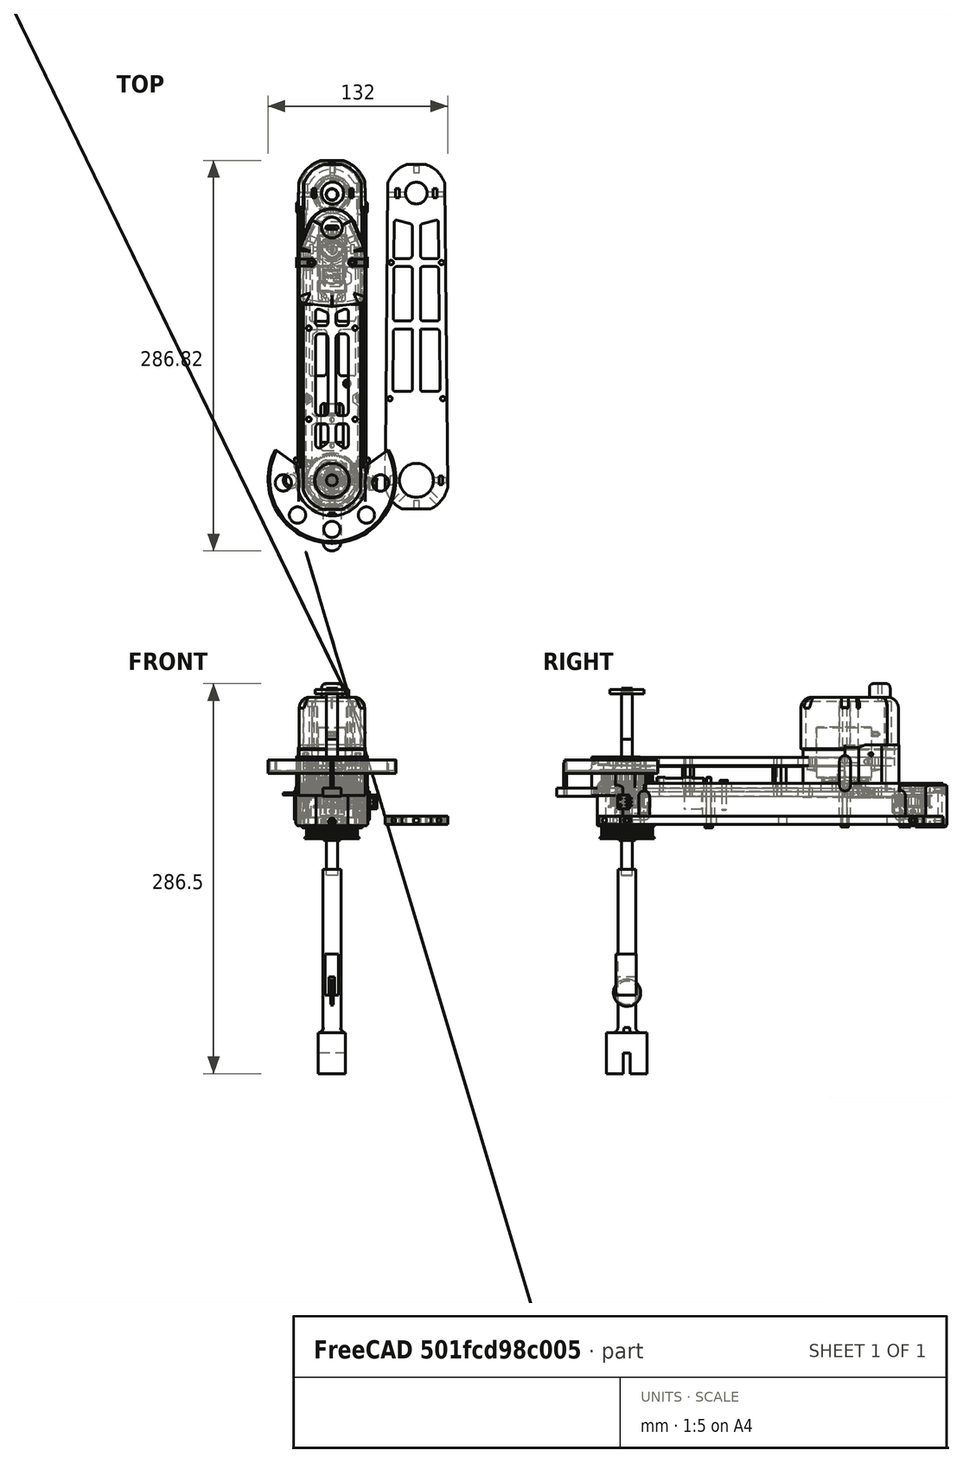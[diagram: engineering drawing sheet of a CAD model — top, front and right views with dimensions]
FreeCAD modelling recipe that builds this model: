
FCSTD DOCUMENT  (FreeCAD 1.0R38641 +468 (Git))
Label: ARM Long
License: All rights reserved
LicenseURL: https://en.wikipedia.org/wiki/All_rights_reserved
objects: Sketcher::SketchObject×133, PartDesign::Pocket×65, PartDesign::Pad×58, Part::Feature×42, PartDesign::Body×32, PartDesign::Fillet×20, App::Part×16, PartDesign::Chamfer×9, Part::FeaturePython×8, PartDesign::Plane×6, PartDesign::Mirrored×4, Mesh::Feature×3, PartDesign::Groove×1, PartDesign::ShapeBinder×1, Part::Mirroring×1
note: 823 computed .brp shape members not serialized (recipe doc carries the construction recipe); baked Part::Feature solids carry a one-line shape summary decoded from their .brp

FEATURE [Part::Feature] Part__Feature  label="MG995"
  Placement = pos=(1.91e-14,159.4,18.9) rot=(0,0,1;4.71239rad)
  shape: bbox 20 x 54.66 x 44.93 mm, 459 faces (baked)
FEATURE [Sketcher::SketchObject] Sketch009
  ArcFitTolerance = 1e-06
  AttachmentSupport = -> [YZ_Plane009]
  FullyConstrained = true
  MakeInternals = false
  MapMode = 5
  Placement = pos=(0,0,0) rot=(0.57735,0.57735,0.57735;2.0944rad)
  sketch-geometry (1):
    g0: Circle CenterX=0 CenterY=0 CenterZ=0 NormalX=0 NormalY=0 NormalZ=1 AngleXU=0 Radius=10
  constraints (2):
    c: Coincident(g0,g-1)
    c: Diameter(g0) = 20
FEATURE [PartDesign::Pad] Pad003
  Direction = (1,0,0)
  Length = 2
  Length2 = 10
  Midplane = true
  Placement = pos=(0,0,0) rot=(1,1,1;2.0944rad)
  Profile = -> Sketch009
  ReferenceAxis = -> Sketch009 [N_Axis]
  Refine = true
  Suppressed = false
  Type = 0
FEATURE [Sketcher::SketchObject] Sketch010
  ArcFitTolerance = 1e-06
  AttachmentSupport = -> [Pad003]
  FullyConstrained = true
  MakeInternals = false
  MapMode = 5
  Placement = pos=(-1,0,0) rot=(0.57735,0.57735,-0.57735;4.18879rad)
FEATURE [Sketcher::SketchObject] Sketch011
  ArcFitTolerance = 1e-06
  AttachmentSupport = -> [XZ_Plane009]
  FullyConstrained = false
  MakeInternals = false
  MapMode = 5
  Placement = pos=(0,0,0) rot=(1,0,0;1.5708rad)
  sketch-geometry (5):
    g0: LineSegment StartX=0.035712 StartY=-10.031 StartZ=0 EndX=-2.23615 EndY=-6.55241 EndZ=0
    g1: LineSegment StartX=-2.23615 StartY=-6.55241 StartZ=0 EndX=-4.35752 EndY=-11.9281 EndZ=0
    g2: LineSegment StartX=-4.35752 StartY=-11.9281 StartZ=0 EndX=3.67657 EndY=-11.9281 EndZ=0
    g3: LineSegment StartX=3.67657 StartY=-11.9281 StartZ=0 EndX=3.0311 EndY=-6.33671 EndZ=0
    g4: LineSegment StartX=3.0311 StartY=-6.33671 StartZ=0 EndX=0.035712 EndY=-10.031 EndZ=0
  constraints (6):
    c: Coincident(g0,g1)
    c: Coincident(g1,g2)
    c: Horizontal(g2)
    c: Coincident(g2,g3)
    c: Coincident(g3,g4)
    c: Coincident(g4,g0)
FEATURE [PartDesign::Groove] Groove
  Angle = 360
  Angle2 = 60
  Axis = (1,0,0)
  Base = (0,0,0)
  BaseFeature = -> Pad003
  Placement = pos=(0,0,0) rot=(1,1,1;2.0944rad)
  Profile = -> Sketch011
  ReferenceAxis = -> Sketch011 [H_Axis]
  Refine = true
  Suppressed = false
  Type = 0
FEATURE [PartDesign::Body] Body006  label="RUEDA"
  AllowCompound = false
  Group = -> [Sketch009,Pad003,Sketch010,Sketch011,Groove]
  Origin = -> Origin009
  Placement = pos=(0,0,-145.2) rot=(0,0,1;0rad)
  Tip = -> Groove
FEATURE [Sketcher::SketchObject] Sketch012
  ArcFitTolerance = 1e-06
  AttachmentSupport = -> [XY_Plane010]
  FullyConstrained = true
  MakeInternals = false
  MapMode = 5
  sketch-geometry (4):
    g0: LineSegment StartX=-5 StartY=7.5 StartZ=0 EndX=-5 EndY=-7.5 EndZ=0
    g1: LineSegment StartX=-5 StartY=-7.5 StartZ=0 EndX=5 EndY=-7.5 EndZ=0
    g2: LineSegment StartX=5 StartY=-7.5 StartZ=0 EndX=5 EndY=7.5 EndZ=0
    g3: LineSegment StartX=5 StartY=7.5 StartZ=0 EndX=-5 EndY=7.5 EndZ=0
  constraints (10):
    c: Coincident(g0,g1)
    c: Coincident(g1,g2)
    c: Coincident(g2,g3)
    c: Coincident(g3,g0)
    c: Vertical(g0)
    c: Horizontal(g1)
    c: Symmetric(g0,g2,g-2)
    c: DistanceX(g0,g2) = 10
    c: DistanceY(g0,g0) = 15
    c: Symmetric(g2,g1,g-1)
FEATURE [PartDesign::Pad] Pad004
  Direction = (0,0,1)
  Length = 30
  Length2 = 10
  Profile = -> Sketch012
  ReferenceAxis = -> Sketch012 [N_Axis]
  Refine = true
  Suppressed = false
  Type = 0
FEATURE [Sketcher::SketchObject] Sketch013
  ArcFitTolerance = 1e-06
  AttachmentSupport = -> [Pad004]
  FullyConstrained = false
  MakeInternals = false
  MapMode = 5
  Placement = pos=(0,-7.5,0) rot=(1,0,0;1.5708rad)
  sketch-geometry (4):
    g0: LineSegment StartX=-1.97312 StartY=37.3431 StartZ=0 EndX=-1.97312 EndY=16.6977 EndZ=0
    g1: LineSegment StartX=-1.97312 StartY=16.6977 StartZ=0 EndX=2.0662 EndY=16.6977 EndZ=0
    g2: LineSegment StartX=2.0662 StartY=16.6977 StartZ=0 EndX=2.0662 EndY=37.3431 EndZ=0
    g3: LineSegment StartX=2.0662 StartY=37.3431 StartZ=0 EndX=-1.97312 EndY=37.3431 EndZ=0
  constraints (8):
    c: Coincident(g0,g1)
    c: Coincident(g1,g2)
    c: Coincident(g2,g3)
    c: Coincident(g3,g0)
    c: Vertical(g0)
    c: Vertical(g2)
    c: Horizontal(g1)
    c: Horizontal(g3)
FEATURE [PartDesign::Pocket] Pocket003
  BaseFeature = -> Pad004
  Direction = (0,1,-2e-16)
  Length = 5
  Length2 = 5
  Profile = -> Sketch013
  ReferenceAxis = -> Sketch013 [N_Axis]
  Refine = true
  Suppressed = false
  Type = 1
FEATURE [PartDesign::Body] Body007  label="HORQUILLA"
  AllowCompound = false
  Group = -> [Sketch012,Pad004,Sketch013,Pocket003]
  Origin = -> Origin010
  Placement = pos=(-0.1,-0.7,-116.9) rot=(1,0,0;3.14159rad)
  Tip = -> Pocket003
FEATURE [Sketcher::SketchObject] Sketch016
  ArcFitTolerance = 1e-06
  AttachmentSupport = -> [XY_Plane012]
  FullyConstrained = false
  MakeInternals = false
  MapMode = 5
  sketch-geometry (11):
    g0: Circle CenterX=0 CenterY=-27.1564 CenterZ=0 NormalX=0 NormalY=0 NormalZ=1 AngleXU=0 Radius=170
    g1: LineSegment StartX=-241.503 StartY=142.844 StartZ=0 EndX=520.637 EndY=142.844 EndZ=0
    g2: Circle CenterX=340 CenterY=-27.1564 CenterZ=0 NormalX=0 NormalY=0 NormalZ=1 AngleXU=0 Radius=170
    g3: LineSegment StartX=-227.087 StartY=-237.156 StartZ=0 EndX=679.032 EndY=-237.156 EndZ=0
    g4: LineSegment StartX=340 StartY=-237.156 StartZ=0 EndX=256.874 EndY=-44.3091 EndZ=0
    g5: LineSegment StartX=256.874 StartY=-44.3091 StartZ=0 EndX=189.582 EndY=111.805 EndZ=0
    g6: LineSegment StartX=340 StartY=-237.156 StartZ=0 EndX=349.666 EndY=-301.689 EndZ=0
    g7: LineSegment StartX=-425.206 StartY=-27.1564 StartZ=0 EndX=717.157 EndY=-27.1564 EndZ=0
    g8: LineSegment [constr] StartX=162.156 StartY=-197.156 StartZ=0 EndX=684.616 EndY=-197.156 EndZ=0
    g9: LineSegment [constr] StartX=340 StartY=225.233 StartZ=0 EndX=340 EndY=-279.546 EndZ=0
    g10: Circle CenterX=340 CenterY=-27.1564 CenterZ=0 NormalX=0 NormalY=0 NormalZ=1 AngleXU=0 Radius=55
  constraints (23):
    c: Diameter(g0) = 340
    c: PointOnObject(g0,g-2)
    c: Horizontal(g1)
    c: Tangent(g1,g0)
    c: Block(g1)
    c: Diameter(g2) = 340
    c: Tangent(g0,g2)
    c: Horizontal(g3)
    c: DistanceY(g3,g1) = 380
    c: PointOnObject(g4,g3)
    c: Coincident(g4,g5)
    c: Distance(g4,g5) = 170
    c: Distance(g4,g4) = 210
    c: Coincident(g6,g4)
    c: Vertical(g2,g4)
    c: Horizontal(g7)
    c: Horizontal(g8)
    c: Tangent(g8,g2)
    c: PointOnObject(g2,g9)
    c: PointOnObject(g4,g9)
    c: Symmetric(g9,g9,g10)
    c: Diameter(g10) = 110
    c: DistanceY(g7,g1) = 170
FEATURE [PartDesign::Body] Body009  label="GEOMETRY"
  AllowCompound = false
  Group = -> [Sketch016]
  Origin = -> Origin012
FEATURE [Sketcher::SketchObject] Sketch018
  ArcFitTolerance = 1e-06
  AttachmentSupport = -> [XY_Plane015]
  FullyConstrained = false
  MakeInternals = false
  MapMode = 5
  sketch-geometry (40):
    g0: LineSegment [constr] StartX=-66.1561 StartY=0 StartZ=0 EndX=72.2125 EndY=0 EndZ=0
    g1: LineSegment [constr] StartX=-43.6589 StartY=170 StartZ=0 EndX=73.8752 EndY=170 EndZ=0
    g2: LineSegment StartX=-21 StartY=170 StartZ=0 EndX=-21 EndY=-6.55744 EndZ=0
    g3: LineSegment StartX=-6.55744 StartY=-21 StartZ=0 EndX=6.55744 EndY=-21 EndZ=0
    g4: LineSegment StartX=21 StartY=-6.55744 StartZ=0 EndX=21 EndY=170 EndZ=0
    g5: Circle CenterX=-1.1e-15 CenterY=0 CenterZ=0 NormalX=0 NormalY=0 NormalZ=1 AngleXU=0 Radius=12.65
    g6: ArcOfCircle CenterX=-1.1e-15 CenterY=0 CenterZ=0 NormalX=0 NormalY=0 NormalZ=1 AngleXU=0 Radius=22 StartAngle=3.44426 EndAngle=4.40972
    g7: ArcOfCircle CenterX=-1.1e-15 CenterY=0 CenterZ=0 NormalX=0 NormalY=0 NormalZ=1 AngleXU=0 Radius=22 StartAngle=5.01505 EndAngle=5.98052
    g8: ArcOfCircle CenterX=0 CenterY=181.247 CenterZ=0 NormalX=0 NormalY=0 NormalZ=1 AngleXU=0 Radius=15.1624 StartAngle=0.389165 EndAngle=2.75243
    g9: LineSegment StartX=-14.0287 StartY=187 StartZ=0 EndX=-21 EndY=170 EndZ=0
    g10: LineSegment StartX=14.0287 StartY=187 StartZ=0 EndX=21 EndY=170 EndZ=0
    g11: LineSegment [constr] StartX=-50.6378 StartY=187 StartZ=0 EndX=60.3893 EndY=187 EndZ=0
    g12: GeomPoint X=3.72478 Y=-21 Z=0
    g13: LineSegment StartX=-10.8839 StartY=180.662 StartZ=0 EndX=-10.8839 EndY=138.383 EndZ=0
    g14: LineSegment [constr] StartX=-10.8839 StartY=180.662 StartZ=0 EndX=-10.8839 EndY=138.383 EndZ=0
    g15: LineSegment [constr] StartX=-10.8839 StartY=138.383 StartZ=0 EndX=10.8839 EndY=138.383 EndZ=0
    g16: LineSegment [constr] StartX=10.8839 StartY=138.383 StartZ=0 EndX=10.8839 EndY=180.662 EndZ=0
    g17: LineSegment StartX=10.8839 StartY=180.662 StartZ=0 EndX=10.8839 EndY=154.01 EndZ=0
    g18: LineSegment StartX=11.1741 StartY=153.519 StartZ=0 EndX=13.7289 EndY=152.117 EndZ=0
    g19: LineSegment StartX=14.0513 StartY=151.572 StartZ=0 EndX=14.0513 EndY=145.924 EndZ=0
    g20: LineSegment StartX=10.8839 StartY=138.383 StartZ=0 EndX=10.8839 EndY=143.674 EndZ=0
    g21: LineSegment StartX=11.1847 StartY=144.155 StartZ=0 EndX=13.7156 EndY=145.387 EndZ=0
    g22: ArcOfCircle CenterX=0 CenterY=183.662 CenterZ=0 NormalX=0 NormalY=0 NormalZ=1 AngleXU=0 Radius=1 StartAngle=1.2e-15 EndAngle=3.14159
    g23: LineSegment StartX=1 StartY=183.662 StartZ=0 EndX=1 EndY=180.662 EndZ=0
    g24: LineSegment StartX=-1 StartY=183.662 StartZ=0 EndX=-1 EndY=180.662 EndZ=0
    g25: LineSegment StartX=-10.8839 StartY=180.662 StartZ=0 EndX=-1 EndY=180.662 EndZ=0
    g26: LineSegment StartX=10.8839 StartY=180.662 StartZ=0 EndX=1 EndY=180.662 EndZ=0
    g27: ArcOfCircle CenterX=13.4297 CenterY=151.572 CenterZ=0 NormalX=0 NormalY=0 NormalZ=1 AngleXU=0 Radius=0.621593 StartAngle=-3.6e-15 EndAngle=1.06874
    g28: GeomPoint [constr] X=14.0513 Y=151.94 Z=0
    g29: ArcOfCircle CenterX=13.4543 CenterY=145.924 CenterZ=0 NormalX=0 NormalY=0 NormalZ=1 AngleXU=0 Radius=0.597072 StartAngle=5.16551 EndAngle=6.28319
    g30: GeomPoint [constr] X=14.0513 Y=145.551 Z=0
    g31: ArcOfCircle CenterX=11.4189 CenterY=143.674 CenterZ=0 NormalX=0 NormalY=0 NormalZ=1 AngleXU=0 Radius=0.535029 StartAngle=2.02392 EndAngle=3.14159
    g32: GeomPoint [constr] X=10.8839 Y=144.009 Z=0
    g33: ArcOfCircle CenterX=11.4434 CenterY=154.01 CenterZ=0 NormalX=0 NormalY=0 NormalZ=1 AngleXU=0 Radius=0.559551 StartAngle=3.14159 EndAngle=4.21034
    g34: GeomPoint [constr] X=10.8839 Y=153.678 Z=0
    g35: ArcOfCircle CenterX=0 CenterY=135.596 CenterZ=0 NormalX=0 NormalY=0 NormalZ=1 AngleXU=0 Radius=1 StartAngle=3.14159 EndAngle=6.28319
    g36: LineSegment StartX=1 StartY=138.383 StartZ=0 EndX=1 EndY=135.596 EndZ=0
    g37: LineSegment StartX=-1 StartY=138.383 StartZ=0 EndX=-1 EndY=135.596 EndZ=0
    g38: LineSegment StartX=-1 StartY=138.383 StartZ=0 EndX=-10.8839 EndY=138.383 EndZ=0
    g39: LineSegment StartX=1 StartY=138.383 StartZ=0 EndX=10.8839 EndY=138.383 EndZ=0
  constraints (84):
    c: Horizontal(g1)
    c: DistanceY(g0,g1) = 170
    c: Vertical(g2)
    c: PointOnObject(g2,g1)
    c: PointOnObject(g5,g0)
    c: Symmetric(g10,g9,g-2)
    c: Diameter(g5) = 25.3
    c: DistanceX(g2,g4) = 42
    c: Symmetric(g2,g4,g-2)
    c: Symmetric(g3,g3,g-2)
    c: Coincident(g6,g2)
    c: Coincident(g6,g3)
    c: Coincident(g7,g6)
    c: Coincident(g7,g4)
    c: Coincident(g7,g3)
    c: Coincident(g6,g5)
    c: PointOnObject(g8,g-2)
    c: Tangent(g9,g8) = -1.5708
    c: Tangent(g10,g8) = 1.5708
    c: Coincident(g2,g9)
    c: Coincident(g10,g4)
    c: Horizontal(g11)
    c: PointOnObject(g8,g11)
    c: DistanceY(g1,g11) = 17
    c: PointOnObject(g12,g3)
    c: DistanceY(g12,g0) = 21
    c: PointOnObject(g5,g-1)
    c: PointOnObject(g0,g-1)
    c: Vertical(g13)
    c: Symmetric(g13,g15,g-2)
    c: Coincident(g14,g15)
    c: Coincident(g15,g16)
    c: Vertical(g14)
    c: Vertical(g16)
    c: Horizontal(g15)
    c: Symmetric(g16,g14,g-2)
    c: Radius(g6) = 22
    c: PointOnObject(g34,g16)
    c: Vertical(g17)
    c: Vertical(g19)
    c: Coincident(g20,g15)
    c: PointOnObject(g32,g16)
    c: Tangent(g22,g23) = 1.5708
    c: Tangent(g22,g24) = -1.5708
    c: Vertical(g24)
    c: PointOnObject(g22,g-2)
    c: Coincident(g25,g13)
    c: Horizontal(g25)
    c: Coincident(g26,g17)
    c: Horizontal(g26)
    c: Horizontal(g25,g26)
    c: Coincident(g24,g25)
    c: Coincident(g23,g26)
    c: DistanceX(g24,g23) = 2
    c: Vertical(g23)
    c: DistanceY(g23,g22) = 3
    c: PointOnObject(g28,g18)
    c: PointOnObject(g28,g19)
    c: Tangent(g18,g27) = 1.5708
    c: Tangent(g19,g27) = 1.5708
    c: PointOnObject(g30,g19)
    c: PointOnObject(g30,g21)
    c: Tangent(g19,g29) = 1.5708
    c: Tangent(g21,g29) = -1.5708
    c: PointOnObject(g32,g20)
    c: PointOnObject(g32,g21)
    c: Tangent(g20,g31) = 1.5708
    c: Tangent(g21,g31) = 1.5708
    c: PointOnObject(g34,g18)
    c: Tangent(g17,g33) = -1.5708
    c: Tangent(g18,g33) = -1.5708
    c: Tangent(g35,g36) = 1.5708
    c: Tangent(g35,g37) = -1.5708
    c: Vertical(g37)
    c: PointOnObject(g35,g-2)
    c: PointOnObject(g37,g15)
    c: PointOnObject(g36,g15)
    c: Vertical(g36)
    c: Coincident(g38,g37)
    c: Coincident(g38,g13)
    c: Coincident(g39,g36)
    c: Coincident(g39,g15)
    c: DistanceX(g37,g36) = 2
    c: Coincident(g16,g17)
FEATURE [PartDesign::Pad] Pad008
  Direction = (0,0,1)
  Length = 6
  Length2 = 10
  Profile = -> Sketch018
  ReferenceAxis = -> Sketch018 [N_Axis]
  Refine = true
  Suppressed = false
  Type = 0
FEATURE [Sketcher::SketchObject] Sketch020
  ArcFitTolerance = 1e-06
  AttachmentSupport = -> [Pad008]
  ExternalGeometry = -> [Pad008]
  FullyConstrained = false
  MakeInternals = false
  MapMode = 5
  Placement = pos=(0,0,6) rot=(0,0,1;0rad)
  sketch-geometry (16):
    g0: LineSegment [constr] StartX=-17 StartY=112 StartZ=0 EndX=-17 EndY=45 EndZ=0
    g1: LineSegment [constr] StartX=-17 StartY=45 StartZ=0 EndX=17 EndY=45 EndZ=0
    g2: LineSegment [constr] StartX=17 StartY=45 StartZ=0 EndX=17 EndY=112 EndZ=0
    g3: LineSegment [constr] StartX=17 StartY=112 StartZ=0 EndX=-17 EndY=112 EndZ=0
    g4: Circle CenterX=17 CenterY=112 CenterZ=0 NormalX=0 NormalY=0 NormalZ=1 AngleXU=0 Radius=1.7
    g5: Circle CenterX=-17 CenterY=112 CenterZ=0 NormalX=0 NormalY=0 NormalZ=1 AngleXU=0 Radius=1.7
    g6: Circle CenterX=17 CenterY=45 CenterZ=0 NormalX=0 NormalY=0 NormalZ=1 AngleXU=0 Radius=1.7
    g7: Circle CenterX=-17 CenterY=45 CenterZ=0 NormalX=0 NormalY=0 NormalZ=1 AngleXU=0 Radius=1.7
    g8: LineSegment [constr] StartX=-5 StartY=183.792 StartZ=0 EndX=-5 EndY=135.241 EndZ=0
    g9: LineSegment [constr] StartX=-5 StartY=135.241 StartZ=0 EndX=5 EndY=135.241 EndZ=0
    g10: LineSegment [constr] StartX=5 StartY=135.241 StartZ=0 EndX=5 EndY=183.792 EndZ=0
    g11: LineSegment [constr] StartX=5 StartY=183.792 StartZ=0 EndX=-5 EndY=183.792 EndZ=0
    g12: Circle CenterX=-5 CenterY=135.241 CenterZ=0 NormalX=0 NormalY=0 NormalZ=1 AngleXU=0 Radius=1.25
    g13: Circle CenterX=5 CenterY=135.241 CenterZ=0 NormalX=0 NormalY=0 NormalZ=1 AngleXU=0 Radius=1.25
    g14: Circle CenterX=5 CenterY=183.792 CenterZ=0 NormalX=0 NormalY=0 NormalZ=1 AngleXU=0 Radius=1.25
    g15: Circle CenterX=-5 CenterY=183.792 CenterZ=0 NormalX=0 NormalY=0 NormalZ=1 AngleXU=0 Radius=1.25
  constraints (36):
    c: Coincident(g0,g1)
    c: Coincident(g1,g2)
    c: Coincident(g2,g3)
    c: Coincident(g3,g0)
    c: Vertical(g0)
    c: Vertical(g2)
    c: Horizontal(g1)
    c: Symmetric(g0,g2,g-2)
    c: DistanceX(g-1,g1) = 17
    c: Coincident(g4,g2)
    c: Coincident(g5,g0)
    c: Coincident(g6,g1)
    c: Coincident(g7,g0)
    c: Equal(g7,g6)
    c: Equal(g7,g4)
    c: Equal(g7,g5)
    c: Diameter(g7) = 3.4
    c: DistanceY(g-1,g1) = 45
    c: DistanceY(g-1,g2) = 112
    c: Coincident(g8,g9)
    c: Coincident(g9,g10)
    c: Coincident(g10,g11)
    c: Coincident(g11,g8)
    c: Vertical(g8)
    c: Vertical(g10)
    c: Horizontal(g9)
    c: Symmetric(g8,g10,g-2)
    c: Coincident(g12,g8)
    c: Coincident(g13,g9)
    c: Coincident(g14,g10)
    c: Coincident(g15,g8)
    c: Equal(g15,g14)
    c: Equal(g15,g12)
    c: Equal(g15,g13)
    c: Diameter(g15) = 2.5
    c: DistanceX(g8,g10) = 10
FEATURE [PartDesign::Pocket] Pocket005
  BaseFeature = -> Pad008
  Direction = (0,0,-1)
  Length = 5
  Length2 = 5
  Profile = -> Sketch020
  ReferenceAxis = -> Sketch020 [N_Axis]
  Refine = true
  Suppressed = false
  Type = 1
FEATURE [Part::Feature] Part__Feature003  label="Шкив GT2 60T b8 (6mm)"
  Placement = pos=(0,5.4e-15,24.6) rot=(1,0,0;4.71239rad)
  shape: bbox 40 x 40 x 16 mm, 326 faces (baked)
FEATURE [Part::Feature] Part__Feature004  label="Шкив GT2 60T b8 (6mm)001"
  Placement = pos=(0,-1.42e-14,-16) rot=(-1,0,0;1.5708rad)
  shape: bbox 40 x 40 x 16 mm, 326 faces (baked)
FEATURE [Sketcher::SketchObject] Sketch021
  ArcFitTolerance = 1e-06
  AttachmentSupport = -> [XY_Plane017]
  FullyConstrained = false
  MakeInternals = false
  MapMode = 5
  sketch-geometry (44):
    g0: LineSegment StartX=-23 StartY=-5 StartZ=0 EndX=-21 EndY=218 EndZ=0
    g1: LineSegment StartX=23 StartY=-5 StartZ=0 EndX=21 EndY=218 EndZ=0
    g2: Circle CenterX=4.97e-14 CenterY=211 CenterZ=0 NormalX=0 NormalY=0 NormalZ=1 AngleXU=0 Radius=8.1
    g3: Circle CenterX=0 CenterY=-141.268 CenterZ=0 NormalX=0 NormalY=0 NormalZ=1 AngleXU=0 Radius=9.71
    g4: Circle CenterX=0 CenterY=0 CenterZ=0 NormalX=0 NormalY=0 NormalZ=1 AngleXU=0 Radius=8.1
    g5: LineSegment StartX=-7 StartY=232 StartZ=0 EndX=7 EndY=232 EndZ=0
    g6: ArcOfCircle CenterX=4.97e-14 CenterY=211 CenterZ=0 NormalX=0 NormalY=0 NormalZ=1 AngleXU=0 Radius=22.1359 StartAngle=1.89255 EndAngle=2.81984
    g7: ArcOfCircle CenterX=4.97e-14 CenterY=211 CenterZ=0 NormalX=0 NormalY=0 NormalZ=1 AngleXU=0 Radius=22.1359 StartAngle=0.321751 EndAngle=1.24905
    g8: LineSegment StartX=-10.6301 StartY=-21 StartZ=0 EndX=10.6301 EndY=-21 EndZ=0
    g9: ArcOfCircle CenterX=0 CenterY=0 CenterZ=0 NormalX=0 NormalY=0 NormalZ=1 AngleXU=0 Radius=23.5372 StartAngle=3.35565 EndAngle=4.2438
    g10: ArcOfCircle CenterX=0 CenterY=0 CenterZ=0 NormalX=0 NormalY=0 NormalZ=1 AngleXU=0 Radius=23.5372 StartAngle=5.18098 EndAngle=6.06912
    g11: LineSegment [constr] StartX=-22.417 StartY=60 StartZ=0 EndX=22.417 EndY=60 EndZ=0
    g12: GeomPoint [constr] X=32.4275 Y=0 Z=0
    g13: GeomPoint [constr] X=21.5202 Y=160 Z=0
    g14: LineSegment [constr] StartX=21.5202 StartY=160 StartZ=0 EndX=-21.5202 EndY=160 EndZ=0
    g15: GeomPoint [constr] X=18.5202 Y=160 Z=0
    g16: GeomPoint [constr] X=-18.5202 Y=160 Z=0
    g17: GeomPoint [constr] X=-19.417 Y=60 Z=0
    g18: GeomPoint [constr] X=19.417 Y=60 Z=0
    g19: LineSegment StartX=13.6 StartY=3.25 StartZ=0 EndX=13.6 EndY=-3.25 EndZ=0
    g20: LineSegment StartX=13.6 StartY=-3.25 StartZ=0 EndX=16.4 EndY=-3.25 EndZ=0
    g21: LineSegment StartX=16.4 StartY=-3.25 StartZ=0 EndX=16.4 EndY=3.25 EndZ=0
    g22: LineSegment StartX=16.4 StartY=3.25 StartZ=0 EndX=13.6 EndY=3.25 EndZ=0
    g23: GeomPoint [constr] X=15 Y=0 Z=0
    g24: LineSegment StartX=-16.4 StartY=3.25 StartZ=0 EndX=-16.4 EndY=-3.25 EndZ=0
    g25: LineSegment StartX=-16.4 StartY=-3.25 StartZ=0 EndX=-13.6 EndY=-3.25 EndZ=0
    g26: LineSegment StartX=-13.6 StartY=-3.25 StartZ=0 EndX=-13.6 EndY=3.25 EndZ=0
    g27: LineSegment StartX=-13.6 StartY=3.25 StartZ=0 EndX=-16.4 EndY=3.25 EndZ=0
    g28: GeomPoint [constr] X=-15 Y=0 Z=0
    g29: LineSegment [constr] StartX=-13.769 StartY=211 StartZ=0 EndX=13.769 EndY=211 EndZ=0
    g30: LineSegment StartX=12.369 StartY=214.25 StartZ=0 EndX=12.369 EndY=207.75 EndZ=0
    g31: LineSegment StartX=12.369 StartY=207.75 StartZ=0 EndX=15.169 EndY=207.75 EndZ=0
    g32: LineSegment StartX=15.169 StartY=207.75 StartZ=0 EndX=15.169 EndY=214.25 EndZ=0
    g33: LineSegment StartX=15.169 StartY=214.25 StartZ=0 EndX=12.369 EndY=214.25 EndZ=0
    g34: GeomPoint [constr] X=13.769 Y=211 Z=0
    g35: LineSegment StartX=-15.169 StartY=214.25 StartZ=0 EndX=-15.169 EndY=207.75 EndZ=0
    g36: LineSegment StartX=-15.169 StartY=207.75 StartZ=0 EndX=-12.369 EndY=207.75 EndZ=0
    g37: LineSegment StartX=-12.369 StartY=207.75 StartZ=0 EndX=-12.369 EndY=214.25 EndZ=0
    g38: LineSegment StartX=-12.369 StartY=214.25 StartZ=0 EndX=-15.169 EndY=214.25 EndZ=0
    g39: GeomPoint [constr] X=-13.769 Y=211 Z=0
    g40: Circle CenterX=18.5202 CenterY=160 CenterZ=0 NormalX=0 NormalY=0 NormalZ=1 AngleXU=0 Radius=1.7
    g41: Circle CenterX=-18.5202 CenterY=160 CenterZ=0 NormalX=0 NormalY=0 NormalZ=1 AngleXU=0 Radius=1.7
    g42: Circle CenterX=-19.417 CenterY=60 CenterZ=0 NormalX=0 NormalY=0 NormalZ=1 AngleXU=0 Radius=1.7
    g43: Circle CenterX=19.417 CenterY=60 CenterZ=0 NormalX=0 NormalY=0 NormalZ=1 AngleXU=0 Radius=1.7
  constraints (106):
    c: PointOnObject(g3,g-2)
    c: Symmetric(g5,g5,g-2)
    c: DistanceY(g2,g5) = 21
    c: Coincident(g6,g2)
    c: Coincident(g6,g5)
    c: Coincident(g6,g0)
    c: Coincident(g7,g2)
    c: Coincident(g7,g5)
    c: Coincident(g7,g1)
    c: Symmetric(g8,g8,g-2)
    c: DistanceY(g8,g4) = 21
    c: PointOnObject(g4,g-2)
    c: PointOnObject(g4,g-1)
    c: Coincident(g9,g4)
    c: Coincident(g9,g0)
    c: Coincident(g9,g8)
    c: Coincident(g10,g4)
    c: Coincident(g10,g1)
    c: Coincident(g10,g8)
    c: PointOnObject(g12,g-1)
    c: DistanceY(g12,g11) = 60
    c: DistanceY(g12,g13) = 160
    c: DistanceY(g12,g2) = 211
    c: Diameter(g4) = 16.2
    c: Diameter(g2) = 16.2
    c: Horizontal(g0,g1)
    c: DistanceX(g0,g1) = 46
    c: DistanceY(g0,g4) = 5
    c: Symmetric(g0,g1,g-2)
    c: DistanceX(g0,g1) = 42
    c: DistanceY(g2,g1) = 7
    c: Coincident(g14,g13)
    c: Horizontal(g14)
    c: PointOnObject(g13,g1)
    c: PointOnObject(g15,g14)
    c: DistanceX(g15,g13) = 3
    c: PointOnObject(g14,g0)
    c: PointOnObject(g16,g14)
    c: DistanceX(g14,g16) = 3
    c: PointOnObject(g11,g1)
    c: Horizontal(g11)
    c: PointOnObject(g11,g0)
    c: PointOnObject(g17,g11)
    c: PointOnObject(g18,g11)
    c: DistanceX(g18,g11) = 3
    c: DistanceX(g11,g17) = 3
    c: Coincident(g19,g20)
    c: Coincident(g20,g21)
    c: Coincident(g21,g22)
    c: Coincident(g22,g19)
    c: Vertical(g19)
    c: Vertical(g21)
    c: Horizontal(g20)
    c: Horizontal(g22)
    c: Symmetric(g21,g19,g23)
    c: PointOnObject(g23,g-1)
    c: Coincident(g24,g25)
    c: Coincident(g25,g26)
    c: Coincident(g26,g27)
    c: Coincident(g27,g24)
    c: Vertical(g24)
    c: Vertical(g26)
    c: Horizontal(g25)
    c: Horizontal(g27)
    c: Symmetric(g26,g24,g28)
    c: PointOnObject(g28,g-1)
    c: DistanceX(g24,g26) = 2.8
    c: DistanceY(g25,g26) = 6.5
    c: Equal(g26,g19)
    c: Equal(g22,g27)
    c: DistanceX(g28,g4) = 15
    c: DistanceX(g4,g23) = 15
    c: PointOnObject(g2,g29)
    c: Coincident(g30,g31)
    c: Coincident(g31,g32)
    c: Coincident(g32,g33)
    c: Coincident(g33,g30)
    c: Vertical(g30)
    c: Vertical(g32)
    c: Horizontal(g31)
    c: Horizontal(g33)
    c: Symmetric(g32,g30,g34)
    c: Coincident(g34,g29)
    c: Coincident(g35,g36)
    c: Coincident(g36,g37)
    c: Coincident(g37,g38)
    c: Coincident(g38,g35)
    c: Vertical(g35)
    c: Vertical(g37)
    c: Horizontal(g36)
    c: Horizontal(g38)
    c: Symmetric(g37,g35,g39)
    c: Coincident(g39,g29)
    c: DistanceX(g35,g36) = 2.8
    c: DistanceY(g36,g37) = 6.5
    c: Symmetric(g29,g29,g-2)
    c: Equal(g37,g30)
    c: Equal(g38,g33)
    c: Coincident(g40,g15)
    c: Coincident(g41,g16)
    c: Coincident(g42,g17)
    c: Coincident(g43,g18)
    c: Equal(g43,g42)
    c: Equal(g43,g41)
    c: Equal(g43,g40)
    c: Diameter(g43) = 3.4
FEATURE [PartDesign::Pad] Pad009
  Direction = (0,0,1)
  Length = 6
  Length2 = 10
  Profile = -> Sketch021
  ReferenceAxis = -> Sketch021 [N_Axis]
  Refine = true
  Suppressed = false
  Type = 0
FEATURE [Sketcher::SketchObject] Sketch022
  ArcFitTolerance = 1e-06
  AttachmentSupport = -> [XY_Plane018]
  FullyConstrained = true
  MakeInternals = false
  MapMode = 5
  sketch-geometry (1):
    g0: Circle CenterX=0 CenterY=0 CenterZ=0 NormalX=0 NormalY=0 NormalZ=1 AngleXU=0 Radius=4
  constraints (2):
    c: Coincident(g0,g-1)
    c: Diameter(g0) = 8
FEATURE [PartDesign::Pad] Pad010
  Direction = (0,0,1)
  Length = 40
  Length2 = 10
  Profile = -> Sketch022
  ReferenceAxis = -> Sketch022 [N_Axis]
  Refine = true
  Suppressed = false
  Type = 0
FEATURE [PartDesign::Body] Body014  label="ROD 8X40"
  AllowCompound = false
  Group = -> [Sketch022,Pad010]
  Origin = -> Origin018
  Placement = pos=(0,3e-16,1.1) rot=(0,0,1;0rad)
  Tip = -> Pad010
FEATURE [Sketcher::SketchObject] Sketch023
  ArcFitTolerance = 1e-06
  AttachmentSupport = -> [XY_Plane019]
  FullyConstrained = true
  MakeInternals = false
  MapMode = 5
  sketch-geometry (1):
    g0: Circle CenterX=0 CenterY=0 CenterZ=0 NormalX=0 NormalY=0 NormalZ=1 AngleXU=0 Radius=4
  constraints (2):
    c: Coincident(g0,g-1)
    c: Diameter(g0) = 8
FEATURE [PartDesign::Pad] Pad011
  Direction = (0,0,1)
  Length = 60
  Length2 = 10
  Profile = -> Sketch023
  ReferenceAxis = -> Sketch023 [N_Axis]
  Refine = true
  Suppressed = false
  Type = 0
FEATURE [PartDesign::Body] Body015  label="ROD 8X60"
  AllowCompound = false
  Group = -> [Sketch023,Pad011]
  Origin = -> Origin019
  Placement = pos=(0,1e-16,1) rot=(1,0,0;3.14159rad)
  Tip = -> Pad011
FEATURE [Sketcher::SketchObject] Sketch024
  ArcFitTolerance = 1e-06
  AttachmentSupport = -> [XY_Plane020]
  FullyConstrained = true
  MakeInternals = false
  MapMode = 5
  sketch-geometry (1):
    g0: Circle CenterX=0 CenterY=0 CenterZ=0 NormalX=0 NormalY=0 NormalZ=1 AngleXU=0 Radius=4
  constraints (2):
    c: Coincident(g0,g-1)
    c: Diameter(g0) = 8
FEATURE [PartDesign::Pad] Pad012
  Direction = (0,0,1)
  Length = 80
  Length2 = 10
  Profile = -> Sketch024
  ReferenceAxis = -> Sketch024 [N_Axis]
  Refine = true
  Suppressed = false
  Type = 0
FEATURE [PartDesign::Body] Body016  label="ROD 8X80"
  AllowCompound = false
  Group = -> [Sketch024,Pad012]
  Origin = -> Origin020
  Placement = pos=(0,0,-1.6) rot=(0,0,1;0rad)
  Tip = -> Pad012
FEATURE [Part::Feature] Part__Feature008  label="p  BEARING, METRIC 600 MINIATURE SERIES, DOUBLE-SEALED  8mm ID × 22 OD × 7 W  —  608-2RS001"
  Placement = pos=(0,169.9,1.8) rot=(0,0,1;0rad)
  shape: bbox 23.81 x 23.81 x 7.015 mm, 606 faces (baked)
FEATURE [Part::Feature] Part__Feature010  label="bearing"
  shape: bbox 8.659 x 4.3 x 8.659 mm, 17 faces (baked)
FEATURE [Part::Feature] Part__Feature011  label="bearing001"
  shape: bbox 8.659 x 4.3 x 8.659 mm, 17 faces (baked)
FEATURE [App::Part] bearing  label="bearing002"
  Group = -> [Part__Feature010,Part__Feature011]
  Origin = -> Origin021
FEATURE [Part::Feature] Part__Feature012  label="outer_plate"
  shape: bbox 12.9 x 8.6 x 12.9 mm, 12 faces (baked)
FEATURE [App::Part] GT2_Pulley_3mm_bore_v8  label="GT2 Pulley 3mm bore v8"
  Group = -> [bearing,Part__Feature012]
  Origin = -> Origin022
  Placement = pos=(11.5,71.2,-4) rot=(1,0,0;4.71239rad)
FEATURE [Part::FeaturePython] Screw002  label="M3x20-Screw"  # WARN: FeaturePython — macro-defined, semantics opaque (R4)
  Diameter = 1
  Invert = false
  LeftHanded = false
  Length = 6
  LengthCustom = 20
  MatchOuter = false
  OffsetAngle = 0
  Placement = pos=(11.2,71.1,9) rot=(0,0,1;0rad)
  Thread = false
  Type = 37
FEATURE [Part::FeaturePython] Screw  label="M3x35-Screw"  # WARN: FeaturePython — macro-defined, semantics opaque (R4)
  Diameter = 1
  Invert = false
  LeftHanded = false
  Length = 7
  LengthCustom = 35
  MatchOuter = false
  OffsetAngle = 0
  Placement = pos=(19.5,60,-22) rot=(1,0,0;3.14159rad)
  Thread = false
  Type = 37
FEATURE [Part::FeaturePython] Screw003  label="M3x35-Screw016"  # WARN: FeaturePython — macro-defined, semantics opaque (R4)
  Diameter = 1
  Invert = false
  LeftHanded = false
  Length = 7
  LengthCustom = 35
  MatchOuter = false
  OffsetAngle = 0
  Placement = pos=(18.5,160,-21.5) rot=(1,0,0;3.14159rad)
  Thread = false
  Type = 37
FEATURE [Part::FeaturePython] Screw004  label="M3x35-Screw017"  # WARN: FeaturePython — macro-defined, semantics opaque (R4)
  Diameter = 1
  Invert = false
  LeftHanded = false
  Length = 7
  LengthCustom = 35
  MatchOuter = false
  OffsetAngle = 0
  Placement = pos=(-19,60,-22) rot=(1,0,0;3.14159rad)
  Thread = false
  Type = 37
FEATURE [Part::FeaturePython] Screw005  label="M3x35-Screw018"  # WARN: FeaturePython — macro-defined, semantics opaque (R4)
  Diameter = 1
  Invert = false
  LeftHanded = false
  Length = 7
  LengthCustom = 35
  MatchOuter = false
  OffsetAngle = 0
  Placement = pos=(-18.5,160,-21.5) rot=(1,0,0;3.14159rad)
  Thread = false
  Type = 37
FEATURE [Sketcher::SketchObject] Sketch032
  ArcFitTolerance = 1e-06
  AttachmentSupport = -> [XY_Plane025]
  FullyConstrained = false
  MakeInternals = false
  MapMode = 5
  sketch-geometry (12):
    g0: LineSegment StartX=-24 StartY=-5.92701 StartZ=0 EndX=-24 EndY=9.81302 EndZ=0
    g1: LineSegment StartX=-24 StartY=9.81302 StartZ=0 EndX=-21 EndY=9.81302 EndZ=0
    g2: LineSegment StartX=24 StartY=-5.90211 StartZ=0 EndX=24 EndY=9.81302 EndZ=0
    g3: LineSegment StartX=24 StartY=9.81302 StartZ=0 EndX=21 EndY=9.81302 EndZ=0
    g4: LineSegment StartX=21 StartY=9.81302 StartZ=0 EndX=21 EndY=-5.82403 EndZ=0
    g5: LineSegment StartX=-21 StartY=9.81302 StartZ=0 EndX=-21 EndY=-6.01711 EndZ=0
    g6: LineSegment StartX=-6.33223 StartY=-21.23 StartZ=0 EndX=5.61899 EndY=-21.23 EndZ=0
    g7: ArcOfCircle CenterX=0.225207 CenterY=-0.230007 CenterZ=0 NormalX=0 NormalY=0 NormalZ=1 AngleXU=0 Radius=22 StartAngle=3.40778 EndAngle=4.40972
    g8: ArcOfCircle CenterX=-0.22034 CenterY=-0.0191096 CenterZ=0 NormalX=0 NormalY=0 NormalZ=1 AngleXU=0 Radius=22 StartAngle=4.98103 EndAngle=6.01616
    g9: LineSegment StartX=-6.35632 StartY=-24.23 StartZ=0 EndX=5.7014 EndY=-24.23 EndZ=0
    g10: ArcOfCircle CenterX=0.225207 CenterY=-0.230007 CenterZ=0 NormalX=0 NormalY=0 NormalZ=1 AngleXU=0 Radius=24.8861 StartAngle=3.37256 EndAngle=4.44474
    g11: ArcOfCircle CenterX=-0.22034 CenterY=-0.0191096 CenterZ=0 NormalX=0 NormalY=0 NormalZ=1 AngleXU=0 Radius=24.9246 StartAngle=4.95227 EndAngle=6.0449
  constraints (30):
    c: Coincident(g1,g0)
    c: Horizontal(g1)
    c: Coincident(g2,g3)
    c: Horizontal(g3)
    c: Coincident(g3,g4)
    c: Vertical(g4)
    c: Vertical(g0)
    c: Coincident(g5,g1)
    c: Vertical(g5)
    c: Vertical(g2)
    c: Symmetric(g1,g3,g-2)
    c: DistanceX(g3,g2) = 3
    c: DistanceX(g1,g3) = 42
    c: Horizontal(g6)
    c: Coincident(g7,g5)
    c: Coincident(g7,g6)
    c: Coincident(g8,g6)
    c: Coincident(g8,g4)
    c: Horizontal(g9)
    c: DistanceY(g9,g6) = 3
    c: Coincident(g10,g7)
    c: Coincident(g10,g0)
    c: Coincident(g10,g9)
    c: Coincident(g11,g8)
    c: Coincident(g11,g9)
    c: Coincident(g11,g2)
    c: DistanceY(g6,g7) = 21
    c: Radius(g7) = 22
    c: Radius(g8) = 22
    c: DistanceX(g0,g1) = 3
FEATURE [PartDesign::Pad] Pad015
  Direction = (0,0,1)
  Length = 30
  Length2 = 10
  Profile = -> Sketch032
  ReferenceAxis = -> Sketch032 [N_Axis]
  Refine = true
  Reversed = true
  Suppressed = false
  Type = 0
FEATURE [PartDesign::Chamfer] Chamfer004
  Angle = 45
  Base = -> Pad015 [Edge27]
  BaseFeature = -> Pad015
  ChamferType = 0
  FlipDirection = false
  Refine = true
  Size = 2
  Size2 = 1
  SupportTransform = false
  Suppressed = false
  UseAllEdges = false
FEATURE [PartDesign::Chamfer] Chamfer005
  Angle = 45
  Base = -> Chamfer004 [Edge8]
  BaseFeature = -> Chamfer004
  ChamferType = 0
  FlipDirection = false
  Refine = true
  Size = 2
  Size2 = 1
  SupportTransform = false
  Suppressed = false
  UseAllEdges = false
FEATURE [PartDesign::Fillet] Fillet
  Base = -> Chamfer005 [Edge1]
  BaseFeature = -> Chamfer005
  Radius = 1
  Refine = true
  SupportTransform = false
  Suppressed = false
  UseAllEdges = false
FEATURE [Sketcher::SketchObject] Sketch033
  ArcFitTolerance = 1e-06
  AttachmentSupport = -> [Fillet]
  FullyConstrained = false
  MakeInternals = false
  MapMode = 5
  Placement = pos=(24,0,0) rot=(0.57735,0.57735,0.57735;2.0944rad)
  sketch-geometry (8):
    g0: ArcOfCircle CenterX=0 CenterY=7.65034 CenterZ=0 NormalX=0 NormalY=0 NormalZ=1 AngleXU=0 Radius=1.75 StartAngle=0 EndAngle=3.14159
    g1: ArcOfCircle CenterX=1e-16 CenterY=-3.43993 CenterZ=0 NormalX=0 NormalY=0 NormalZ=1 AngleXU=0 Radius=1.75 StartAngle=3.14159 EndAngle=6.28319
    g2: LineSegment StartX=1.75 StartY=7.65034 StartZ=0 EndX=1.75 EndY=-3.43993 EndZ=0
    g3: LineSegment StartX=-1.75 StartY=7.65034 StartZ=0 EndX=-1.75 EndY=-3.43993 EndZ=0
    g4: ArcOfCircle CenterX=0 CenterY=-38.1971 CenterZ=0 NormalX=0 NormalY=0 NormalZ=1 AngleXU=0 Radius=1.75 StartAngle=3.14159 EndAngle=6.28319
    g5: ArcOfCircle CenterX=0 CenterY=-25.9635 CenterZ=0 NormalX=0 NormalY=0 NormalZ=1 AngleXU=0 Radius=1.75 StartAngle=0 EndAngle=3.14159
    g6: LineSegment StartX=-1.75 StartY=-38.1971 StartZ=0 EndX=-1.75 EndY=-25.9635 EndZ=0
    g7: LineSegment StartX=1.75 StartY=-38.1971 StartZ=0 EndX=1.75 EndY=-25.9635 EndZ=0
  constraints (16):
    c: Tangent(g0,g2) = 1.5708
    c: Tangent(g0,g3) = -1.5708
    c: Tangent(g1,g2) = 1.5708
    c: Tangent(g1,g3) = -1.5708
    c: Equal(g0,g1)
    c: Vertical(g3)
    c: PointOnObject(g0,g-2)
    c: Tangent(g4,g6) = 1.5708
    c: Tangent(g4,g7) = -1.5708
    c: Tangent(g5,g6) = 1.5708
    c: Tangent(g5,g7) = -1.5708
    c: Equal(g4,g5)
    c: Vertical(g7)
    c: PointOnObject(g4,g-2)
    c: Equal(g1,g5)
    c: Diameter(g1) = 3.5
FEATURE [PartDesign::Pocket] Pocket009
  BaseFeature = -> Fillet
  Direction = (-1,0,0)
  Length = 5
  Length2 = 5
  Profile = -> Sketch033
  ReferenceAxis = -> Sketch033 [N_Axis]
  Refine = true
  Suppressed = false
  Type = 0
FEATURE [Sketcher::SketchObject] Sketch034
  ArcFitTolerance = 1e-06
  AttachmentSupport = -> [Pocket009]
  ExternalGeometry = -> [Pocket009]
  FullyConstrained = true
  MakeInternals = false
  MapMode = 5
  Placement = pos=(0,-24.23,0) rot=(1,0,0;1.5708rad)
  sketch-geometry (2):
    g0: Circle CenterX=0 CenterY=-3 CenterZ=0 NormalX=0 NormalY=0 NormalZ=1 AngleXU=0 Radius=1.5
    g1: Circle CenterX=0 CenterY=-27 CenterZ=0 NormalX=0 NormalY=0 NormalZ=1 AngleXU=0 Radius=1.5
  constraints (6):
    c: PointOnObject(g0,g-2)
    c: PointOnObject(g1,g-2)
    c: Equal(g0,g1)
    c: Diameter(g0) = 3
    c: DistanceY(g0,g-1) = 3
    c: DistanceY(g-3,g1) = 3
FEATURE [PartDesign::Pocket] Pocket010
  BaseFeature = -> Pocket009
  Direction = (0,1,-2e-16)
  Length = 5
  Length2 = 5
  Profile = -> Sketch034
  ReferenceAxis = -> Sketch034 [N_Axis]
  Refine = true
  Suppressed = false
  Type = 1
FEATURE [PartDesign::Chamfer] Chamfer006
  Angle = 45
  Base = -> Pocket010 [Edge45]
  BaseFeature = -> Pocket010
  ChamferType = 0
  FlipDirection = false
  Refine = true
  Size = 1
  Size2 = 1
  SupportTransform = false
  Suppressed = false
  UseAllEdges = false
FEATURE [PartDesign::Chamfer] Chamfer007
  Angle = 45
  Base = -> Chamfer006 [Edge52]
  BaseFeature = -> Chamfer006
  ChamferType = 0
  FlipDirection = false
  Refine = true
  Size = 1
  Size2 = 1
  SupportTransform = false
  Suppressed = false
  UseAllEdges = false
FEATURE [Sketcher::SketchObject] Sketch035
  ArcFitTolerance = 1e-06
  AttachmentSupport = -> [Chamfer007]
  FullyConstrained = false
  MakeInternals = false
  MapMode = 5
  Placement = pos=(0,-24.23,0) rot=(1,0,0;1.5708rad)
  sketch-geometry (8):
    g0: ArcOfCircle CenterX=0 CenterY=-3.21751 CenterZ=0 NormalX=0 NormalY=0 NormalZ=1 AngleXU=0 Radius=2.75 StartAngle=3.14159 EndAngle=6.28319
    g1: ArcOfCircle CenterX=-1e-16 CenterY=4.88197 CenterZ=0 NormalX=0 NormalY=0 NormalZ=1 AngleXU=0 Radius=2.75 StartAngle=2e-16 EndAngle=3.14159
    g2: LineSegment StartX=-2.75 StartY=-3.21751 StartZ=0 EndX=-2.75 EndY=4.88197 EndZ=0
    g3: LineSegment StartX=2.75 StartY=-3.21751 StartZ=0 EndX=2.75 EndY=4.88197 EndZ=0
    g4: ArcOfCircle CenterX=0 CenterY=-27.097 CenterZ=0 NormalX=0 NormalY=0 NormalZ=1 AngleXU=0 Radius=2.75 StartAngle=3e-16 EndAngle=3.14159
    g5: ArcOfCircle CenterX=1e-16 CenterY=-34.4983 CenterZ=0 NormalX=0 NormalY=0 NormalZ=1 AngleXU=0 Radius=2.75 StartAngle=3.14159 EndAngle=6.28319
    g6: LineSegment StartX=2.75 StartY=-27.097 StartZ=0 EndX=2.75 EndY=-34.4983 EndZ=0
    g7: LineSegment StartX=-2.75 StartY=-27.097 StartZ=0 EndX=-2.75 EndY=-34.4983 EndZ=0
  constraints (16):
    c: Tangent(g0,g2) = 1.5708
    c: Tangent(g0,g3) = -1.5708
    c: Tangent(g1,g2) = 1.5708
    c: Tangent(g1,g3) = -1.5708
    c: Equal(g0,g1)
    c: Vertical(g3)
    c: PointOnObject(g0,g-2)
    c: Tangent(g4,g6) = 1.5708
    c: Tangent(g4,g7) = -1.5708
    c: Tangent(g5,g6) = 1.5708
    c: Tangent(g5,g7) = -1.5708
    c: Equal(g4,g5)
    c: Vertical(g7)
    c: PointOnObject(g4,g-2)
    c: Equal(g0,g4)
    c: Diameter(g0) = 5.5
FEATURE [PartDesign::Pocket] Pocket011
  BaseFeature = -> Chamfer007
  Direction = (0,1,-2e-16)
  Length = 1
  Length2 = 5
  Profile = -> Sketch035
  ReferenceAxis = -> Sketch035 [N_Axis]
  Refine = true
  Suppressed = false
  Type = 0
FEATURE [Part::FeaturePython] Screw006  label="M3x10-Screw"  # WARN: FeaturePython — macro-defined, semantics opaque (R4)
  Diameter = 1
  Invert = false
  LeftHanded = false
  Length = 3
  LengthCustom = 10
  MatchOuter = false
  OffsetAngle = 0
  Placement = pos=(0,232.3,3.5) rot=(1,0,0;4.71239rad)
  Thread = false
  Type = 37
FEATURE [Part::FeaturePython] ThreadedRod  label="M3x6-ThreadedRod"  # WARN: FeaturePython — macro-defined, semantics opaque (R4)
  Diameter = 4
  DiameterCustom = 6
  Invert = false
  LeftHanded = false
  Length = 6
  MatchOuter = false
  OffsetAngle = 0
  PitchCustom = 1
  Placement = pos=(-21.3,210,3.3) rot=(0,1,0;4.71239rad)
  Thread = false
  Type = 4
FEATURE [Part::FeaturePython] Screw007  label="M3x10-Screw001"  # WARN: FeaturePython — macro-defined, semantics opaque (R4)
  Diameter = 1
  Invert = false
  LeftHanded = false
  Length = 3
  LengthCustom = 10
  MatchOuter = false
  OffsetAngle = 0
  Placement = pos=(0,232.3,-20.5) rot=(1,0,0;4.71239rad)
  Thread = false
  Type = 37
FEATURE [PartDesign::Chamfer] Chamfer008
  Angle = 45
  Base = -> Pocket011 [Edge41]
  BaseFeature = -> Pocket011
  ChamferType = 0
  FlipDirection = false
  Refine = true
  Size = 2
  Size2 = 1
  SupportTransform = false
  Suppressed = false
  UseAllEdges = false
FEATURE [PartDesign::Chamfer] Chamfer009
  Angle = 45
  Base = -> Chamfer008 [Edge65]
  BaseFeature = -> Chamfer008
  ChamferType = 0
  FlipDirection = false
  Refine = true
  Size = 2
  Size2 = 1
  SupportTransform = false
  Suppressed = false
  UseAllEdges = false
FEATURE [PartDesign::Fillet] Fillet006
  Base = -> Chamfer009 [Edge11]
  BaseFeature = -> Chamfer009
  Radius = 1
  Refine = true
  SupportTransform = false
  Suppressed = false
  UseAllEdges = false
FEATURE [Sketcher::SketchObject] Sketch036
  ArcFitTolerance = 1e-06
  AttachmentSupport = -> [Fillet006]
  ExternalGeometry = -> [Fillet006]
  FullyConstrained = false
  MakeInternals = false
  MapMode = 5
  Placement = pos=(-24,0,0) rot=(0.57735,-0.57735,-0.57735;2.0944rad)
  sketch-geometry (8):
    g0: ArcOfCircle CenterX=0 CenterY=-3 CenterZ=0 NormalX=0 NormalY=0 NormalZ=1 AngleXU=0 Radius=1.75 StartAngle=3.14159 EndAngle=6.28319
    g1: ArcOfCircle CenterX=-1e-16 CenterY=5.63802 CenterZ=0 NormalX=0 NormalY=0 NormalZ=1 AngleXU=0 Radius=1.75 StartAngle=0 EndAngle=3.14159
    g2: LineSegment StartX=-1.75 StartY=-3 StartZ=0 EndX=-1.75 EndY=5.63802 EndZ=0
    g3: LineSegment StartX=1.75 StartY=-3 StartZ=0 EndX=1.75 EndY=5.63802 EndZ=0
    g4: ArcOfCircle CenterX=0 CenterY=-27 CenterZ=0 NormalX=0 NormalY=0 NormalZ=1 AngleXU=0 Radius=1.75 StartAngle=8e-16 EndAngle=3.14159
    g5: ArcOfCircle CenterX=-1e-16 CenterY=-38.0111 CenterZ=0 NormalX=0 NormalY=0 NormalZ=1 AngleXU=0 Radius=1.75 StartAngle=3.14159 EndAngle=6.28319
    g6: LineSegment StartX=1.75 StartY=-27 StartZ=0 EndX=1.75 EndY=-38.0111 EndZ=0
    g7: LineSegment StartX=-1.75 StartY=-27 StartZ=0 EndX=-1.75 EndY=-38.0111 EndZ=0
  constraints (18):
    c: Tangent(g0,g2) = 1.5708
    c: Tangent(g0,g3) = -1.5708
    c: Tangent(g1,g2) = 1.5708
    c: Tangent(g1,g3) = -1.5708
    c: Equal(g0,g1)
    c: Vertical(g3)
    c: PointOnObject(g0,g-2)
    c: Tangent(g4,g6) = 1.5708
    c: Tangent(g4,g7) = -1.5708
    c: Tangent(g5,g6) = 1.5708
    c: Tangent(g5,g7) = -1.5708
    c: Equal(g4,g5)
    c: Vertical(g7)
    c: PointOnObject(g4,g-2)
    c: DistanceY(g0,g-1) = 3
    c: DistanceY(g-3,g4) = 3
    c: Equal(g0,g4)
    c: Diameter(g0) = 3.5
FEATURE [PartDesign::Pocket] Pocket012
  BaseFeature = -> Fillet006
  Direction = (1,0,0)
  Length = 5
  Length2 = 5
  Profile = -> Sketch036
  ReferenceAxis = -> Sketch036 [N_Axis]
  Refine = true
  Suppressed = false
  Type = 1
FEATURE [Sketcher::SketchObject] Sketch037
  ArcFitTolerance = 1e-06
  AttachmentSupport = -> [Pocket012]
  ExternalGeometry = -> [Pocket012]
  FullyConstrained = false
  MakeInternals = false
  MapMode = 5
  Placement = pos=(0,9.81302,0) rot=(0,0.707107,0.707107;3.14159rad)
  sketch-geometry (16):
    g0: LineSegment StartX=-21.5705 StartY=-24 StartZ=0 EndX=-19.6628 EndY=-24 EndZ=0
    g1: LineSegment StartX=-19.6628 StartY=-24 StartZ=0 EndX=-19.6628 EndY=-22.1244 EndZ=0
    g2: LineSegment StartX=-19.6628 StartY=-22.1244 StartZ=0 EndX=-21.5705 EndY=-22.1244 EndZ=0
    g3: LineSegment StartX=-21.5705 StartY=-22.1244 StartZ=0 EndX=-21.5705 EndY=-24 EndZ=0
    g4: LineSegment StartX=-21.4919 StartY=-6 StartZ=0 EndX=-21.4919 EndY=-8 EndZ=0
    g5: LineSegment StartX=-21.4919 StartY=-8 StartZ=0 EndX=-19.6628 EndY=-8 EndZ=0
    g6: LineSegment StartX=-19.6628 StartY=-8 StartZ=0 EndX=-19.6628 EndY=-6 EndZ=0
    g7: LineSegment StartX=-19.6628 StartY=-6 StartZ=0 EndX=-21.4919 EndY=-6 EndZ=0
    g8: LineSegment StartX=19.6628 StartY=-6 StartZ=0 EndX=19.6628 EndY=-8 EndZ=0
    g9: LineSegment StartX=19.6628 StartY=-8 StartZ=0 EndX=21.3888 EndY=-8 EndZ=0
    g10: LineSegment StartX=21.3888 StartY=-8 StartZ=0 EndX=21.3888 EndY=-6 EndZ=0
    g11: LineSegment StartX=21.3888 StartY=-6 StartZ=0 EndX=19.6628 EndY=-6 EndZ=0
    g12: LineSegment StartX=19.6628 StartY=-22.1244 StartZ=0 EndX=19.6628 EndY=-24 EndZ=0
    g13: LineSegment StartX=19.6628 StartY=-24 StartZ=0 EndX=21.5063 EndY=-24 EndZ=0
    g14: LineSegment StartX=21.5063 StartY=-24 StartZ=0 EndX=21.5063 EndY=-22.1244 EndZ=0
    g15: LineSegment StartX=21.5063 StartY=-22.1244 StartZ=0 EndX=19.6628 EndY=-22.1244 EndZ=0
  constraints (41):
    c: Coincident(g0,g1)
    c: Coincident(g1,g2)
    c: Coincident(g2,g3)
    c: Coincident(g3,g0)
    c: Horizontal(g0)
    c: Horizontal(g2)
    c: Vertical(g1)
    c: Vertical(g3)
    c: Coincident(g4,g5)
    c: Coincident(g5,g6)
    c: Coincident(g6,g7)
    c: Coincident(g7,g4)
    c: Vertical(g4)
    c: Vertical(g6)
    c: Horizontal(g5)
    c: Horizontal(g7)
    c: Coincident(g8,g9)
    c: Coincident(g9,g10)
    c: Coincident(g10,g11)
    c: Coincident(g11,g8)
    c: Vertical(g8)
    c: Vertical(g10)
    c: Horizontal(g9)
    c: Horizontal(g11)
    c: Coincident(g12,g13)
    c: Coincident(g13,g14)
    c: Coincident(g14,g15)
    c: Coincident(g15,g12)
    c: Vertical(g12)
    c: Vertical(g14)
    c: Horizontal(g13)
    c: Horizontal(g15)
    c: Horizontal(g1,g12)
    c: Symmetric(g8,g5,g-2)
    c: Vertical(g5,g1)
    c: Vertical(g8,g12)
    c: DistanceY(g-3,g0) = 6
    c: Horizontal(g0,g12)
    c: Horizontal(g6,g8)
    c: DistanceY(g6,g-1) = 6
    c: DistanceY(g5,g6) = 2
FEATURE [PartDesign::Pad] Pad016
  BaseFeature = -> Pocket012
  Direction = (0,1,-2e-16)
  Length = 20
  Length2 = 10
  Profile = -> Sketch037
  ReferenceAxis = -> Sketch037 [N_Axis]
  Refine = true
  Reversed = true
  Suppressed = false
  Type = 0
FEATURE [PartDesign::Body] Body017  label="TIP-01"
  AllowCompound = false
  Group = -> [Sketch032,Pad015,Chamfer004,Chamfer005,Fillet,Sketch033,Pocket009,Sketch034,Pocket010,Chamfer006,Chamfer007,Sketch035,Pocket011,Chamfer008,Chamfer009,Fillet006,Sketch036,Pocket012,Sketch037,Pad016]
  Origin = -> Origin025
  Placement = pos=(0,210,6.5) rot=(0,0,1;3.14159rad)
  Tip = -> Pad016
FEATURE [Sketcher::SketchObject] Sketch
  ArcFitTolerance = 1e-06
  AttachmentSupport = -> [Pocket005]
  FullyConstrained = false
  MakeInternals = false
  MapMode = 5
  Placement = pos=(0,0,6) rot=(0,0,1;0rad)
  sketch-geometry (38):
    g0: LineSegment [constr] StartX=-12 StartY=121.792 StartZ=0 EndX=-12 EndY=15.9918 EndZ=0
    g1: LineSegment [constr] StartX=-12 StartY=15.9918 StartZ=0 EndX=12 EndY=15.9918 EndZ=0
    g2: LineSegment [constr] StartX=12 StartY=15.9918 StartZ=0 EndX=12 EndY=121.792 EndZ=0
    g3: LineSegment [constr] StartX=12 StartY=121.792 StartZ=0 EndX=-12 EndY=121.792 EndZ=0
    g4: LineSegment [constr] StartX=-3 StartY=131.645 StartZ=0 EndX=-3 EndY=23.7908 EndZ=0
    g5: LineSegment [constr] StartX=-3 StartY=23.7908 StartZ=0 EndX=3 EndY=23.7908 EndZ=0
    g6: LineSegment [constr] StartX=3 StartY=23.7908 StartZ=0 EndX=3 EndY=131.645 EndZ=0
    g7: LineSegment [constr] StartX=3 StartY=131.645 StartZ=0 EndX=-3 EndY=131.645 EndZ=0
    g8: LineSegment StartX=9.34582 StartY=41.7755 StartZ=0 EndX=5.65418 EndY=41.7755 EndZ=0
    g9: LineSegment StartX=3 StartY=39.1214 StartZ=0 EndX=3 EndY=29.1362 EndZ=0
    g10: LineSegment StartX=4.14183 StartY=26.9551 StartZ=0 EndX=7.83348 EndY=24.3954 EndZ=0
    g11: LineSegment StartX=12 StartY=26.5766 StartZ=0 EndX=12 EndY=39.1214 EndZ=0
    g12: ArcOfCircle CenterX=9.34582 CenterY=39.1214 CenterZ=0 NormalX=0 NormalY=0 NormalZ=1 AngleXU=0 Radius=2.65418 StartAngle=-9e-16 EndAngle=1.5708
    g13: ArcOfCircle CenterX=5.65418 CenterY=39.1214 CenterZ=0 NormalX=0 NormalY=0 NormalZ=1 AngleXU=0 Radius=2.65418 StartAngle=1.5708 EndAngle=3.14159
    g14: ArcOfCircle CenterX=5.65418 CenterY=29.1362 CenterZ=0 NormalX=0 NormalY=0 NormalZ=1 AngleXU=0 Radius=2.65418 StartAngle=3.14159 EndAngle=4.10613
    g15: ArcOfCircle CenterX=9.34582 CenterY=26.5766 CenterZ=0 NormalX=0 NormalY=0 NormalZ=1 AngleXU=0 Radius=2.65418 StartAngle=4.10613 EndAngle=6.28319
    g16: GeomPoint [constr] X=12 Y=41.7755 Z=0
    g17: GeomPoint [constr] X=3 Y=27.7468 Z=0
    g18: LineSegment StartX=12 StartY=50.4297 StartZ=0 EndX=12 EndY=105.062 EndZ=0
    g19: LineSegment StartX=9.34582 StartY=107.716 StartZ=0 EndX=5.65418 EndY=107.716 EndZ=0
    g20: LineSegment StartX=3 StartY=105.062 StartZ=0 EndX=3 EndY=50.4297 EndZ=0
    g21: LineSegment StartX=5.65418 StartY=47.7755 StartZ=0 EndX=9.34582 EndY=47.7755 EndZ=0
    g22: ArcOfCircle CenterX=9.34582 CenterY=50.4297 CenterZ=0 NormalX=0 NormalY=0 NormalZ=1 AngleXU=0 Radius=2.65418 StartAngle=4.71239 EndAngle=6.28319
    g23: ArcOfCircle CenterX=9.34582 CenterY=105.062 CenterZ=0 NormalX=0 NormalY=0 NormalZ=1 AngleXU=0 Radius=2.65418 StartAngle=3e-16 EndAngle=1.5708
    g24: ArcOfCircle CenterX=5.65418 CenterY=105.062 CenterZ=0 NormalX=0 NormalY=0 NormalZ=1 AngleXU=0 Radius=2.65418 StartAngle=1.5708 EndAngle=3.14159
    g25: ArcOfCircle CenterX=5.65418 CenterY=50.4297 CenterZ=0 NormalX=0 NormalY=0 NormalZ=1 AngleXU=0 Radius=2.65418 StartAngle=3.14159 EndAngle=4.71239
    g26: GeomPoint [constr] X=12 Y=47.7755 Z=0
    g27: GeomPoint [constr] X=3 Y=107.716 Z=0
    g28: LineSegment StartX=3 StartY=121.792 StartZ=0 EndX=3 EndY=115.825 EndZ=0
    g29: LineSegment StartX=5.10848 StartY=113.716 StartZ=0 EndX=9.89152 EndY=113.716 EndZ=0
    g30: LineSegment StartX=12 StartY=115.825 StartZ=0 EndX=12 EndY=123.92 EndZ=0
    g31: LineSegment StartX=9.03468 StartY=125.846 StartZ=0 EndX=4.25164 EndY=123.719 EndZ=0
    g32: ArcOfCircle CenterX=5.10848 CenterY=121.792 CenterZ=0 NormalX=0 NormalY=0 NormalZ=1 AngleXU=0 Radius=2.10848 StartAngle=1.98928 EndAngle=3.14159
    g33: ArcOfCircle CenterX=5.10848 CenterY=115.825 CenterZ=0 NormalX=0 NormalY=0 NormalZ=1 AngleXU=0 Radius=2.10848 StartAngle=3.14159 EndAngle=4.71239
    g34: ArcOfCircle CenterX=9.89152 CenterY=115.825 CenterZ=0 NormalX=0 NormalY=0 NormalZ=1 AngleXU=0 Radius=2.10848 StartAngle=4.71239 EndAngle=6.28319
    g35: ArcOfCircle CenterX=9.89152 CenterY=123.92 CenterZ=0 NormalX=0 NormalY=0 NormalZ=1 AngleXU=0 Radius=2.10848 StartAngle=-1.8e-15 EndAngle=1.98928
    g36: GeomPoint [constr] X=3 Y=123.162 Z=0
    g37: GeomPoint [constr] X=12 Y=113.716 Z=0
  constraints (83):
    c: Coincident(g0,g1)
    c: Coincident(g1,g2)
    c: Coincident(g2,g3)
    c: Coincident(g3,g0)
    c: Vertical(g0)
    c: Vertical(g2)
    c: Horizontal(g1)
    c: Coincident(g4,g5)
    c: Coincident(g5,g6)
    c: Coincident(g6,g7)
    c: Coincident(g7,g4)
    c: Vertical(g4)
    c: Vertical(g6)
    c: Horizontal(g5)
    c: Symmetric(g4,g6,g-2)
    c: Symmetric(g0,g2,g-2)
    c: DistanceX(g0,g2) = 24
    c: DistanceX(g4,g6) = 6
    c: Tangent(g8,g12) = -1.5708
    c: Tangent(g8,g13) = -1.5708
    c: Tangent(g9,g13) = -1.5708
    c: Tangent(g9,g14) = -1.5708
    c: Tangent(g10,g14) = -1.5708
    c: Tangent(g10,g15) = -1.5708
    c: Tangent(g11,g15) = -1.5708
    c: Tangent(g11,g12) = -1.5708
    c: Horizontal(g8)
    c: Vertical(g9)
    c: Vertical(g11)
    c: Equal(g12,g13)
    c: Equal(g13,g14)
    c: Equal(g14,g15)
    c: PointOnObject(g16,g8)
    c: PointOnObject(g16,g11)
    c: PointOnObject(g17,g9)
    c: PointOnObject(g17,g10)
    c: PointOnObject(g16,g2)
    c: PointOnObject(g17,g6)
    c: Tangent(g18,g22) = -1.5708
    c: Tangent(g18,g23) = -1.5708
    c: Tangent(g19,g23) = -1.5708
    c: Tangent(g19,g24) = -1.5708
    c: Tangent(g20,g24) = -1.5708
    c: Tangent(g20,g25) = -1.5708
    c: Tangent(g21,g25) = -1.5708
    c: Tangent(g21,g22) = -1.5708
    c: Vertical(g18)
    c: Vertical(g20)
    c: Horizontal(g19)
    c: Horizontal(g21)
    c: Equal(g22,g23)
    c: Equal(g23,g24)
    c: Equal(g24,g25)
    c: PointOnObject(g26,g18)
    c: PointOnObject(g26,g21)
    c: PointOnObject(g27,g19)
    c: PointOnObject(g27,g20)
    c: PointOnObject(g26,g2)
    c: PointOnObject(g27,g6)
    c: Tangent(g28,g32) = -1.5708
    c: Tangent(g28,g33) = -1.5708
    c: Tangent(g29,g33) = -1.5708
    c: Tangent(g29,g34) = -1.5708
    c: Tangent(g30,g34) = -1.5708
    c: Tangent(g30,g35) = -1.5708
    c: Tangent(g31,g35) = -1.5708
    c: Tangent(g31,g32) = -1.5708
    c: Vertical(g28)
    c: Vertical(g30)
    c: Horizontal(g29)
    c: Equal(g32,g33)
    c: Equal(g33,g34)
    c: Equal(g34,g35)
    c: PointOnObject(g36,g28)
    c: PointOnObject(g36,g31)
    c: PointOnObject(g37,g29)
    c: PointOnObject(g37,g30)
    c: PointOnObject(g36,g6)
    c: PointOnObject(g37,g2)
    c: PointOnObject(g32,g3)
    c: DistanceY(g16,g26) = 6
    c: Vertical(g12,g22)
    c: DistanceY(g27,g37) = 6
FEATURE [PartDesign::Pocket] Pocket
  BaseFeature = -> Pocket005
  Direction = (0,0,-1)
  Length = 5
  Length2 = 5
  Profile = -> Sketch
  ReferenceAxis = -> Sketch [N_Axis]
  Refine = true
  Suppressed = false
  Type = 1
FEATURE [PartDesign::Mirrored] Mirrored
  BaseFeature = -> Pocket
  MirrorPlane = -> Sketch [V_Axis]
  Originals = -> [Pocket]
  Refine = true
  Suppressed = false
  TransformMode = 0
FEATURE [Sketcher::SketchObject] Sketch049
  ArcFitTolerance = 1e-06
  AttachmentSupport = -> [XY_Plane028]
  FullyConstrained = false
  MakeInternals = false
  MapMode = 5
  sketch-geometry (18):
    g0: LineSegment StartX=-24 StartY=-0.947992 StartZ=0 EndX=-24 EndY=-35.9722 EndZ=0
    g1: LineSegment StartX=24 StartY=-36.0369 StartZ=0 EndX=24 EndY=-0.947992 EndZ=0
    g2: LineSegment StartX=-20.488 StartY=-39.9173 StartZ=0 EndX=-0.225681 EndY=-42.2788 EndZ=0
    g3: LineSegment StartX=0.225681 StartY=-42.2788 StartZ=0 EndX=20.5523 EndY=-39.9098 EndZ=0
    g4: LineSegment [constr] StartX=-32.8278 StartY=17 StartZ=0 EndX=40.8293 EndY=17 EndZ=0
    g5: ArcOfCircle CenterX=0 CenterY=12.1248 CenterZ=0 NormalX=0 NormalY=0 NormalZ=1 AngleXU=0 Radius=17.2476 StartAngle=0.54794 EndAngle=2.59365
    g6: LineSegment StartX=-23.6186 StartY=0.867874 StartZ=0 EndX=-14.7225 EndY=21.1096 EndZ=0
    g7: LineSegment StartX=23.6186 StartY=0.867874 StartZ=0 EndX=14.7225 EndY=21.1096 EndZ=0
    g8: ArcOfCircle CenterX=20.1009 CenterY=-36.0369 CenterZ=0 NormalX=0 NormalY=0 NormalZ=1 AngleXU=0 Radius=3.89907 StartAngle=4.82841 EndAngle=6.28319
    g9: GeomPoint [constr] X=24 Y=-39.508 Z=0
    g10: ArcOfCircle CenterX=-2.23e-14 CenterY=-40.3423 CenterZ=0 NormalX=0 NormalY=0 NormalZ=1 AngleXU=0 Radius=1.94952 StartAngle=4.59637 EndAngle=4.82841
    g11: GeomPoint [constr] X=0 Y=-42.3051 Z=0
    g12: ArcOfCircle CenterX=-20.0282 CenterY=-35.9722 CenterZ=0 NormalX=0 NormalY=0 NormalZ=1 AngleXU=0 Radius=3.97177 StartAngle=3.14159 EndAngle=4.59637
    g13: GeomPoint [constr] X=-24 Y=-39.508 Z=0
    g14: ArcOfCircle CenterX=19.4868 CenterY=-0.947992 CenterZ=0 NormalX=0 NormalY=0 NormalZ=1 AngleXU=0 Radius=4.51318 StartAngle=0 EndAngle=0.41408
    g15: GeomPoint [constr] X=24 Y=0 Z=0
    g16: ArcOfCircle CenterX=-19.4868 CenterY=-0.947992 CenterZ=0 NormalX=0 NormalY=0 NormalZ=1 AngleXU=0 Radius=4.51318 StartAngle=2.72751 EndAngle=3.14159
    g17: GeomPoint [constr] X=-24 Y=0 Z=0
  constraints (33):
    c: Vertical(g0)
    c: Vertical(g1)
    c: Distance(g13,g9) = 48
    c: Symmetric(g13,g9,g-2)
    c: PointOnObject(g11,g-2)
    c: PointOnObject(g15,g-1)
    c: PointOnObject(g17,g-1)
    c: Horizontal(g4)
    c: DistanceY(g15,g4) = 17
    c: PointOnObject(g5,g-2)
    c: Coincident(g6,g5)
    c: Coincident(g7,g5)
    c: Horizontal(g5,g5)
    c: PointOnObject(g9,g1)
    c: PointOnObject(g9,g3)
    c: Tangent(g1,g8) = -1.5708
    c: Tangent(g3,g8) = -1.5708
    c: PointOnObject(g11,g2)
    c: PointOnObject(g11,g3)
    c: Tangent(g2,g10) = -1.5708
    c: Tangent(g3,g10) = -1.5708
    c: PointOnObject(g13,g0)
    c: PointOnObject(g13,g2)
    c: Tangent(g0,g12) = -1.5708
    c: Tangent(g2,g12) = -1.5708
    c: PointOnObject(g15,g1)
    c: PointOnObject(g15,g7)
    c: Tangent(g1,g14) = -1.5708
    c: Tangent(g7,g14) = -1.5708
    c: PointOnObject(g17,g0)
    c: PointOnObject(g17,g6)
    c: Tangent(g0,g16) = -1.5708
    c: Tangent(g6,g16) = 1.5708
FEATURE [PartDesign::Pad] Pad
  Direction = (0,0,1)
  Length = 38
  Length2 = 10
  Profile = -> Sketch049
  ReferenceAxis = -> Sketch049 [N_Axis]
  Refine = true
  Suppressed = false
  Type = 0
FEATURE [Sketcher::SketchObject] Sketch050
  ArcFitTolerance = 1e-06
  FullyConstrained = false
  MakeInternals = false
  MapMode = 5
  Placement = pos=(0,0,0) rot=(1,0,0;3.14159rad)
  sketch-geometry (12):
    g0: LineSegment StartX=-10.3327 StartY=38.4506 StartZ=0 EndX=10.8532 EndY=38.4506 EndZ=0
    g1: LineSegment StartX=10.8532 StartY=38.4506 StartZ=0 EndX=19.6538 EndY=36.6223 EndZ=0
    g2: LineSegment StartX=20.9251 StartY=35.0598 StartZ=0 EndX=20.9251 EndY=0 EndZ=0
    g3: LineSegment StartX=20.9251 StartY=0 StartZ=0 EndX=11.6327 EndY=-19.3419 EndZ=0
    g4: LineSegment StartX=-10.3327 StartY=38.4506 StartZ=0 EndX=-19.5607 EndY=36.8556 EndZ=0
    g5: LineSegment StartX=-20.9251 StartY=35.2351 StartZ=0 EndX=-20.9251 EndY=0 EndZ=0
    g6: LineSegment StartX=-20.9251 StartY=0 StartZ=0 EndX=-11.1095 EndY=-19.8375 EndZ=0
    g7: ArcOfCircle CenterX=0 CenterY=-7.58309 CenterZ=0 NormalX=0 NormalY=0 NormalZ=1 AngleXU=0 Radius=16.5406 StartAngle=3.97596 EndAngle=5.4924
    g8: ArcOfCircle CenterX=19.3292 CenterY=35.0598 CenterZ=0 NormalX=0 NormalY=0 NormalZ=1 AngleXU=0 Radius=1.59591 StartAngle=0 EndAngle=1.36596
    g9: GeomPoint [constr] X=20.9251 Y=36.3582 Z=0
    g10: ArcOfCircle CenterX=-19.2805 CenterY=35.2351 CenterZ=0 NormalX=0 NormalY=0 NormalZ=1 AngleXU=0 Radius=1.64458 StartAngle=1.74195 EndAngle=3.14159
    g11: GeomPoint [constr] X=-20.9251 Y=36.6198 Z=0
  constraints (20):
    c: Horizontal(g0)
    c: Coincident(g0,g1)
    c: PointOnObject(g2,g-1)
    c: Vertical(g2)
    c: Coincident(g2,g3)
    c: Coincident(g0,g4)
    c: Vertical(g5)
    c: Coincident(g5,g6)
    c: PointOnObject(g7,g-2)
    c: Coincident(g7,g6)
    c: Coincident(g7,g3)
    c: Symmetric(g5,g2,g-2)
    c: PointOnObject(g9,g1)
    c: PointOnObject(g9,g2)
    c: Tangent(g1,g8) = 1.5708
    c: Tangent(g2,g8) = 1.5708
    c: PointOnObject(g11,g4)
    c: PointOnObject(g11,g5)
    c: Tangent(g4,g10) = -1.5708
    c: Tangent(g5,g10) = -1.5708
FEATURE [PartDesign::Pocket] Pocket021
  BaseFeature = -> Pad
  Direction = (0,0,1)
  Length = 35
  Length2 = 5
  Profile = -> Sketch050
  ReferenceAxis = -> Sketch050 [N_Axis]
  Refine = true
  Suppressed = false
  Type = 0
FEATURE [Sketcher::SketchObject] Sketch051
  ArcFitTolerance = 1e-06
  AttachmentSupport = -> [XY_Plane029]
  FullyConstrained = false
  MakeInternals = false
  MapMode = 5
  sketch-geometry (6):
    g0: LineSegment StartX=-24 StartY=0 StartZ=0 EndX=-24 EndY=-40.6558 EndZ=0
    g1: LineSegment StartX=-24 StartY=-40.6558 StartZ=0 EndX=24 EndY=-40.6558 EndZ=0
    g2: LineSegment StartX=24 StartY=-40.6558 StartZ=0 EndX=24 EndY=0 EndZ=0
    g3: ArcOfCircle CenterX=0 CenterY=13.0189 CenterZ=0 NormalX=0 NormalY=0 NormalZ=1 AngleXU=0 Radius=16.3421 StartAngle=0.4465 EndAngle=2.69509
    g4: LineSegment StartX=-24 StartY=0 StartZ=0 EndX=-14.74 EndY=20.0756 EndZ=0
    g5: LineSegment StartX=24 StartY=0 StartZ=0 EndX=14.74 EndY=20.0756 EndZ=0
  constraints (15):
    c: Coincident(g0,g1)
    c: Coincident(g1,g2)
    c: Vertical(g0)
    c: Vertical(g2)
    c: Symmetric(g0,g1,g-2)
    c: DistanceX(g0,g1) = 48
    c: PointOnObject(g3,g-2)
    c: Coincident(g4,g0)
    c: Coincident(g4,g3)
    c: PointOnObject(g0,g-1)
    c: PointOnObject(g2,g-1)
    c: Coincident(g5,g2)
    c: Coincident(g5,g3)
    c: Horizontal(g3,g3)
    c: DistanceX(g3,g3) = 29.48
FEATURE [PartDesign::Pad] Pad020
  Direction = (0,0,1)
  Length = 35
  Length2 = 10
  Profile = -> Sketch051
  ReferenceAxis = -> Sketch051 [N_Axis]
  Refine = true
  Reversed = true
  Suppressed = false
  Type = 0
FEATURE [PartDesign::Fillet] Fillet011
  Base = -> Pad020 [Edge2,Edge5]
  BaseFeature = -> Pad020
  Radius = 4
  Refine = true
  SupportTransform = false
  Suppressed = false
  UseAllEdges = false
FEATURE [PartDesign::Body] Body020  label="TIP HEAD"
  AllowCompound = false
  Group = -> [Sketch051,Pad020,Fillet011]
  Origin = -> Origin029
  Placement = pos=(0,170,33.3) rot=(0,0,1;0rad)
  Tip = -> Fillet011
FEATURE [Sketcher::SketchObject] Sketch052
  ArcFitTolerance = 1e-06
  AttachmentSupport = -> [Pocket021]
  FullyConstrained = false
  MakeInternals = false
  MapMode = 5
  Placement = pos=(0,0,38) rot=(0,0,1;0rad)
  sketch-geometry (9):
    g0: LineSegment [constr] StartX=-14.6866 StartY=-10 StartZ=0 EndX=15.3134 EndY=-10 EndZ=0
    g1: ArcOfCircle CenterX=15.3134 CenterY=-10 CenterZ=0 NormalX=0 NormalY=0 NormalZ=1 AngleXU=0 Radius=4 StartAngle=1.60852 EndAngle=4.72314
    g2: ArcOfCircle CenterX=-14.6866 CenterY=-10 CenterZ=0 NormalX=0 NormalY=0 NormalZ=1 AngleXU=0 Radius=4 StartAngle=4.72675 EndAngle=7.88654
    g3: LineSegment StartX=-14.8168 StartY=-6.00212 StartZ=0 EndX=-22.1022 EndY=-6.00212 EndZ=0
    g4: LineSegment StartX=-22.1022 StartY=-6.00212 StartZ=0 EndX=-22.1022 EndY=-13.9996 EndZ=0
    g5: LineSegment StartX=-14.6291 StartY=-13.9996 StartZ=0 EndX=-22.1022 EndY=-13.9996 EndZ=0
    g6: LineSegment StartX=15.1626 StartY=-6.00285 StartZ=0 EndX=22.1687 EndY=-6.00285 EndZ=0
    g7: LineSegment StartX=22.1687 StartY=-6.00285 StartZ=0 EndX=22.1687 EndY=-13.9998 EndZ=0
    g8: LineSegment StartX=22.1687 StartY=-13.9998 StartZ=0 EndX=15.3564 EndY=-13.9998 EndZ=0
  constraints (21):
    c: Horizontal(g0)
    c: DistanceX(g0,g0) = 30
    c: DistanceY(g0,g-1) = 10
    c: Coincident(g1,g0)
    c: Coincident(g2,g0)
    c: Coincident(g3,g2)
    c: Coincident(g4,g3)
    c: Vertical(g4)
    c: Coincident(g5,g2)
    c: Coincident(g5,g4)
    c: Horizontal(g5)
    c: Horizontal(g3)
    c: Equal(g2,g1)
    c: Diameter(g2) = 8
    c: Coincident(g6,g1)
    c: Horizontal(g6)
    c: Coincident(g7,g6)
    c: Vertical(g7)
    c: Coincident(g8,g7)
    c: Coincident(g8,g1)
    c: Horizontal(g8)
FEATURE [PartDesign::Pad] Pad021
  BaseFeature = -> Pocket021
  Direction = (0,0,1)
  Length = 37
  Length2 = 10
  Profile = -> Sketch052
  ReferenceAxis = -> Sketch052 [N_Axis]
  Refine = true
  Reversed = true
  Suppressed = false
  Type = 0
FEATURE [Sketcher::SketchObject] Sketch053
  ArcFitTolerance = 1e-06
  AttachmentSupport = -> [Pad021]
  FullyConstrained = true
  MakeInternals = false
  MapMode = 5
  Placement = pos=(0,0,38) rot=(0,0,1;0rad)
  sketch-geometry (3):
    g0: LineSegment [constr] StartX=-15 StartY=-10 StartZ=0 EndX=15 EndY=-10 EndZ=0
    g1: Circle CenterX=-15 CenterY=-10 CenterZ=0 NormalX=0 NormalY=0 NormalZ=1 AngleXU=0 Radius=1.55
    g2: Circle CenterX=15 CenterY=-10 CenterZ=0 NormalX=0 NormalY=0 NormalZ=1 AngleXU=0 Radius=1.55
  constraints (7):
    c: DistanceX(g0,g0) = 30
    c: Symmetric(g0,g0,g-2)
    c: DistanceY(g0,g-1) = 10
    c: Coincident(g1,g0)
    c: Coincident(g2,g0)
    c: Equal(g1,g2)
    c: Diameter(g1) = 3.1
FEATURE [PartDesign::Pocket] Pocket022
  BaseFeature = -> Pad021
  Direction = (0,0,-1)
  Length = 5
  Length2 = 5
  Profile = -> Sketch053
  ReferenceAxis = -> Sketch053 [N_Axis]
  Refine = true
  Suppressed = false
  Type = 1
FEATURE [Sketcher::SketchObject] Sketch054
  ArcFitTolerance = 1e-06
  AttachmentSupport = -> [Pocket022]
  FullyConstrained = true
  MakeInternals = false
  MapMode = 5
  Placement = pos=(0,0,38) rot=(0,0,1;0rad)
  sketch-geometry (3):
    g0: LineSegment [constr] StartX=-15 StartY=-10 StartZ=0 EndX=15 EndY=-10 EndZ=0
    g1: Circle CenterX=-15 CenterY=-10 CenterZ=0 NormalX=0 NormalY=0 NormalZ=1 AngleXU=0 Radius=2.75
    g2: Circle CenterX=15 CenterY=-10 CenterZ=0 NormalX=0 NormalY=0 NormalZ=1 AngleXU=0 Radius=2.75
  constraints (7):
    c: Symmetric(g0,g0,g-2)
    c: DistanceX(g0,g0) = 30
    c: DistanceY(g0,g-1) = 10
    c: Coincident(g1,g0)
    c: Coincident(g2,g0)
    c: Equal(g1,g2)
    c: Diameter(g1) = 5.5
FEATURE [PartDesign::Pocket] Pocket023
  BaseFeature = -> Pocket022
  Direction = (0,0,-1)
  Length = 7
  Length2 = 5
  Profile = -> Sketch054
  ReferenceAxis = -> Sketch054 [N_Axis]
  Refine = true
  Suppressed = false
  Type = 0
FEATURE [PartDesign::Fillet] Fillet012
  Base = -> Pocket023 [Edge10,Edge31,Edge33,Edge37,Edge38,Edge36,Edge34,Edge32,Edge30,Edge7,Vertex4,Edge4]
  BaseFeature = -> Pocket023
  Radius = 8
  Refine = true
  SupportTransform = false
  Suppressed = false
  UseAllEdges = false
FEATURE [Sketcher::SketchObject] Sketch055
  ArcFitTolerance = 1e-06
  AttachmentSupport = -> [Fillet012]
  FullyConstrained = false
  MakeInternals = false
  MapMode = 5
  Placement = pos=(0,0,38) rot=(0,0,1;0rad)
  sketch-geometry (1):
    g0: Circle CenterX=0 CenterY=15.6509 CenterZ=0 NormalX=0 NormalY=0 NormalZ=1 AngleXU=0 Radius=7.59372
  constraints (1):
    c: PointOnObject(g0,g-2)
FEATURE [PartDesign::Pad] Pad022
  BaseFeature = -> Fillet012
  Direction = (0,0,1)
  Length = 10
  Length2 = 3
  Profile = -> Sketch055
  ReferenceAxis = -> Sketch055 [N_Axis]
  Refine = true
  Suppressed = false
  Type = 4
FEATURE [PartDesign::Fillet] Fillet013
  Base = -> Pad022 [Face58]
  BaseFeature = -> Pad022
  Radius = 3
  Refine = true
  SupportTransform = false
  Suppressed = false
  UseAllEdges = false
FEATURE [Sketcher::SketchObject] Sketch056
  ArcFitTolerance = 1e-06
  AttachmentSupport = -> [Fillet013]
  FullyConstrained = false
  MakeInternals = false
  MapMode = 5
  Placement = pos=(0,0,48) rot=(0,0,1;0rad)
  sketch-geometry (4):
    g0: ArcOfCircle CenterX=-3.08926 CenterY=15.7335 CenterZ=0 NormalX=0 NormalY=0 NormalZ=1 AngleXU=0 Radius=1.415 StartAngle=1.5708 EndAngle=4.71239
    g1: ArcOfCircle CenterX=3.08879 CenterY=15.7335 CenterZ=0 NormalX=0 NormalY=0 NormalZ=1 AngleXU=0 Radius=1.415 StartAngle=4.71239 EndAngle=7.85398
    g2: LineSegment StartX=-3.08926 StartY=17.1485 StartZ=0 EndX=3.08879 EndY=17.1485 EndZ=0
    g3: LineSegment StartX=-3.08926 StartY=14.3185 StartZ=0 EndX=3.08879 EndY=14.3185 EndZ=0
  constraints (7):
    c: Tangent(g0,g2) = 1.5708
    c: Tangent(g0,g3) = -1.5708
    c: Tangent(g1,g2) = 1.5708
    c: Tangent(g1,g3) = -1.5708
    c: Equal(g0,g1)
    c: Horizontal(g2)
    c: Diameter(g1) = 2.83
FEATURE [PartDesign::Pocket] Pocket024
  BaseFeature = -> Fillet013
  Direction = (0,0,-1)
  Length = 5
  Length2 = 5
  Profile = -> Sketch056
  ReferenceAxis = -> Sketch056 [N_Axis]
  Refine = true
  Suppressed = false
  Type = 1
FEATURE [PartDesign::Body] Body  label="SERVO CASE"
  AllowCompound = false
  Group = -> [Sketch049,Pad,Sketch050,Pocket021,Sketch052,Pad021,Sketch053,Pocket022,Sketch054,Pocket023,Fillet012,Sketch055,Pad022,Fillet013,Sketch056,Pocket024]
  Origin = -> Origin028
  Placement = pos=(0,170,33.9) rot=(0,0,1;0rad)
  Tip = -> Pocket024
FEATURE [Sketcher::SketchObject] Sketch057
  ArcFitTolerance = 1e-06
  AttachmentSupport = -> [XY_Plane030]
  FullyConstrained = true
  MakeInternals = false
  MapMode = 5
  sketch-geometry (2):
    g0: Circle CenterX=0 CenterY=0 CenterZ=0 NormalX=0 NormalY=0 NormalZ=1 AngleXU=0 Radius=4
    g1: Circle CenterX=0 CenterY=0 CenterZ=0 NormalX=0 NormalY=0 NormalZ=1 AngleXU=0 Radius=6
  constraints (4):
    c: Coincident(g0,g-1)
    c: Coincident(g1,g0)
    c: Diameter(g0) = 8
    c: Diameter(g1) = 12
FEATURE [PartDesign::Pad] Pad023
  Direction = (0,0,1)
  Length = 8
  Length2 = 10
  Profile = -> Sketch057
  ReferenceAxis = -> Sketch057 [N_Axis]
  Refine = true
  Suppressed = false
  Type = 0
FEATURE [PartDesign::Body] Body021  label="COLAR"
  AllowCompound = false
  Group = -> [Sketch057,Pad023]
  Origin = -> Origin030
  Placement = pos=(0,0,-33.2) rot=(0,0,1;0rad)
  Tip = -> Pad023
FEATURE [Sketcher::SketchObject] Sketch059
  ArcFitTolerance = 1e-06
  AttachmentSupport = -> [XY_Plane008]
  FullyConstrained = false
  MakeInternals = false
  MapMode = 5
  sketch-geometry (1):
    g0: Circle CenterX=0 CenterY=0 CenterZ=0 NormalX=0 NormalY=0 NormalZ=1 AngleXU=0 Radius=6.54066
  constraints (1):
    c: Coincident(g0,g-1)
FEATURE [PartDesign::Pad] Pad024
  Direction = (0,0,1)
  Length = 150
  Length2 = 10
  Profile = -> Sketch059
  ReferenceAxis = -> Sketch059 [N_Axis]
  Refine = true
  Suppressed = false
  Type = 0
FEATURE [Sketcher::SketchObject] Sketch060
  ArcFitTolerance = 1e-06
  AttachmentSupport = -> [Pad024]
  FullyConstrained = true
  MakeInternals = false
  MapMode = 5
  Placement = pos=(0,0,0) rot=(1,0,0;3.14159rad)
  sketch-geometry (1):
    g0: Circle CenterX=0 CenterY=0 CenterZ=0 NormalX=0 NormalY=0 NormalZ=1 AngleXU=0 Radius=4
  constraints (2):
    c: Coincident(g0,g-1)
    c: Diameter(g0) = 8
FEATURE [PartDesign::Pad] Pad025
  BaseFeature = -> Pad024
  Direction = (0,0,-1)
  Length = 29
  Length2 = 10
  Profile = -> Sketch060
  ReferenceAxis = -> Sketch060 [N_Axis]
  Refine = true
  Suppressed = false
  Type = 0
FEATURE [Sketcher::SketchObject] Sketch061
  ArcFitTolerance = 1e-06
  AttachmentSupport = -> [Pad025]
  FullyConstrained = false
  MakeInternals = false
  MapMode = 5
  Placement = pos=(0,0,-29) rot=(1,0,0;3.14159rad)
  sketch-geometry (8):
    g0: LineSegment StartX=-2.48846 StartY=0.239977 StartZ=0 EndX=-10.1413 EndY=0.239977 EndZ=0
    g1: LineSegment StartX=-10.1413 StartY=0.239977 StartZ=0 EndX=-10.1413 EndY=-0.260023 EndZ=0
    g2: LineSegment StartX=-10.1413 StartY=-0.260023 StartZ=0 EndX=-2.48644 EndY=-0.260023 EndZ=0
    g3: LineSegment StartX=2.48846 StartY=0.239977 StartZ=0 EndX=10.049 EndY=0.239977 EndZ=0
    g4: LineSegment StartX=10.049 StartY=0.239977 StartZ=0 EndX=10.0945 EndY=-0.260023 EndZ=0
    g5: LineSegment StartX=10.0945 StartY=-0.260023 StartZ=0 EndX=2.48644 EndY=-0.260023 EndZ=0
    g6: ArcOfCircle CenterX=0 CenterY=0 CenterZ=0 NormalX=0 NormalY=0 NormalZ=1 AngleXU=0 Radius=2.5 StartAngle=0.0961388 EndAngle=3.04545
    g7: ArcOfCircle CenterX=0 CenterY=0 CenterZ=0 NormalX=0 NormalY=0 NormalZ=1 AngleXU=0 Radius=2.5 StartAngle=3.24579 EndAngle=6.17899
  constraints (20):
    c: Horizontal(g0)
    c: Coincident(g1,g0)
    c: Vertical(g1)
    c: Coincident(g2,g1)
    c: Horizontal(g2)
    c: Horizontal(g3)
    c: Coincident(g4,g3)
    c: Coincident(g5,g4)
    c: Horizontal(g5)
    c: Coincident(g6,g-1)
    c: Coincident(g6,g3)
    c: Coincident(g6,g0)
    c: Coincident(g7,g6)
    c: Coincident(g7,g2)
    c: Coincident(g7,g5)
    c: Equal(g7,g6)
    c: Diameter(g7) = 5
    c: DistanceY(g4,g3) = 0.5
    c: Horizontal(g3,g0)
    c: Horizontal(g2,g5)
FEATURE [PartDesign::Pocket] Pocket025
  BaseFeature = -> Pad025
  Direction = (0,0,1)
  Length = 5
  Length2 = 5
  Profile = -> Sketch061
  ReferenceAxis = -> Sketch061 [N_Axis]
  Refine = true
  Suppressed = false
  Type = 0
FEATURE [Sketcher::SketchObject] Sketch062
  ArcFitTolerance = 1e-06
  AttachmentSupport = -> [Pocket025]
  FullyConstrained = true
  MakeInternals = false
  MapMode = 5
  Placement = pos=(0,0,150) rot=(0,0,1;0rad)
  sketch-geometry (5):
    g0: LineSegment StartX=-10 StartY=15 StartZ=0 EndX=-10 EndY=-15 EndZ=0
    g1: LineSegment StartX=-10 StartY=-15 StartZ=0 EndX=10 EndY=-15 EndZ=0
    g2: LineSegment StartX=10 StartY=-15 StartZ=0 EndX=10 EndY=15 EndZ=0
    g3: LineSegment StartX=10 StartY=15 StartZ=0 EndX=-10 EndY=15 EndZ=0
    g4: GeomPoint [constr] X=0 Y=0 Z=0
  constraints (12):
    c: Coincident(g0,g1)
    c: Coincident(g1,g2)
    c: Coincident(g2,g3)
    c: Coincident(g3,g0)
    c: Vertical(g0)
    c: Vertical(g2)
    c: Horizontal(g1)
    c: Horizontal(g3)
    c: Symmetric(g2,g0,g4)
    c: Coincident(g4,g-1)
    c: DistanceX(g0,g2) = 20
    c: DistanceY(g0,g0) = 30
FEATURE [PartDesign::Pad] Pad026
  BaseFeature = -> Pocket025
  Direction = (0,0,1)
  Length = 30
  Length2 = 10
  Profile = -> Sketch062
  ReferenceAxis = -> Sketch062 [N_Axis]
  Refine = true
  Reversed = true
  Suppressed = false
  Type = 0
FEATURE [Sketcher::SketchObject] Sketch063
  ArcFitTolerance = 1e-06
  AttachmentSupport = -> [Pad026]
  ExternalGeometry = -> [Pad026]
  FullyConstrained = false
  MakeInternals = false
  MapMode = 5
  Placement = pos=(-10,0,0) rot=(0.57735,-0.57735,-0.57735;2.0944rad)
  sketch-geometry (5):
    g0: LineSegment StartX=-2.5723 StartY=135 StartZ=0 EndX=2.5723 EndY=135 EndZ=0
    g1: LineSegment StartX=2.5723 StartY=135 StartZ=0 EndX=2.5723 EndY=153.987 EndZ=0
    g2: LineSegment StartX=2.5723 StartY=153.987 StartZ=0 EndX=-2.5723 EndY=153.987 EndZ=0
    g3: LineSegment StartX=-2.5723 StartY=153.987 StartZ=0 EndX=-2.5723 EndY=135 EndZ=0
    g4: GeomPoint [constr] X=0 Y=144.493 Z=0
  constraints (11):
    c: Coincident(g0,g1)
    c: Coincident(g1,g2)
    c: Coincident(g2,g3)
    c: Coincident(g3,g0)
    c: Horizontal(g0)
    c: Horizontal(g2)
    c: Vertical(g1)
    c: Vertical(g3)
    c: Symmetric(g2,g0,g4)
    c: PointOnObject(g4,g-2)
    c: DistanceY(g0,g-3) = 15
FEATURE [PartDesign::Pocket] Pocket026
  BaseFeature = -> Pad026
  Direction = (1,0,0)
  Length = 5
  Length2 = 5
  Profile = -> Sketch063
  ReferenceAxis = -> Sketch063 [N_Axis]
  Refine = true
  Suppressed = false
  Type = 1
FEATURE [PartDesign::Fillet] Fillet014
  Base = -> Pocket026 [Edge25,Edge26,Edge24,Edge28]
  BaseFeature = -> Pocket026
  Radius = 6
  Refine = true
  SupportTransform = false
  Suppressed = false
  UseAllEdges = false
FEATURE [PartDesign::Fillet] Fillet015
  Base = -> Fillet014 [Edge9]
  BaseFeature = -> Fillet014
  Radius = 4
  Refine = true
  SupportTransform = false
  Suppressed = false
  UseAllEdges = false
FEATURE [PartDesign::Body] Body005  label="EJE"
  AllowCompound = false
  Group = -> [Sketch059,Pad024,Sketch060,Pad025,Sketch061,Pocket025,Sketch062,Pad026,Sketch063,Pocket026,Fillet014,Fillet015]
  Origin = -> Origin008
  Placement = pos=(3.1e-15,-0.2,-54.6) rot=(0,1,0;3.14159rad)
  Tip = -> Fillet015
FEATURE [App::Part] Part002  label="CUTIING HEAD"
  Group = -> [Body005,Body006,Body007,Body021]
  Origin = -> Origin007
  Placement = pos=(0,142.4,-7.3) rot=(0,0,1;0rad)
FEATURE [Sketcher::SketchObject] Sketch070
  ArcFitTolerance = 1e-06
  AttachmentSupport = -> [YZ_Plane034]
  FullyConstrained = false
  MakeInternals = false
  MapMode = 5
  Placement = pos=(0,0,0) rot=(0.57735,0.57735,0.57735;2.0944rad)
  sketch-geometry (6):
    g0: LineSegment StartX=10 StartY=0 StartZ=0 EndX=159.624 EndY=0 EndZ=0
    g1: LineSegment StartX=159.624 StartY=0 StartZ=0 EndX=159.624 EndY=28 EndZ=0
    g2: LineSegment StartX=159.624 StartY=28 StartZ=0 EndX=10 EndY=28 EndZ=0
    g3: LineSegment StartX=10 StartY=28 StartZ=0 EndX=10 EndY=0 EndZ=0
    g4: GeomPoint X=0 Y=37.4701 Z=0
    g5: LineSegment [constr] StartX=169.624 StartY=37.8913 StartZ=0 EndX=169.624 EndY=5.87023 EndZ=0
  constraints (15):
    c: Coincident(g0,g1)
    c: Coincident(g1,g2)
    c: Coincident(g2,g3)
    c: Coincident(g3,g0)
    c: Horizontal(g0)
    c: Horizontal(g2)
    c: Vertical(g1)
    c: Vertical(g3)
    c: PointOnObject(g4,g-2)
    c: DistanceX(g4,g2) = 10
    c: DistanceY(g0,g1) = 28
    c: Vertical(g5)
    c: Block(g5)
    c: DistanceX(g1,g5) = 10
    c: PointOnObject(g0,g-1)
FEATURE [PartDesign::Pad] Pad029
  Direction = (1,0,0)
  Length = 12
  Length2 = 10
  Midplane = true
  Placement = pos=(0,0,0) rot=(1,1,1;2.0944rad)
  Profile = -> Sketch070
  ReferenceAxis = -> Sketch070 [N_Axis]
  Refine = true
  Suppressed = false
  Type = 0
FEATURE [Sketcher::SketchObject] Sketch075
  ArcFitTolerance = 1e-06
  AttachmentSupport = -> [Mirrored]
  ExternalGeometry = -> [Mirrored]
  FullyConstrained = true
  MakeInternals = false
  MapMode = 5
  Placement = pos=(-21,0,0) rot=(0.57735,-0.57735,-0.57735;2.0944rad)
  sketch-geometry (1):
    g0: Circle CenterX=0 CenterY=3 CenterZ=0 NormalX=0 NormalY=0 NormalZ=1 AngleXU=0 Radius=1.25
  constraints (3):
    c: PointOnObject(g0,g-2)
    c: Diameter(g0) = 2.5
    c: DistanceY(g-1,g0) = 3
FEATURE [PartDesign::Pocket] Pocket034
  BaseFeature = -> Mirrored
  Direction = (1,0,0)
  Length = 5
  Length2 = 5
  Profile = -> Sketch075
  ReferenceAxis = -> Sketch075 [N_Axis]
  Refine = true
  Suppressed = false
  Type = 1
FEATURE [Sketcher::SketchObject] Sketch076
  ArcFitTolerance = 1e-06
  AttachmentSupport = -> [Pocket034]
  FullyConstrained = true
  MakeInternals = false
  MapMode = 5
  Placement = pos=(5.7e-15,-21,0) rot=(1,0,0;1.5708rad)
  sketch-geometry (1):
    g0: Circle CenterX=0 CenterY=3 CenterZ=0 NormalX=0 NormalY=0 NormalZ=1 AngleXU=0 Radius=2
  constraints (3):
    c: PointOnObject(g0,g-2)
    c: Diameter(g0) = 4
    c: DistanceY(g-1,g0) = 3
FEATURE [PartDesign::Pocket] Pocket035
  BaseFeature = -> Pocket034
  Direction = (0,1,-2e-16)
  Length = 7
  Length2 = 5
  Profile = -> Sketch076
  ReferenceAxis = -> Sketch076 [N_Axis]
  Refine = true
  Suppressed = false
  Type = 0
FEATURE [Sketcher::SketchObject] Sketch077
  ArcFitTolerance = 1e-06
  AttachmentSupport = -> [Pocket035]
  ExternalGeometry = -> [Pocket035]
  FullyConstrained = false
  MakeInternals = false
  MapMode = 5
  Placement = pos=(77.6546,31.8445,0) rot=(0.428528,0.638891,0.638891;2.33188rad)
  sketch-geometry (3):
    g0: Circle CenterX=158.508 CenterY=3 CenterZ=0 NormalX=0 NormalY=0 NormalZ=1 AngleXU=0 Radius=1.77819
    g1: GeomPoint X=160.728 Y=0 Z=0
    g2: LineSegment [constr] StartX=158.508 StartY=3 StartZ=0 EndX=158.508 EndY=9.39697 EndZ=0
  constraints (4):
    c: PointOnObject(g1,g-1)
    c: DistanceY(g1,g0) = 3
    c: Coincident(g2,g0)
    c: Symmetric(g-4,g-3,g2)
FEATURE [PartDesign::Pocket] Pocket036
  BaseFeature = -> Pocket035
  Direction = (-0.925226,-0.379416,-1e-16)
  Length = 6
  Length2 = 5
  Profile = -> Sketch077
  ReferenceAxis = -> Sketch077 [N_Axis]
  Refine = true
  Suppressed = false
  Type = 0
FEATURE [Sketcher::SketchObject] Sketch078
  ArcFitTolerance = 1e-06
  AttachmentSupport = -> [Pocket036]
  ExternalGeometry = -> [Pocket036]
  FullyConstrained = false
  MakeInternals = false
  MapMode = 5
  Placement = pos=(-77.6546,31.8445,0) rot=(-0.428528,0.638891,0.638891;3.9513rad)
  sketch-geometry (2):
    g0: LineSegment [constr] StartX=-158.508 StartY=3 StartZ=0 EndX=-158.508 EndY=-5.5879 EndZ=0
    g1: Circle CenterX=-158.508 CenterY=3 CenterZ=0 NormalX=0 NormalY=0 NormalZ=1 AngleXU=0 Radius=2
  constraints (4):
    c: Symmetric(g-3,g-4,g0)
    c: Coincident(g1,g0)
    c: Diameter(g1) = 4
    c: DistanceY(g-4,g0) = 3
FEATURE [PartDesign::Pocket] Pocket037
  BaseFeature = -> Pocket036
  Direction = (0.925226,-0.379416,-1e-16)
  Length = 6
  Length2 = 5
  Profile = -> Sketch078
  ReferenceAxis = -> Sketch078 [N_Axis]
  Refine = true
  Suppressed = false
  Type = 0
FEATURE [Sketcher::SketchObject] Sketch079
  ArcFitTolerance = 1e-06
  AttachmentSupport = -> [Pocket037]
  FullyConstrained = false
  MakeInternals = false
  MapMode = 5
  Placement = pos=(0,0,6) rot=(0,0,1;0rad)
  sketch-geometry (4):
    g0: LineSegment [constr] StartX=-15 StartY=160.24 StartZ=0 EndX=15 EndY=160.24 EndZ=0
    g1: GeomPoint [constr] X=54.5821 Y=0 Z=0
    g2: Circle CenterX=-15 CenterY=160.24 CenterZ=0 NormalX=0 NormalY=0 NormalZ=1 AngleXU=0 Radius=2
    g3: Circle CenterX=15 CenterY=160.24 CenterZ=0 NormalX=0 NormalY=0 NormalZ=1 AngleXU=0 Radius=2
  constraints (8):
    c: PointOnObject(g1,g-1)
    c: DistanceY(g1,g0) = 160.24
    c: Symmetric(g0,g0,g-2)
    c: DistanceX(g0,g0) = 30
    c: Coincident(g2,g0)
    c: Coincident(g3,g0)
    c: Equal(g3,g2)
    c: Diameter(g3) = 4
FEATURE [PartDesign::Pocket] Pocket038
  BaseFeature = -> Pocket037
  Direction = (0,0,-1)
  Length = 4
  Length2 = 5
  Profile = -> Sketch079
  ReferenceAxis = -> Sketch079 [N_Axis]
  Refine = true
  Suppressed = false
  Type = 0
FEATURE [PartDesign::Body] Body011  label="Arm_elbow_plate_top_long"
  AllowCompound = false
  Group = -> [Sketch018,Pad008,Sketch020,Pocket005,Sketch,Pocket,Mirrored,Sketch075,Pocket034,Sketch076,Pocket035,Sketch077,Pocket036,Sketch078,Pocket037,Sketch079,Pocket038]
  Origin = -> Origin015
  Placement = pos=(0,-0.2,21.6) rot=(0,0,1;0rad)
  Tip = -> Pocket038
FEATURE [Sketcher::SketchObject] Sketch081
  ArcFitTolerance = 1e-06
  AttachmentSupport = -> [XY_Plane035]
  FullyConstrained = false
  MakeInternals = false
  MapMode = 5
  sketch-geometry (24):
    g0: LineSegment [constr] StartX=-66.1561 StartY=0 StartZ=0 EndX=72.2125 EndY=0 EndZ=0
    g1: LineSegment [constr] StartX=-43.1906 StartY=170 StartZ=0 EndX=73.1906 EndY=170 EndZ=0
    g2: LineSegment StartX=-21 StartY=170 StartZ=0 EndX=-21 EndY=-6.55744 EndZ=0
    g3: LineSegment StartX=-6.55744 StartY=-21 StartZ=0 EndX=6.55744 EndY=-21 EndZ=0
    g4: LineSegment StartX=21 StartY=-6.55744 StartZ=0 EndX=21 EndY=170 EndZ=0
    g5: Circle CenterX=-1.2e-15 CenterY=0 CenterZ=0 NormalX=0 NormalY=0 NormalZ=1 AngleXU=0 Radius=12.65
    g6: ArcOfCircle CenterX=-1.2e-15 CenterY=0 CenterZ=0 NormalX=0 NormalY=0 NormalZ=1 AngleXU=0 Radius=22 StartAngle=3.44426 EndAngle=4.40972
    g7: ArcOfCircle CenterX=-1.2e-15 CenterY=0 CenterZ=0 NormalX=0 NormalY=0 NormalZ=1 AngleXU=0 Radius=22 StartAngle=5.01505 EndAngle=5.98052
    g8: ArcOfCircle CenterX=0 CenterY=181.271 CenterZ=0 NormalX=0 NormalY=0 NormalZ=1 AngleXU=0 Radius=15.207 StartAngle=0.386238 EndAngle=2.75535
    g9: LineSegment StartX=-14.0867 StartY=187 StartZ=0 EndX=-21 EndY=170 EndZ=0
    g10: LineSegment StartX=14.0867 StartY=187 StartZ=0 EndX=21 EndY=170 EndZ=0
    g11: LineSegment [constr] StartX=-50.6378 StartY=187 StartZ=0 EndX=60.3893 EndY=187 EndZ=0
    g12: GeomPoint X=3.72478 Y=-21 Z=0
    g13: Circle CenterX=0 CenterY=170 CenterZ=0 NormalX=0 NormalY=0 NormalZ=1 AngleXU=0 Radius=8.25
    g14: LineSegment StartX=16.4 StartY=173.25 StartZ=0 EndX=13.6 EndY=173.25 EndZ=0
    g15: LineSegment StartX=13.6 StartY=173.25 StartZ=0 EndX=13.6 EndY=166.75 EndZ=0
    g16: LineSegment StartX=13.6 StartY=166.75 StartZ=0 EndX=16.4 EndY=166.75 EndZ=0
    g17: LineSegment StartX=16.4 StartY=166.75 StartZ=0 EndX=16.4 EndY=173.25 EndZ=0
    g18: GeomPoint [constr] X=15 Y=170 Z=0
    g19: LineSegment StartX=-16.4 StartY=173.25 StartZ=0 EndX=-16.4 EndY=166.75 EndZ=0
    g20: LineSegment StartX=-16.4 StartY=166.75 StartZ=0 EndX=-13.6 EndY=166.75 EndZ=0
    g21: LineSegment StartX=-13.6 StartY=166.75 StartZ=0 EndX=-13.6 EndY=173.25 EndZ=0
    g22: LineSegment StartX=-13.6 StartY=173.25 StartZ=0 EndX=-16.4 EndY=173.25 EndZ=0
    g23: GeomPoint [constr] X=-15 Y=170 Z=0
  constraints (58):
    c: Horizontal(g1)
    c: DistanceY(g0,g1) = 170
    c: Vertical(g2)
    c: PointOnObject(g2,g1)
    c: PointOnObject(g5,g0)
    c: Symmetric(g10,g9,g-2)
    c: Diameter(g5) = 25.3
    c: DistanceX(g2,g4) = 42
    c: Symmetric(g2,g4,g-2)
    c: Symmetric(g3,g3,g-2)
    c: Coincident(g6,g2)
    c: Coincident(g6,g3)
    c: Coincident(g7,g6)
    c: Coincident(g7,g4)
    c: Coincident(g7,g3)
    c: Coincident(g6,g5)
    c: PointOnObject(g8,g-2)
    c: Tangent(g9,g8) = -1.5708
    c: Tangent(g10,g8) = 1.5708
    c: Coincident(g2,g9)
    c: Coincident(g10,g4)
    c: Horizontal(g11)
    c: PointOnObject(g8,g11)
    c: DistanceY(g1,g11) = 17
    c: PointOnObject(g12,g3)
    c: DistanceY(g12,g0) = 21
    c: PointOnObject(g5,g-1)
    c: PointOnObject(g0,g-1)
    c: Radius(g6) = 22
    c: PointOnObject(g13,g1)
    c: Diameter(g13) = 16.5
    c: PointOnObject(g13,g-2)
    c: Coincident(g14,g15)
    c: Coincident(g15,g16)
    c: Coincident(g16,g17)
    c: Coincident(g17,g14)
    c: Horizontal(g14)
    c: Horizontal(g16)
    c: Vertical(g15)
    c: Vertical(g17)
    c: Symmetric(g16,g14,g18)
    c: Symmetric(g1,g1,g18)
    c: DistanceX(g15,g16) = 2.8
    c: DistanceY(g16,g14) = 6.5
    c: DistanceX(g8,g18) = 15
    c: Coincident(g19,g20)
    c: Coincident(g20,g21)
    c: Coincident(g21,g22)
    c: Coincident(g22,g19)
    c: Vertical(g19)
    c: Vertical(g21)
    c: Horizontal(g20)
    c: Horizontal(g22)
    c: Symmetric(g21,g19,g23)
    c: PointOnObject(g23,g1)
    c: Horizontal(g20,g15)
    c: DistanceX(g23,g8) = 15
    c: DistanceX(g19,g20) = 2.8
FEATURE [PartDesign::Pad] Pad030
  Direction = (0,0,1)
  Length = 6
  Length2 = 10
  Profile = -> Sketch081
  ReferenceAxis = -> Sketch081 [N_Axis]
  Refine = true
  Suppressed = false
  Type = 0
FEATURE [Sketcher::SketchObject] Sketch082
  ArcFitTolerance = 1e-06
  AttachmentSupport = -> [Pad030]
  ExternalGeometry = -> [Pad030]
  FullyConstrained = false
  MakeInternals = false
  MapMode = 5
  Placement = pos=(0,0,6) rot=(0,0,1;0rad)
  sketch-geometry (16):
    g0: LineSegment [constr] StartX=-17 StartY=112 StartZ=0 EndX=-17 EndY=45 EndZ=0
    g1: LineSegment [constr] StartX=-17 StartY=45 StartZ=0 EndX=17 EndY=45 EndZ=0
    g2: LineSegment [constr] StartX=17 StartY=45 StartZ=0 EndX=17 EndY=112 EndZ=0
    g3: LineSegment [constr] StartX=17 StartY=112 StartZ=0 EndX=-17 EndY=112 EndZ=0
    g4: Circle CenterX=17 CenterY=112 CenterZ=0 NormalX=0 NormalY=0 NormalZ=1 AngleXU=0 Radius=1.7
    g5: Circle CenterX=-17 CenterY=112 CenterZ=0 NormalX=0 NormalY=0 NormalZ=1 AngleXU=0 Radius=1.7
    g6: Circle CenterX=17 CenterY=45 CenterZ=0 NormalX=0 NormalY=0 NormalZ=1 AngleXU=0 Radius=1.7
    g7: Circle CenterX=-17 CenterY=45 CenterZ=0 NormalX=0 NormalY=0 NormalZ=1 AngleXU=0 Radius=1.7
    g8: LineSegment [constr] StartX=-5 StartY=183.792 StartZ=0 EndX=-5 EndY=135.241 EndZ=0
    g9: LineSegment [constr] StartX=-5 StartY=135.241 StartZ=0 EndX=5 EndY=135.241 EndZ=0
    g10: LineSegment [constr] StartX=5 StartY=135.241 StartZ=0 EndX=5 EndY=183.792 EndZ=0
    g11: LineSegment [constr] StartX=5 StartY=183.792 StartZ=0 EndX=-5 EndY=183.792 EndZ=0
    g12: Circle CenterX=-5 CenterY=135.241 CenterZ=0 NormalX=0 NormalY=0 NormalZ=1 AngleXU=0 Radius=1.25
    g13: Circle CenterX=5 CenterY=135.241 CenterZ=0 NormalX=0 NormalY=0 NormalZ=1 AngleXU=0 Radius=1.25
    g14: Circle CenterX=5 CenterY=183.792 CenterZ=0 NormalX=0 NormalY=0 NormalZ=1 AngleXU=0 Radius=1.25
    g15: Circle CenterX=-5 CenterY=183.792 CenterZ=0 NormalX=0 NormalY=0 NormalZ=1 AngleXU=0 Radius=1.25
  constraints (36):
    c: Coincident(g0,g1)
    c: Coincident(g1,g2)
    c: Coincident(g2,g3)
    c: Coincident(g3,g0)
    c: Vertical(g0)
    c: Vertical(g2)
    c: Horizontal(g1)
    c: Symmetric(g0,g2,g-2)
    c: DistanceX(g-1,g1) = 17
    c: Coincident(g4,g2)
    c: Coincident(g5,g0)
    c: Coincident(g6,g1)
    c: Coincident(g7,g0)
    c: Equal(g7,g6)
    c: Equal(g7,g4)
    c: Equal(g7,g5)
    c: Diameter(g7) = 3.4
    c: DistanceY(g-1,g1) = 45
    c: DistanceY(g-1,g2) = 112
    c: Coincident(g8,g9)
    c: Coincident(g9,g10)
    c: Coincident(g10,g11)
    c: Coincident(g11,g8)
    c: Vertical(g8)
    c: Vertical(g10)
    c: Horizontal(g9)
    c: Symmetric(g8,g10,g-2)
    c: Coincident(g12,g8)
    c: Coincident(g13,g9)
    c: Coincident(g14,g10)
    c: Coincident(g15,g8)
    c: Equal(g15,g14)
    c: Equal(g15,g12)
    c: Equal(g15,g13)
    c: Diameter(g15) = 2.5
    c: DistanceX(g8,g10) = 10
FEATURE [PartDesign::Pocket] Pocket040
  BaseFeature = -> Pad030
  Direction = (0,0,-1)
  Length = 5
  Length2 = 5
  Profile = -> Sketch082
  ReferenceAxis = -> Sketch082 [N_Axis]
  Refine = true
  Suppressed = false
  Type = 1
FEATURE [Sketcher::SketchObject] Sketch080
  ArcFitTolerance = 1e-06
  AttachmentSupport = -> [Pocket040]
  FullyConstrained = false
  MakeInternals = false
  MapMode = 5
  Placement = pos=(0,0,6) rot=(0,0,1;0rad)
  sketch-geometry (38):
    g0: LineSegment [constr] StartX=-12 StartY=121.792 StartZ=0 EndX=-12 EndY=15.9918 EndZ=0
    g1: LineSegment [constr] StartX=-12 StartY=15.9918 StartZ=0 EndX=12 EndY=15.9918 EndZ=0
    g2: LineSegment [constr] StartX=12 StartY=15.9918 StartZ=0 EndX=12 EndY=121.792 EndZ=0
    g3: LineSegment [constr] StartX=12 StartY=121.792 StartZ=0 EndX=-12 EndY=121.792 EndZ=0
    g4: LineSegment [constr] StartX=-3 StartY=131.645 StartZ=0 EndX=-3 EndY=23.7908 EndZ=0
    g5: LineSegment [constr] StartX=-3 StartY=23.7908 StartZ=0 EndX=3 EndY=23.7908 EndZ=0
    g6: LineSegment [constr] StartX=3 StartY=23.7908 StartZ=0 EndX=3 EndY=131.645 EndZ=0
    g7: LineSegment [constr] StartX=3 StartY=131.645 StartZ=0 EndX=-3 EndY=131.645 EndZ=0
    g8: LineSegment StartX=9.34582 StartY=41.7755 StartZ=0 EndX=5.65418 EndY=41.7755 EndZ=0
    g9: LineSegment StartX=3 StartY=39.1214 StartZ=0 EndX=3 EndY=29.1362 EndZ=0
    g10: LineSegment StartX=4.14183 StartY=26.9551 StartZ=0 EndX=7.83348 EndY=24.3954 EndZ=0
    g11: LineSegment StartX=12 StartY=26.5766 StartZ=0 EndX=12 EndY=39.1214 EndZ=0
    g12: ArcOfCircle CenterX=9.34582 CenterY=39.1214 CenterZ=0 NormalX=0 NormalY=0 NormalZ=1 AngleXU=0 Radius=2.65418 StartAngle=-9e-16 EndAngle=1.5708
    g13: ArcOfCircle CenterX=5.65418 CenterY=39.1214 CenterZ=0 NormalX=0 NormalY=0 NormalZ=1 AngleXU=0 Radius=2.65418 StartAngle=1.5708 EndAngle=3.14159
    g14: ArcOfCircle CenterX=5.65418 CenterY=29.1362 CenterZ=0 NormalX=0 NormalY=0 NormalZ=1 AngleXU=0 Radius=2.65418 StartAngle=3.14159 EndAngle=4.10613
    g15: ArcOfCircle CenterX=9.34582 CenterY=26.5766 CenterZ=0 NormalX=0 NormalY=0 NormalZ=1 AngleXU=0 Radius=2.65418 StartAngle=4.10613 EndAngle=6.28319
    g16: GeomPoint [constr] X=12 Y=41.7755 Z=0
    g17: GeomPoint [constr] X=3 Y=27.7468 Z=0
    g18: LineSegment StartX=12 StartY=50.4297 StartZ=0 EndX=12 EndY=105.062 EndZ=0
    g19: LineSegment StartX=9.34582 StartY=107.716 StartZ=0 EndX=5.65418 EndY=107.716 EndZ=0
    g20: LineSegment StartX=3 StartY=105.062 StartZ=0 EndX=3 EndY=50.4297 EndZ=0
    g21: LineSegment StartX=5.65418 StartY=47.7755 StartZ=0 EndX=9.34582 EndY=47.7755 EndZ=0
    g22: ArcOfCircle CenterX=9.34582 CenterY=50.4297 CenterZ=0 NormalX=0 NormalY=0 NormalZ=1 AngleXU=0 Radius=2.65418 StartAngle=4.71239 EndAngle=6.28319
    g23: ArcOfCircle CenterX=9.34582 CenterY=105.062 CenterZ=0 NormalX=0 NormalY=0 NormalZ=1 AngleXU=0 Radius=2.65418 StartAngle=3e-16 EndAngle=1.5708
    g24: ArcOfCircle CenterX=5.65418 CenterY=105.062 CenterZ=0 NormalX=0 NormalY=0 NormalZ=1 AngleXU=0 Radius=2.65418 StartAngle=1.5708 EndAngle=3.14159
    g25: ArcOfCircle CenterX=5.65418 CenterY=50.4297 CenterZ=0 NormalX=0 NormalY=0 NormalZ=1 AngleXU=0 Radius=2.65418 StartAngle=3.14159 EndAngle=4.71239
    g26: GeomPoint [constr] X=12 Y=47.7755 Z=0
    g27: GeomPoint [constr] X=3 Y=107.716 Z=0
    g28: LineSegment StartX=3 StartY=121.792 StartZ=0 EndX=3 EndY=115.825 EndZ=0
    g29: LineSegment StartX=5.10848 StartY=113.716 StartZ=0 EndX=9.89152 EndY=113.716 EndZ=0
    g30: LineSegment StartX=12 StartY=115.825 StartZ=0 EndX=12 EndY=123.92 EndZ=0
    g31: LineSegment StartX=9.03468 StartY=125.846 StartZ=0 EndX=4.25164 EndY=123.719 EndZ=0
    g32: ArcOfCircle CenterX=5.10848 CenterY=121.792 CenterZ=0 NormalX=0 NormalY=0 NormalZ=1 AngleXU=0 Radius=2.10848 StartAngle=1.98928 EndAngle=3.14159
    g33: ArcOfCircle CenterX=5.10848 CenterY=115.825 CenterZ=0 NormalX=0 NormalY=0 NormalZ=1 AngleXU=0 Radius=2.10848 StartAngle=3.14159 EndAngle=4.71239
    g34: ArcOfCircle CenterX=9.89152 CenterY=115.825 CenterZ=0 NormalX=0 NormalY=0 NormalZ=1 AngleXU=0 Radius=2.10848 StartAngle=4.71239 EndAngle=6.28319
    g35: ArcOfCircle CenterX=9.89152 CenterY=123.92 CenterZ=0 NormalX=0 NormalY=0 NormalZ=1 AngleXU=0 Radius=2.10848 StartAngle=-1.8e-15 EndAngle=1.98928
    g36: GeomPoint [constr] X=3 Y=123.162 Z=0
    g37: GeomPoint [constr] X=12 Y=113.716 Z=0
  constraints (83):
    c: Coincident(g0,g1)
    c: Coincident(g1,g2)
    c: Coincident(g2,g3)
    c: Coincident(g3,g0)
    c: Vertical(g0)
    c: Vertical(g2)
    c: Horizontal(g1)
    c: Coincident(g4,g5)
    c: Coincident(g5,g6)
    c: Coincident(g6,g7)
    c: Coincident(g7,g4)
    c: Vertical(g4)
    c: Vertical(g6)
    c: Horizontal(g5)
    c: Symmetric(g4,g6,g-2)
    c: Symmetric(g0,g2,g-2)
    c: DistanceX(g0,g2) = 24
    c: DistanceX(g4,g6) = 6
    c: Tangent(g8,g12) = -1.5708
    c: Tangent(g8,g13) = -1.5708
    c: Tangent(g9,g13) = -1.5708
    c: Tangent(g9,g14) = -1.5708
    c: Tangent(g10,g14) = -1.5708
    c: Tangent(g10,g15) = -1.5708
    c: Tangent(g11,g15) = -1.5708
    c: Tangent(g11,g12) = -1.5708
    c: Horizontal(g8)
    c: Vertical(g9)
    c: Vertical(g11)
    c: Equal(g12,g13)
    c: Equal(g13,g14)
    c: Equal(g14,g15)
    c: PointOnObject(g16,g8)
    c: PointOnObject(g16,g11)
    c: PointOnObject(g17,g9)
    c: PointOnObject(g17,g10)
    c: PointOnObject(g16,g2)
    c: PointOnObject(g17,g6)
    c: Tangent(g18,g22) = -1.5708
    c: Tangent(g18,g23) = -1.5708
    c: Tangent(g19,g23) = -1.5708
    c: Tangent(g19,g24) = -1.5708
    c: Tangent(g20,g24) = -1.5708
    c: Tangent(g20,g25) = -1.5708
    c: Tangent(g21,g25) = -1.5708
    c: Tangent(g21,g22) = -1.5708
    c: Vertical(g18)
    c: Vertical(g20)
    c: Horizontal(g19)
    c: Horizontal(g21)
    c: Equal(g22,g23)
    c: Equal(g23,g24)
    c: Equal(g24,g25)
    c: PointOnObject(g26,g18)
    c: PointOnObject(g26,g21)
    c: PointOnObject(g27,g19)
    c: PointOnObject(g27,g20)
    c: PointOnObject(g26,g2)
    c: PointOnObject(g27,g6)
    c: Tangent(g28,g32) = -1.5708
    c: Tangent(g28,g33) = -1.5708
    c: Tangent(g29,g33) = -1.5708
    c: Tangent(g29,g34) = -1.5708
    c: Tangent(g30,g34) = -1.5708
    c: Tangent(g30,g35) = -1.5708
    c: Tangent(g31,g35) = -1.5708
    c: Tangent(g31,g32) = -1.5708
    c: Vertical(g28)
    c: Vertical(g30)
    c: Horizontal(g29)
    c: Equal(g32,g33)
    c: Equal(g33,g34)
    c: Equal(g34,g35)
    c: PointOnObject(g36,g28)
    c: PointOnObject(g36,g31)
    c: PointOnObject(g37,g29)
    c: PointOnObject(g37,g30)
    c: PointOnObject(g36,g6)
    c: PointOnObject(g37,g2)
    c: PointOnObject(g32,g3)
    c: DistanceY(g16,g26) = 6
    c: Vertical(g12,g22)
    c: DistanceY(g27,g37) = 6
FEATURE [PartDesign::Pocket] Pocket039
  BaseFeature = -> Pocket040
  Direction = (0,0,-1)
  Length = 5
  Length2 = 5
  Profile = -> Sketch080
  ReferenceAxis = -> Sketch080 [N_Axis]
  Refine = true
  Suppressed = false
  Type = 1
FEATURE [PartDesign::Mirrored] Mirrored001
  BaseFeature = -> Pocket039
  MirrorPlane = -> Sketch080 [V_Axis]
  Originals = -> [Pocket039]
  Refine = true
  Suppressed = false
  TransformMode = 0
FEATURE [Sketcher::SketchObject] Sketch083
  ArcFitTolerance = 1e-06
  AttachmentSupport = -> [Mirrored001]
  ExternalGeometry = -> [Mirrored001]
  FullyConstrained = true
  MakeInternals = false
  MapMode = 5
  Placement = pos=(-21,0,0) rot=(0.57735,-0.57735,-0.57735;2.0944rad)
  sketch-geometry (2):
    g0: Circle CenterX=0 CenterY=3 CenterZ=0 NormalX=0 NormalY=0 NormalZ=1 AngleXU=0 Radius=1.25
    g1: Circle CenterX=-170 CenterY=3 CenterZ=0 NormalX=0 NormalY=0 NormalZ=1 AngleXU=0 Radius=1.25
  constraints (5):
    c: PointOnObject(g0,g-2)
    c: Diameter(g0) = 2.5
    c: DistanceY(g-1,g0) = 3
    c: Symmetric(g-3,g-3,g1)
    c: Diameter(g1) = 2.5
FEATURE [PartDesign::Pocket] Pocket041
  BaseFeature = -> Mirrored001
  Direction = (1,0,0)
  Length = 5
  Length2 = 5
  Profile = -> Sketch083
  ReferenceAxis = -> Sketch083 [N_Axis]
  Refine = true
  Suppressed = false
  Type = 1
FEATURE [Sketcher::SketchObject] Sketch084
  ArcFitTolerance = 1e-06
  AttachmentSupport = -> [Pocket041]
  FullyConstrained = true
  MakeInternals = false
  MapMode = 5
  Placement = pos=(0,-21,0) rot=(1,0,0;1.5708rad)
  sketch-geometry (1):
    g0: Circle CenterX=0 CenterY=3 CenterZ=0 NormalX=0 NormalY=0 NormalZ=1 AngleXU=0 Radius=2
  constraints (3):
    c: PointOnObject(g0,g-2)
    c: Diameter(g0) = 4
    c: DistanceY(g-1,g0) = 3
FEATURE [PartDesign::Pocket] Pocket042
  BaseFeature = -> Pocket041
  Direction = (0,1,-2e-16)
  Length = 7
  Length2 = 5
  Profile = -> Sketch084
  ReferenceAxis = -> Sketch084 [N_Axis]
  Refine = true
  Suppressed = false
  Type = 0
FEATURE [Sketcher::SketchObject] Sketch085
  ArcFitTolerance = 1e-06
  AttachmentSupport = -> [Pocket042]
  FullyConstrained = false
  MakeInternals = false
  MapMode = 5
  Placement = pos=(77.3423,31.4523,0) rot=(0.429635,0.638519,0.638519;2.33001rad)
  sketch-geometry (3):
    g0: Circle CenterX=158.508 CenterY=3 CenterZ=0 NormalX=0 NormalY=0 NormalZ=1 AngleXU=0 Radius=1.77819
    g1: GeomPoint X=160.728 Y=0 Z=0
    g2: LineSegment [constr] StartX=158.508 StartY=3 StartZ=0 EndX=158.508 EndY=9.39697 EndZ=0
  constraints (4):
    c: PointOnObject(g1,g-1)
    c: DistanceY(g1,g0) = 3
    c: Coincident(g2,g0)
    c: Symmetric(g-4,g-3,g2)
FEATURE [PartDesign::Pocket] Pocket043
  BaseFeature = -> Pocket042
  Direction = (-0.926333,-0.376706,1e-16)
  Length = 6
  Length2 = 5
  Profile = -> Sketch085
  ReferenceAxis = -> Sketch085 [N_Axis]
  Refine = true
  Suppressed = false
  Type = 0
FEATURE [Sketcher::SketchObject] Sketch086
  ArcFitTolerance = 1e-06
  AttachmentSupport = -> [Pocket043]
  FullyConstrained = false
  MakeInternals = false
  MapMode = 5
  Placement = pos=(-77.3423,31.4523,0) rot=(-0.429635,0.638519,0.638519;3.95317rad)
  sketch-geometry (2):
    g0: LineSegment [constr] StartX=-158.508 StartY=3 StartZ=0 EndX=-158.508 EndY=-5.5879 EndZ=0
    g1: Circle CenterX=-158.508 CenterY=3 CenterZ=0 NormalX=0 NormalY=0 NormalZ=1 AngleXU=0 Radius=2
  constraints (4):
    c: Symmetric(g-3,g-4,g0)
    c: Coincident(g1,g0)
    c: Diameter(g1) = 4
    c: DistanceY(g-4,g0) = 3
FEATURE [PartDesign::Pocket] Pocket044
  BaseFeature = -> Pocket043
  Direction = (0.926333,-0.376706,-1e-16)
  Length = 6
  Length2 = 5
  Profile = -> Sketch086
  ReferenceAxis = -> Sketch086 [N_Axis]
  Refine = true
  Suppressed = false
  Type = 0
FEATURE [Sketcher::SketchObject] Sketch087
  ArcFitTolerance = 1e-06
  AttachmentSupport = -> [Pad029]
  ExternalGeometry = -> [Pad029]
  FullyConstrained = false
  MakeInternals = false
  MapMode = 5
  Placement = pos=(2.2e-15,10,0) rot=(0.57735,0.57735,-0.57735;2.0944rad)
  sketch-geometry (9):
    g0: LineSegment [constr] StartX=-39.7349 StartY=4 StartZ=0 EndX=11.0556 EndY=4 EndZ=0
    g1: LineSegment StartX=-39.7349 StartY=4 StartZ=0 EndX=-39.7349 EndY=-7.52706 EndZ=0
    g2: LineSegment StartX=-39.7349 StartY=-7.52706 StartZ=0 EndX=-22 EndY=-7.52706 EndZ=0
    g3: LineSegment StartX=-22 StartY=-7.52706 StartZ=0 EndX=-22 EndY=4 EndZ=0
    g4: LineSegment StartX=-22 StartY=4 StartZ=0 EndX=-39.7349 EndY=4 EndZ=0
    g5: LineSegment StartX=11.0556 StartY=4 StartZ=0 EndX=-6 EndY=4 EndZ=0
    g6: LineSegment StartX=-6 StartY=4 StartZ=0 EndX=-6 EndY=-7.94705 EndZ=0
    g7: LineSegment StartX=-6 StartY=-7.94705 StartZ=0 EndX=11.0556 EndY=-7.94705 EndZ=0
    g8: LineSegment StartX=11.0556 StartY=-7.94705 StartZ=0 EndX=11.0556 EndY=4 EndZ=0
  constraints (22):
    c: Horizontal(g0)
    c: DistanceY(g0,g-4) = 2
    c: Coincident(g1,g2)
    c: Coincident(g2,g3)
    c: Coincident(g3,g4)
    c: Coincident(g4,g1)
    c: Vertical(g1)
    c: Vertical(g3)
    c: Horizontal(g2)
    c: Horizontal(g4)
    c: Coincident(g1,g0)
    c: Coincident(g5,g6)
    c: Coincident(g6,g7)
    c: Coincident(g7,g8)
    c: Coincident(g8,g5)
    c: Horizontal(g5)
    c: Horizontal(g7)
    c: Vertical(g6)
    c: Vertical(g8)
    c: Coincident(g5,g0)
    c: DistanceX(g-3,g3) = 6
    c: DistanceX(g5,g-4) = 6
FEATURE [PartDesign::Pocket] Pocket045
  BaseFeature = -> Pad029
  Direction = (0,1,0)
  Length = 5
  Length2 = 5
  Placement = pos=(0,0,0) rot=(1,1,1;2.0944rad)
  Profile = -> Sketch087
  ReferenceAxis = -> Sketch087 [N_Axis]
  Refine = true
  Suppressed = false
  Type = 1
FEATURE [Sketcher::SketchObject] Sketch088
  ArcFitTolerance = 1e-06
  AttachmentSupport = -> [Pocket045]
  ExternalGeometry = -> [Pocket045]
  FullyConstrained = false
  MakeInternals = false
  MapMode = 5
  Placement = pos=(0,4.8e-15,22) rot=(0,0,-1;1.5708rad)
  sketch-geometry (17):
    g0: LineSegment [constr] StartX=-45 StartY=0 StartZ=0 EndX=-45 EndY=10.563 EndZ=0
    g1: LineSegment [constr] StartX=-112 StartY=0 StartZ=0 EndX=-112 EndY=11.6219 EndZ=0
    g2: Circle CenterX=-112 CenterY=0 CenterZ=0 NormalX=0 NormalY=0 NormalZ=1 AngleXU=0 Radius=1.8
    g3: Circle CenterX=-45 CenterY=0 CenterZ=0 NormalX=0 NormalY=0 NormalZ=1 AngleXU=0 Radius=1.8
    g4: LineSegment StartX=-9.86721 StartY=-2.32773 StartZ=0 EndX=-40.5656 EndY=-2.32773 EndZ=0
    g5: LineSegment StartX=-107.053 StartY=-2.59939 StartZ=0 EndX=-49.0719 EndY=-2.32773 EndZ=0
    g6: LineSegment StartX=-116.776 StartY=-2.59939 StartZ=0 EndX=-166.248 EndY=-2.59939 EndZ=0
    g7: GeomPoint X=0 Y=14.3735 Z=0
    g8: LineSegment StartX=-166.248 StartY=-2.59939 StartZ=0 EndX=-146.784 EndY=-56.3724 EndZ=0
    g9: LineSegment StartX=-146.784 StartY=-56.3724 StartZ=0 EndX=-2.14325 EndY=-56.3724 EndZ=0
    g10: LineSegment StartX=-2.14325 StartY=-56.3724 StartZ=0 EndX=-9.86721 EndY=-2.32773 EndZ=0
    g11: LineSegment StartX=-49.0719 StartY=-2.32773 StartZ=0 EndX=-46.45 EndY=-6 EndZ=0
    g12: LineSegment StartX=-46.45 StartY=-6 StartZ=0 EndX=-42.6719 EndY=-6 EndZ=0
    g13: LineSegment StartX=-42.6719 StartY=-6 StartZ=0 EndX=-40.5656 EndY=-2.32773 EndZ=0
    g14: LineSegment StartX=-116.776 StartY=-2.59939 StartZ=0 EndX=-113.01 EndY=-6 EndZ=0
    g15: LineSegment StartX=-113.01 StartY=-6 StartZ=0 EndX=-109.12 EndY=-6 EndZ=0
    g16: LineSegment StartX=-109.12 StartY=-6 StartZ=0 EndX=-107.053 EndY=-2.59939 EndZ=0
  constraints (32):
    c: PointOnObject(g0,g-1)
    c: PointOnObject(g1,g-1)
    c: Vertical(g1)
    c: Vertical(g0)
    c: Coincident(g2,g1)
    c: Coincident(g3,g0)
    c: Equal(g3,g2)
    c: Diameter(g3) = 3.6
    c: PointOnObject(g7,g-2)
    c: DistanceX(g1,g7) = 112
    c: Coincident(g8,g6)
    c: Coincident(g9,g8)
    c: Horizontal(g9)
    c: Coincident(g10,g9)
    c: Coincident(g10,g4)
    c: DistanceX(g0,g7) = 45
    c: Horizontal(g6)
    c: Horizontal(g4)
    c: Coincident(g5,g11)
    c: PointOnObject(g11,g-4)
    c: Coincident(g11,g12)
    c: PointOnObject(g12,g-4)
    c: Coincident(g12,g13)
    c: Coincident(g13,g4)
    c: Coincident(g6,g14)
    c: PointOnObject(g14,g-4)
    c: Coincident(g14,g15)
    c: PointOnObject(g15,g-4)
    c: Coincident(g15,g16)
    c: Coincident(g16,g5)
    c: Horizontal(g6,g5)
    c: Horizontal(g5,g4)
FEATURE [PartDesign::Pocket] Pocket046
  BaseFeature = -> Pocket045
  Direction = (0,0,-1)
  Length = 5
  Length2 = 5
  Placement = pos=(0,0,0) rot=(1,1,1;2.0944rad)
  Profile = -> Sketch088
  ReferenceAxis = -> Sketch088 [N_Axis]
  Refine = true
  Suppressed = false
  Type = 1
FEATURE [Sketcher::SketchObject] Sketch090
  ArcFitTolerance = 1e-06
  AttachmentSupport = -> [Pad009]
  ExternalGeometry = -> [Pad009]
  FullyConstrained = false
  MakeInternals = false
  MapMode = 5
  Placement = pos=(0,0,6) rot=(0,0,1;0rad)
  sketch-geometry (42):
    g0: LineSegment [constr] StartX=3 StartY=-5.42242 StartZ=0 EndX=3 EndY=239.303 EndZ=0
    g1: LineSegment [constr] StartX=16.2164 StartY=193.83 StartZ=0 EndX=18.2096 EndY=-28.4148 EndZ=0
    g2: LineSegment [constr] StartX=16.2164 StartY=193.83 StartZ=0 EndX=21.2164 EndY=193.875 EndZ=0
    g3: GeomPoint [constr] X=0 Y=232.447 Z=0
    g4: LineSegment StartX=16.9454 StartY=78.138 StartZ=0 EndX=16.9588 EndY=108.782 EndZ=0
    g5: LineSegment StartX=15.2492 StartY=116.94 StartZ=0 EndX=4.92278 EndY=116.94 EndZ=0
    g6: LineSegment StartX=3 StartY=118.863 StartZ=0 EndX=3 EndY=155.105 EndZ=0
    g7: LineSegment StartX=4.77873 StartY=156.883 StartZ=0 EndX=14.503 EndY=156.883 EndZ=0
    g8: LineSegment StartX=16.5661 StartY=154.839 StartZ=0 EndX=16.8911 EndY=118.597 EndZ=0
    g9: LineSegment StartX=5.36335 StartY=162.883 StartZ=0 EndX=15.3004 EndY=162.883 EndZ=0
    g10: LineSegment StartX=16.4832 StartY=164.077 StartZ=0 EndX=16.2547 EndY=189.554 EndZ=0
    g11: LineSegment StartX=14.4184 StartY=190.98 StartZ=0 EndX=4.63228 EndY=188.571 EndZ=0
    g12: LineSegment StartX=3 StartY=186.488 StartZ=0 EndX=3 EndY=165.247 EndZ=0
    g13: LineSegment [constr] StartX=3 StartY=110.94 StartZ=0 EndX=-6.77105 EndY=110.94 EndZ=0
    g14: GeomPoint [constr] X=17.3689 Y=65.0032 Z=0
    g15: ArcOfCircle CenterX=4.92278 CenterY=118.863 CenterZ=0 NormalX=0 NormalY=0 NormalZ=1 AngleXU=0 Radius=1.92278 StartAngle=3.14159 EndAngle=4.71239
    g16: GeomPoint [constr] X=3 Y=116.94 Z=0
    g17: ArcOfCircle CenterX=15.0761 CenterY=108.783 CenterZ=0 NormalX=0 NormalY=0 NormalZ=1 AngleXU=0 Radius=1.8827 StartAngle=6.28275 EndAngle=7.90944
    g18: GeomPoint [constr] X=16.9598 Y=110.94 Z=0
    g19: ArcOfCircle CenterX=15.2492 CenterY=118.582 CenterZ=0 NormalX=0 NormalY=0 NormalZ=1 AngleXU=0 Radius=1.64197 StartAngle=4.71239 EndAngle=6.29215
    g20: GeomPoint [constr] X=16.906 Y=116.94 Z=0
    g21: ArcOfCircle CenterX=14.503 CenterY=154.82 CenterZ=0 NormalX=0 NormalY=0 NormalZ=1 AngleXU=0 Radius=2.0631 StartAngle=0.00896837 EndAngle=1.5708
    g22: GeomPoint [constr] X=16.5477 Y=156.883 Z=0
    g23: ArcOfCircle CenterX=4.77873 CenterY=155.105 CenterZ=0 NormalX=0 NormalY=0 NormalZ=1 AngleXU=0 Radius=1.77873 StartAngle=1.5708 EndAngle=3.14159
    g24: GeomPoint [constr] X=3 Y=156.883 Z=0
    g25: ArcOfCircle CenterX=5.36335 CenterY=165.247 CenterZ=0 NormalX=0 NormalY=0 NormalZ=1 AngleXU=0 Radius=2.36335 StartAngle=3.14159 EndAngle=4.71239
    g26: GeomPoint [constr] X=3 Y=162.883 Z=0
    g27: ArcOfCircle CenterX=15.3004 CenterY=164.066 CenterZ=0 NormalX=0 NormalY=0 NormalZ=1 AngleXU=0 Radius=1.18288 StartAngle=4.71239 EndAngle=6.29215
    g28: GeomPoint [constr] X=16.4939 Y=162.883 Z=0
    g29: ArcOfCircle CenterX=5.14502 CenterY=186.488 CenterZ=0 NormalX=0 NormalY=0 NormalZ=1 AngleXU=0 Radius=2.14502 StartAngle=1.81217 EndAngle=3.14159
    g30: GeomPoint [constr] X=3 Y=188.169 Z=0
    g31: ArcOfCircle CenterX=14.7727 CenterY=189.541 CenterZ=0 NormalX=0 NormalY=0 NormalZ=1 AngleXU=0 Radius=1.48209 StartAngle=0.00896837 EndAngle=1.81217
    g32: GeomPoint [constr] X=16.2379 Y=191.428 Z=0
    g33: LineSegment StartX=14.9718 StartY=110.663 StartZ=0 EndX=6.56318 EndY=110.663 EndZ=0
    g34: LineSegment StartX=4.35546 StartY=108.455 StartZ=0 EndX=4.35546 EndY=79.3823 EndZ=0
    g35: LineSegment StartX=15.5004 StartY=76.6936 StartZ=0 EndX=7.04415 EndY=76.6936 EndZ=0
    g36: ArcOfCircle CenterX=6.56318 CenterY=108.455 CenterZ=0 NormalX=0 NormalY=0 NormalZ=1 AngleXU=0 Radius=2.20771 StartAngle=1.5708 EndAngle=3.14159
    g37: GeomPoint [constr] X=4.35546 Y=110.663 Z=0
    g38: ArcOfCircle CenterX=7.04415 CenterY=79.3823 CenterZ=0 NormalX=0 NormalY=0 NormalZ=1 AngleXU=0 Radius=2.68868 StartAngle=3.14159 EndAngle=4.71239
    g39: GeomPoint [constr] X=4.35546 Y=76.6936 Z=0
    g40: ArcOfCircle CenterX=15.5004 CenterY=78.1386 CenterZ=0 NormalX=0 NormalY=0 NormalZ=1 AngleXU=0 Radius=1.44499 StartAngle=4.71239 EndAngle=6.28275
    g41: GeomPoint [constr] X=16.9448 Y=76.6936 Z=0
  constraints (73):
    c: Vertical(g0)
    c: Parallel(g1,g-3)
    c: Coincident(g2,g1)
    c: Perpendicular(g2,g1)
    c: PointOnObject(g2,g-3)
    c: DistanceX(g1,g2) = 5
    c: PointOnObject(g3,g-2)
    c: DistanceX(g3,g0) = 3
    c: PointOnObject(g20,g1)
    c: Symmetric(g0,g0,g16)
    c: PointOnObject(g22,g1)
    c: Horizontal(g5)
    c: PointOnObject(g18,g1)
    c: DistanceY(g18,g20) = 6
    c: PointOnObject(g24,g0)
    c: Horizontal(g7)
    c: PointOnObject(g26,g0)
    c: PointOnObject(g28,g1)
    c: PointOnObject(g30,g0)
    c: Horizontal(g9)
    c: DistanceY(g22,g28) = 6
    c: PointOnObject(g32,g1)
    c: PointOnObject(g16,g5)
    c: PointOnObject(g16,g6)
    c: Tangent(g5,g15) = 1.5708
    c: Tangent(g6,g15) = 1.5708
    c: PointOnObject(g18,g4)
    c: Tangent(g4,g17) = -1.5708
    c: PointOnObject(g20,g5)
    c: PointOnObject(g20,g8)
    c: Tangent(g5,g19) = 1.5708
    c: Tangent(g8,g19) = 1.5708
    c: PointOnObject(g22,g7)
    c: PointOnObject(g22,g8)
    c: Tangent(g7,g21) = 1.5708
    c: Tangent(g8,g21) = 1.5708
    c: PointOnObject(g24,g6)
    c: PointOnObject(g24,g7)
    c: Tangent(g6,g23) = 1.5708
    c: Tangent(g7,g23) = 1.5708
    c: PointOnObject(g26,g9)
    c: PointOnObject(g26,g12)
    c: Tangent(g9,g25) = -1.5708
    c: Tangent(g12,g25) = -1.5708
    c: PointOnObject(g28,g9)
    c: PointOnObject(g28,g10)
    c: Tangent(g9,g27) = -1.5708
    c: Tangent(g10,g27) = -1.5708
    c: PointOnObject(g30,g11)
    c: PointOnObject(g30,g12)
    c: Tangent(g11,g29) = -1.5708
    c: Tangent(g12,g29) = -1.5708
    c: PointOnObject(g32,g10)
    c: PointOnObject(g32,g11)
    c: Tangent(g10,g31) = -1.5708
    c: Tangent(g11,g31) = -1.5708
    c: DistanceY(g-1,g13) = 110.94
    c: Coincident(g33,g17)
    c: Horizontal(g33)
    c: Vertical(g34)
    c: PointOnObject(g37,g33)
    c: PointOnObject(g37,g34)
    c: Tangent(g33,g36) = -1.5708
    c: Tangent(g34,g36) = -1.5708
    c: PointOnObject(g39,g34)
    c: PointOnObject(g39,g35)
    c: Tangent(g34,g38) = -1.5708
    c: Tangent(g35,g38) = 1.5708
    c: PointOnObject(g41,g4)
    c: PointOnObject(g41,g35)
    c: Tangent(g4,g40) = -1.5708
    c: Tangent(g35,g40) = 1.5708
    c: Horizontal(g35)
FEATURE [PartDesign::Pocket] Pocket048
  BaseFeature = -> Pad009
  Direction = (0,0,-1)
  Length = 5
  Length2 = 5
  Profile = -> Sketch090
  ReferenceAxis = -> Sketch090 [N_Axis]
  Refine = true
  Suppressed = false
  Type = 1
FEATURE [PartDesign::Mirrored] Mirrored002
  BaseFeature = -> Pocket048
  MirrorPlane = -> Sketch090 [V_Axis]
  Originals = -> [Pocket048]
  Refine = true
  Suppressed = false
  TransformMode = 0
FEATURE [Sketcher::SketchObject] Sketch091
  ArcFitTolerance = 1e-06
  AttachmentSupport = -> [Mirrored002]
  ExternalGeometry = -> [Mirrored002]
  FullyConstrained = true
  MakeInternals = false
  MapMode = 5
  Placement = pos=(22.9533,0.205859,0) rot=(0.573898,0.579069,0.579069;2.09958rad)
  sketch-geometry (2):
    g0: Circle CenterX=0 CenterY=3 CenterZ=0 NormalX=0 NormalY=0 NormalZ=1 AngleXU=0 Radius=1.7
    g1: Circle CenterX=210 CenterY=3 CenterZ=0 NormalX=0 NormalY=0 NormalZ=1 AngleXU=0 Radius=1.7
  constraints (6):
    c: PointOnObject(g0,g-2)
    c: DistanceY(g-1,g0) = 3
    c: Diameter(g0) = 3.4
    c: Diameter(g1) = 3.4
    c: DistanceY(g-3,g1) = 3
    c: DistanceX(g0,g1) = 210
FEATURE [PartDesign::Pocket] Pocket049
  BaseFeature = -> Mirrored002
  Direction = (-0.99996,-0.00896825,-2e-16)
  Length = 5
  Length2 = 5
  Profile = -> Sketch091
  ReferenceAxis = -> Sketch091 [N_Axis]
  Refine = true
  Suppressed = false
  Type = 1
FEATURE [Sketcher::SketchObject] Sketch092
  ArcFitTolerance = 1e-06
  FullyConstrained = true
  MakeInternals = false
  MapMode = 5
  Placement = pos=(0,231,0) rot=(0,0.707107,0.707107;3.14159rad)
  sketch-geometry (1):
    g0: Circle CenterX=0 CenterY=3 CenterZ=0 NormalX=0 NormalY=0 NormalZ=1 AngleXU=0 Radius=2
  constraints (3):
    c: PointOnObject(g0,g-2)
    c: Diameter(g0) = 4
    c: DistanceY(g-1,g0) = 3
FEATURE [PartDesign::Pocket] Pocket050
  BaseFeature = -> Pocket049
  Direction = (0,-1,2e-16)
  Length = 5
  Length2 = 5
  Profile = -> Sketch092
  ReferenceAxis = -> Sketch092 [N_Axis]
  Refine = true
  Suppressed = false
  Type = 0
FEATURE [Sketcher::SketchObject] Sketch093
  ArcFitTolerance = 1e-06
  AttachmentSupport = -> [Pocket050]
  FullyConstrained = false
  MakeInternals = false
  MapMode = 5
  Placement = pos=(0,-21,0) rot=(1,0,0;1.5708rad)
  sketch-geometry (1):
    g0: Circle CenterX=0 CenterY=2.85079 CenterZ=0 NormalX=0 NormalY=0 NormalZ=1 AngleXU=0 Radius=2
  constraints (2):
    c: PointOnObject(g0,g-2)
    c: Diameter(g0) = 4
FEATURE [PartDesign::Pocket] Pocket051
  BaseFeature = -> Pocket050
  Direction = (0,1,-2e-16)
  Length = 6
  Length2 = 5
  Profile = -> Sketch093
  ReferenceAxis = -> Sketch093 [N_Axis]
  Refine = true
  Suppressed = false
  Type = 0
FEATURE [Sketcher::SketchObject] Sketch094
  ArcFitTolerance = 1e-06
  AttachmentSupport = -> [XY_Plane036]
  FullyConstrained = false
  MakeInternals = false
  MapMode = 5
  sketch-geometry (44):
    g0: LineSegment StartX=-23 StartY=-5 StartZ=0 EndX=-21 EndY=218 EndZ=0
    g1: LineSegment StartX=23 StartY=-5 StartZ=0 EndX=21 EndY=218 EndZ=0
    g2: Circle CenterX=3.46e-14 CenterY=211 CenterZ=0 NormalX=0 NormalY=0 NormalZ=1 AngleXU=0 Radius=8
    g3: Circle CenterX=0 CenterY=-141.268 CenterZ=0 NormalX=0 NormalY=0 NormalZ=1 AngleXU=0 Radius=9.71
    g4: Circle CenterX=0 CenterY=0 CenterZ=0 NormalX=0 NormalY=0 NormalZ=1 AngleXU=0 Radius=12.5
    g5: LineSegment StartX=-7 StartY=232 StartZ=0 EndX=7 EndY=232 EndZ=0
    g6: ArcOfCircle CenterX=3.46e-14 CenterY=211 CenterZ=0 NormalX=0 NormalY=0 NormalZ=1 AngleXU=0 Radius=22.1359 StartAngle=1.89255 EndAngle=2.81984
    g7: ArcOfCircle CenterX=3.46e-14 CenterY=211 CenterZ=0 NormalX=0 NormalY=0 NormalZ=1 AngleXU=0 Radius=22.1359 StartAngle=0.321751 EndAngle=1.24905
    g8: LineSegment StartX=-10.6301 StartY=-21 StartZ=0 EndX=10.6301 EndY=-21 EndZ=0
    g9: ArcOfCircle CenterX=0 CenterY=0 CenterZ=0 NormalX=0 NormalY=0 NormalZ=1 AngleXU=0 Radius=23.5372 StartAngle=3.35565 EndAngle=4.2438
    g10: ArcOfCircle CenterX=0 CenterY=0 CenterZ=0 NormalX=0 NormalY=0 NormalZ=1 AngleXU=0 Radius=23.5372 StartAngle=5.18098 EndAngle=6.06912
    g11: LineSegment [constr] StartX=-22.417 StartY=60 StartZ=0 EndX=22.417 EndY=60 EndZ=0
    g12: GeomPoint [constr] X=32.4275 Y=0 Z=0
    g13: GeomPoint [constr] X=21.5202 Y=160 Z=0
    g14: LineSegment [constr] StartX=21.5202 StartY=160 StartZ=0 EndX=-21.5202 EndY=160 EndZ=0
    g15: GeomPoint [constr] X=18.5202 Y=160 Z=0
    g16: GeomPoint [constr] X=-18.5202 Y=160 Z=0
    g17: GeomPoint [constr] X=-19.417 Y=60 Z=0
    g18: GeomPoint [constr] X=19.417 Y=60 Z=0
    g19: LineSegment StartX=16.6 StartY=3.25 StartZ=0 EndX=16.6 EndY=-3.25 EndZ=0
    g20: LineSegment StartX=16.6 StartY=-3.25 StartZ=0 EndX=19.4 EndY=-3.25 EndZ=0
    g21: LineSegment StartX=19.4 StartY=-3.25 StartZ=0 EndX=19.4 EndY=3.25 EndZ=0
    g22: LineSegment StartX=19.4 StartY=3.25 StartZ=0 EndX=16.6 EndY=3.25 EndZ=0
    g23: GeomPoint [constr] X=18 Y=0 Z=0
    g24: LineSegment StartX=-19.4 StartY=3.25 StartZ=0 EndX=-19.4 EndY=-3.25 EndZ=0
    g25: LineSegment StartX=-19.4 StartY=-3.25 StartZ=0 EndX=-16.6 EndY=-3.25 EndZ=0
    g26: LineSegment StartX=-16.6 StartY=-3.25 StartZ=0 EndX=-16.6 EndY=3.25 EndZ=0
    g27: LineSegment StartX=-16.6 StartY=3.25 StartZ=0 EndX=-19.4 EndY=3.25 EndZ=0
    g28: GeomPoint [constr] X=-18 Y=0 Z=0
    g29: LineSegment [constr] StartX=-13.769 StartY=211 StartZ=0 EndX=13.769 EndY=211 EndZ=0
    g30: LineSegment StartX=12.369 StartY=214.25 StartZ=0 EndX=12.369 EndY=207.75 EndZ=0
    g31: LineSegment StartX=12.369 StartY=207.75 StartZ=0 EndX=15.169 EndY=207.75 EndZ=0
    g32: LineSegment StartX=15.169 StartY=207.75 StartZ=0 EndX=15.169 EndY=214.25 EndZ=0
    g33: LineSegment StartX=15.169 StartY=214.25 StartZ=0 EndX=12.369 EndY=214.25 EndZ=0
    g34: GeomPoint [constr] X=13.769 Y=211 Z=0
    g35: LineSegment StartX=-15.169 StartY=214.25 StartZ=0 EndX=-15.169 EndY=207.75 EndZ=0
    g36: LineSegment StartX=-15.169 StartY=207.75 StartZ=0 EndX=-12.369 EndY=207.75 EndZ=0
    g37: LineSegment StartX=-12.369 StartY=207.75 StartZ=0 EndX=-12.369 EndY=214.25 EndZ=0
    g38: LineSegment StartX=-12.369 StartY=214.25 StartZ=0 EndX=-15.169 EndY=214.25 EndZ=0
    g39: GeomPoint [constr] X=-13.769 Y=211 Z=0
    g40: Circle CenterX=18.5202 CenterY=160 CenterZ=0 NormalX=0 NormalY=0 NormalZ=1 AngleXU=0 Radius=1.7
    g41: Circle CenterX=-18.5202 CenterY=160 CenterZ=0 NormalX=0 NormalY=0 NormalZ=1 AngleXU=0 Radius=1.7
    g42: Circle CenterX=-19.417 CenterY=60 CenterZ=0 NormalX=0 NormalY=0 NormalZ=1 AngleXU=0 Radius=1.7
    g43: Circle CenterX=19.417 CenterY=60 CenterZ=0 NormalX=0 NormalY=0 NormalZ=1 AngleXU=0 Radius=1.7
  constraints (106):
    c: PointOnObject(g3,g-2)
    c: Symmetric(g5,g5,g-2)
    c: DistanceY(g2,g5) = 21
    c: Coincident(g6,g2)
    c: Coincident(g6,g5)
    c: Coincident(g6,g0)
    c: Coincident(g7,g2)
    c: Coincident(g7,g5)
    c: Coincident(g7,g1)
    c: Symmetric(g8,g8,g-2)
    c: DistanceY(g8,g4) = 21
    c: PointOnObject(g4,g-2)
    c: PointOnObject(g4,g-1)
    c: Coincident(g9,g4)
    c: Coincident(g9,g0)
    c: Coincident(g9,g8)
    c: Coincident(g10,g4)
    c: Coincident(g10,g1)
    c: Coincident(g10,g8)
    c: PointOnObject(g12,g-1)
    c: DistanceY(g12,g11) = 60
    c: DistanceY(g12,g13) = 160
    c: DistanceY(g12,g2) = 211
    c: Diameter(g4) = 25
    c: Diameter(g2) = 16
    c: Horizontal(g0,g1)
    c: DistanceX(g0,g1) = 46
    c: DistanceY(g0,g4) = 5
    c: Symmetric(g0,g1,g-2)
    c: DistanceX(g0,g1) = 42
    c: DistanceY(g2,g1) = 7
    c: Coincident(g14,g13)
    c: Horizontal(g14)
    c: PointOnObject(g13,g1)
    c: PointOnObject(g15,g14)
    c: DistanceX(g15,g13) = 3
    c: PointOnObject(g14,g0)
    c: PointOnObject(g16,g14)
    c: DistanceX(g14,g16) = 3
    c: PointOnObject(g11,g1)
    c: Horizontal(g11)
    c: PointOnObject(g11,g0)
    c: PointOnObject(g17,g11)
    c: PointOnObject(g18,g11)
    c: DistanceX(g18,g11) = 3
    c: DistanceX(g11,g17) = 3
    c: Coincident(g19,g20)
    c: Coincident(g20,g21)
    c: Coincident(g21,g22)
    c: Coincident(g22,g19)
    c: Vertical(g19)
    c: Vertical(g21)
    c: Horizontal(g20)
    c: Horizontal(g22)
    c: Symmetric(g21,g19,g23)
    c: PointOnObject(g23,g-1)
    c: Coincident(g24,g25)
    c: Coincident(g25,g26)
    c: Coincident(g26,g27)
    c: Coincident(g27,g24)
    c: Vertical(g24)
    c: Vertical(g26)
    c: Horizontal(g25)
    c: Horizontal(g27)
    c: Symmetric(g26,g24,g28)
    c: PointOnObject(g28,g-1)
    c: DistanceX(g24,g26) = 2.8
    c: DistanceY(g25,g26) = 6.5
    c: Equal(g26,g19)
    c: Equal(g22,g27)
    c: DistanceX(g28,g4) = 18
    c: DistanceX(g4,g23) = 18
    c: PointOnObject(g2,g29)
    c: Coincident(g30,g31)
    c: Coincident(g31,g32)
    c: Coincident(g32,g33)
    c: Coincident(g33,g30)
    c: Vertical(g30)
    c: Vertical(g32)
    c: Horizontal(g31)
    c: Horizontal(g33)
    c: Symmetric(g32,g30,g34)
    c: Coincident(g34,g29)
    c: Coincident(g35,g36)
    c: Coincident(g36,g37)
    c: Coincident(g37,g38)
    c: Coincident(g38,g35)
    c: Vertical(g35)
    c: Vertical(g37)
    c: Horizontal(g36)
    c: Horizontal(g38)
    c: Symmetric(g37,g35,g39)
    c: Coincident(g39,g29)
    c: DistanceX(g35,g36) = 2.8
    c: DistanceY(g36,g37) = 6.5
    c: Symmetric(g29,g29,g-2)
    c: Equal(g37,g30)
    c: Equal(g38,g33)
    c: Coincident(g40,g15)
    c: Coincident(g41,g16)
    c: Coincident(g42,g17)
    c: Coincident(g43,g18)
    c: Equal(g43,g42)
    c: Equal(g43,g41)
    c: Equal(g43,g40)
    c: Diameter(g43) = 3.4
FEATURE [PartDesign::Pad] Pad031
  Direction = (0,0,1)
  Length = 6
  Length2 = 10
  Profile = -> Sketch094
  ReferenceAxis = -> Sketch094 [N_Axis]
  Refine = true
  Suppressed = false
  Type = 0
FEATURE [Sketcher::SketchObject] Sketch095
  ArcFitTolerance = 1e-06
  AttachmentSupport = -> [Pad031]
  ExternalGeometry = -> [Pad031]
  FullyConstrained = false
  MakeInternals = false
  MapMode = 5
  Placement = pos=(0,0,6) rot=(0,0,1;0rad)
  sketch-geometry (39):
    g0: LineSegment [constr] StartX=3 StartY=-5.21478 StartZ=0 EndX=3 EndY=239.543 EndZ=0
    g1: LineSegment [constr] StartX=16.2164 StartY=193.83 StartZ=0 EndX=18.2096 EndY=-28.4148 EndZ=0
    g2: LineSegment [constr] StartX=16.2164 StartY=193.83 StartZ=0 EndX=21.2164 EndY=193.875 EndZ=0
    g3: GeomPoint [constr] X=0 Y=232.447 Z=0
    g4: LineSegment StartX=4.6615 StartY=65.3281 StartZ=0 EndX=15.4077 EndY=65.3281 EndZ=0
    g5: LineSegment StartX=17.3513 StartY=67.2892 StartZ=0 EndX=16.9765 EndY=109.08 EndZ=0
    g6: LineSegment StartX=14.8734 StartY=111.164 StartZ=0 EndX=3 EndY=111.164 EndZ=0
    g7: LineSegment StartX=3 StartY=111.164 StartZ=0 EndX=3 EndY=66.9896 EndZ=0
    g8: LineSegment StartX=15.3443 StartY=117.164 StartZ=0 EndX=4.83374 EndY=117.164 EndZ=0
    g9: LineSegment StartX=3 StartY=118.998 StartZ=0 EndX=3 EndY=155.171 EndZ=0
    g10: LineSegment StartX=4.82861 StartY=157 StartZ=0 EndX=14.4816 EndY=157 EndZ=0
    g11: LineSegment StartX=16.5652 StartY=154.935 StartZ=0 EndX=16.89 EndY=118.724 EndZ=0
    g12: LineSegment StartX=5.29936 StartY=163 StartZ=0 EndX=15.3637 EndY=163 EndZ=0
    g13: LineSegment StartX=16.4827 StartY=164.129 StartZ=0 EndX=16.2547 EndY=189.554 EndZ=0
    g14: LineSegment StartX=14.4184 StartY=190.98 StartZ=0 EndX=4.63228 EndY=188.571 EndZ=0
    g15: LineSegment StartX=3 StartY=186.488 StartZ=0 EndX=3 EndY=165.299 EndZ=0
    g16: LineSegment [constr] StartX=3 StartY=111.164 StartZ=0 EndX=-6.77105 EndY=111.164 EndZ=0
    g17: ArcOfCircle CenterX=15.4077 CenterY=67.2718 CenterZ=0 NormalX=0 NormalY=0 NormalZ=1 AngleXU=0 Radius=1.94366 StartAngle=4.71239 EndAngle=6.29215
    g18: GeomPoint [constr] X=17.3689 Y=65.3281 Z=0
    g19: ArcOfCircle CenterX=4.6615 CenterY=66.9896 CenterZ=0 NormalX=0 NormalY=0 NormalZ=1 AngleXU=0 Radius=1.6615 StartAngle=3.14159 EndAngle=4.71239
    g20: GeomPoint [constr] X=3 Y=65.3281 Z=0
    g21: ArcOfCircle CenterX=4.83374 CenterY=118.998 CenterZ=0 NormalX=0 NormalY=0 NormalZ=1 AngleXU=0 Radius=1.83374 StartAngle=3.14159 EndAngle=4.71239
    g22: GeomPoint [constr] X=3 Y=117.164 Z=0
    g23: ArcOfCircle CenterX=14.8734 CenterY=109.061 CenterZ=0 NormalX=0 NormalY=0 NormalZ=1 AngleXU=0 Radius=2.10314 StartAngle=0.00896837 EndAngle=1.5708
    g24: GeomPoint [constr] X=16.9578 Y=111.164 Z=0
    g25: ArcOfCircle CenterX=15.3443 CenterY=118.71 CenterZ=0 NormalX=0 NormalY=0 NormalZ=1 AngleXU=0 Radius=1.54577 StartAngle=4.71239 EndAngle=6.29215
    g26: GeomPoint [constr] X=16.904 Y=117.164 Z=0
    g27: ArcOfCircle CenterX=14.4816 CenterY=154.916 CenterZ=0 NormalX=0 NormalY=0 NormalZ=1 AngleXU=0 Radius=2.08369 StartAngle=0.00896837 EndAngle=1.5708
    g28: GeomPoint [constr] X=16.5467 Y=157 Z=0
    g29: ArcOfCircle CenterX=4.82861 CenterY=155.171 CenterZ=0 NormalX=0 NormalY=0 NormalZ=1 AngleXU=0 Radius=1.82861 StartAngle=1.5708 EndAngle=3.14159
    g30: GeomPoint [constr] X=3 Y=157 Z=0
    g31: ArcOfCircle CenterX=5.29936 CenterY=165.299 CenterZ=0 NormalX=0 NormalY=0 NormalZ=1 AngleXU=0 Radius=2.29936 StartAngle=3.14159 EndAngle=4.71239
    g32: GeomPoint [constr] X=3 Y=163 Z=0
    g33: ArcOfCircle CenterX=15.3637 CenterY=164.119 CenterZ=0 NormalX=0 NormalY=0 NormalZ=1 AngleXU=0 Radius=1.1191 StartAngle=4.71239 EndAngle=6.29215
    g34: GeomPoint [constr] X=16.4929 Y=163 Z=0
    g35: ArcOfCircle CenterX=5.14502 CenterY=186.488 CenterZ=0 NormalX=0 NormalY=0 NormalZ=1 AngleXU=0 Radius=2.14502 StartAngle=1.81217 EndAngle=3.14159
    g36: GeomPoint [constr] X=3 Y=188.169 Z=0
    g37: ArcOfCircle CenterX=14.7727 CenterY=189.541 CenterZ=0 NormalX=0 NormalY=0 NormalZ=1 AngleXU=0 Radius=1.48209 StartAngle=0.00896837 EndAngle=1.81217
    g38: GeomPoint [constr] X=16.2379 Y=191.428 Z=0
  constraints (75):
    c: Vertical(g0)
    c: Parallel(g1,g-3)
    c: Coincident(g2,g1)
    c: Perpendicular(g2,g1)
    c: PointOnObject(g2,g-3)
    c: DistanceX(g1,g2) = 5
    c: PointOnObject(g3,g-2)
    c: DistanceX(g3,g0) = 3
    c: PointOnObject(g20,g0)
    c: PointOnObject(g18,g1)
    c: Horizontal(g4)
    c: Horizontal(g6)
    c: Coincident(g6,g7)
    c: PointOnObject(g26,g1)
    c: Symmetric(g0,g0,g22)
    c: PointOnObject(g28,g1)
    c: Horizontal(g8)
    c: PointOnObject(g6,g0)
    c: PointOnObject(g24,g1)
    c: DistanceY(g24,g26) = 6
    c: PointOnObject(g30,g0)
    c: Horizontal(g10)
    c: PointOnObject(g32,g0)
    c: PointOnObject(g34,g1)
    c: PointOnObject(g36,g0)
    c: Horizontal(g12)
    c: DistanceY(g28,g34) = 6
    c: PointOnObject(g38,g1)
    c: Coincident(g16,g6)
    c: Symmetric(g20,g30,g16)
    c: PointOnObject(g18,g4)
    c: PointOnObject(g18,g5)
    c: Tangent(g4,g17) = -1.5708
    c: Tangent(g5,g17) = -1.5708
    c: PointOnObject(g20,g4)
    c: PointOnObject(g20,g7)
    c: Tangent(g4,g19) = -1.5708
    c: Tangent(g7,g19) = -1.5708
    c: PointOnObject(g22,g8)
    c: PointOnObject(g22,g9)
    c: Tangent(g8,g21) = 1.5708
    c: Tangent(g9,g21) = 1.5708
    c: PointOnObject(g24,g5)
    c: PointOnObject(g24,g6)
    c: Tangent(g5,g23) = -1.5708
    c: Tangent(g6,g23) = -1.5708
    c: PointOnObject(g26,g8)
    c: PointOnObject(g26,g11)
    c: Tangent(g8,g25) = 1.5708
    c: Tangent(g11,g25) = 1.5708
    c: PointOnObject(g28,g10)
    c: PointOnObject(g28,g11)
    c: Tangent(g10,g27) = 1.5708
    c: Tangent(g11,g27) = 1.5708
    c: PointOnObject(g30,g9)
    c: PointOnObject(g30,g10)
    c: Tangent(g9,g29) = 1.5708
    c: Tangent(g10,g29) = 1.5708
    c: PointOnObject(g32,g12)
    c: PointOnObject(g32,g15)
    c: Tangent(g12,g31) = -1.5708
    c: Tangent(g15,g31) = -1.5708
    c: PointOnObject(g34,g12)
    c: PointOnObject(g34,g13)
    c: Tangent(g12,g33) = -1.5708
    c: Tangent(g13,g33) = -1.5708
    c: PointOnObject(g36,g14)
    c: PointOnObject(g36,g15)
    c: Tangent(g14,g35) = -1.5708
    c: Tangent(g15,g35) = -1.5708
    c: PointOnObject(g38,g13)
    c: PointOnObject(g38,g14)
    c: Tangent(g13,g37) = -1.5708
    c: Tangent(g14,g37) = -1.5708
    c: DistanceY(g-1,g10) = 157
FEATURE [PartDesign::Pocket] Pocket052  label="CARVINGS"
  BaseFeature = -> Pad031
  Direction = (0,0,-1)
  Length = 5
  Length2 = 5
  Profile = -> Sketch095
  ReferenceAxis = -> Sketch095 [N_Axis]
  Refine = true
  Suppressed = false
  Type = 1
FEATURE [PartDesign::Mirrored] Mirrored003
  BaseFeature = -> Pocket052
  MirrorPlane = -> Sketch095 [V_Axis]
  Originals = -> [Pocket052]
  Refine = true
  Suppressed = false
  TransformMode = 0
FEATURE [Sketcher::SketchObject] Sketch096
  ArcFitTolerance = 1e-06
  AttachmentSupport = -> [Mirrored003]
  ExternalGeometry = -> [Mirrored003]
  FullyConstrained = true
  MakeInternals = false
  MapMode = 5
  Placement = pos=(22.9533,0.205859,0) rot=(0.573898,0.579069,0.579069;2.09958rad)
  sketch-geometry (2):
    g0: Circle CenterX=0 CenterY=3 CenterZ=0 NormalX=0 NormalY=0 NormalZ=1 AngleXU=0 Radius=1.7
    g1: Circle CenterX=210 CenterY=3 CenterZ=0 NormalX=0 NormalY=0 NormalZ=1 AngleXU=0 Radius=1.7
  constraints (6):
    c: PointOnObject(g0,g-2)
    c: DistanceY(g-1,g0) = 3
    c: Diameter(g0) = 3.4
    c: Diameter(g1) = 3.4
    c: DistanceY(g-3,g1) = 3
    c: DistanceX(g0,g1) = 210
FEATURE [PartDesign::Pocket] Pocket053
  BaseFeature = -> Mirrored003
  Direction = (-0.99996,-0.00896825,-2e-16)
  Length = 5
  Length2 = 5
  Profile = -> Sketch096
  ReferenceAxis = -> Sketch096 [N_Axis]
  Refine = true
  Suppressed = false
  Type = 1
FEATURE [PartDesign::Chamfer] Chamfer020
  Angle = 45
  Base = -> Pocket053 [Edge168]
  BaseFeature = -> Pocket053
  ChamferType = 0
  FlipDirection = false
  Refine = true
  Size = 1
  Size2 = 1
  SupportTransform = false
  Suppressed = false
  UseAllEdges = false
FEATURE [PartDesign::Chamfer] Chamfer021
  Angle = 45
  Base = -> Chamfer020 [Edge6]
  BaseFeature = -> Chamfer020
  ChamferType = 0
  FlipDirection = false
  Refine = true
  Size = 1
  Size2 = 1
  SupportTransform = false
  Suppressed = false
  UseAllEdges = false
FEATURE [Sketcher::SketchObject] Sketch097
  ArcFitTolerance = 1e-06
  FullyConstrained = true
  MakeInternals = false
  MapMode = 5
  Placement = pos=(0,231,0) rot=(0,0.707107,0.707107;3.14159rad)
  sketch-geometry (1):
    g0: Circle CenterX=0 CenterY=3 CenterZ=0 NormalX=0 NormalY=0 NormalZ=1 AngleXU=0 Radius=2
  constraints (3):
    c: PointOnObject(g0,g-2)
    c: Diameter(g0) = 4
    c: DistanceY(g-1,g0) = 3
FEATURE [PartDesign::Pocket] Pocket054
  BaseFeature = -> Chamfer021
  Direction = (0,-1,2e-16)
  Length = 5
  Length2 = 5
  Profile = -> Sketch097
  ReferenceAxis = -> Sketch097 [N_Axis]
  Refine = true
  Suppressed = false
  Type = 0
FEATURE [Sketcher::SketchObject] Sketch098
  ArcFitTolerance = 1e-06
  AttachmentSupport = -> [Pocket054]
  FullyConstrained = false
  MakeInternals = false
  MapMode = 5
  Placement = pos=(-3.6e-15,-21,0) rot=(1,0,0;1.5708rad)
  sketch-geometry (1):
    g0: Circle CenterX=0 CenterY=2.85079 CenterZ=0 NormalX=0 NormalY=0 NormalZ=1 AngleXU=0 Radius=2
  constraints (2):
    c: PointOnObject(g0,g-2)
    c: Diameter(g0) = 4
FEATURE [PartDesign::Pocket] Pocket055
  BaseFeature = -> Pocket054
  Direction = (0,1,-2e-16)
  Length = 6
  Length2 = 5
  Profile = -> Sketch098
  ReferenceAxis = -> Sketch098 [N_Axis]
  Refine = true
  Suppressed = false
  Type = 0
FEATURE [Sketcher::SketchObject] Sketch099
  ArcFitTolerance = 1e-06
  AttachmentSupport = -> [Pocket055]
  ExternalGeometry = -> [Pocket055]
  FullyConstrained = true
  MakeInternals = false
  MapMode = 5
  Placement = pos=(0,0,6) rot=(0,0,1;0rad)
  sketch-geometry (1):
    g0: LineSegment StartX=0 StartY=0 StartZ=0 EndX=16.6433 EndY=-16.6433 EndZ=0
  constraints (3):
    c: Coincident(g0,g-1)
    c: PointOnObject(g0,g-3)
    c: Angle(g0,g-1) = 0.785398
FEATURE [PartDesign::Plane] DatumPlane
  AttachmentSupport = -> [Sketch099]
  Length = 237.918
  MapMode = 7
  Placement = pos=(16.6433,-16.6433,6) rot=(-0.281085,0.678598,0.678598;3.68962rad)
  ResizeMode = 0
  Width = 70.8366
FEATURE [Sketcher::SketchObject] Sketch100
  ArcFitTolerance = 1e-06
  AttachmentSupport = -> [DatumPlane]
  FullyConstrained = true
  MakeInternals = false
  MapMode = 5
  Placement = pos=(16.6433,-16.6433,6) rot=(-0.281085,0.678598,0.678598;3.68962rad)
  sketch-geometry (1):
    g0: Circle CenterX=0 CenterY=-3 CenterZ=0 NormalX=0 NormalY=0 NormalZ=1 AngleXU=0 Radius=2
  constraints (3):
    c: PointOnObject(g0,g-2)
    c: Diameter(g0) = 4
    c: Distance(g0,g-1) = 3
FEATURE [PartDesign::Pocket] Pocket056
  BaseFeature = -> Pocket055
  Direction = (0.707107,-0.707107,0)
  Length = 24
  Length2 = 5
  Profile = -> Sketch100
  ReferenceAxis = -> Sketch100 [N_Axis]
  Refine = true
  Reversed = true
  Suppressed = false
  Type = 0
FEATURE [Sketcher::SketchObject] Sketch101
  ArcFitTolerance = 1e-06
  AttachmentSupport = -> [Pocket056]
  ExternalGeometry = -> [Pocket056]
  FullyConstrained = true
  MakeInternals = false
  MapMode = 5
  Placement = pos=(0,0,6) rot=(0,0,1;0rad)
  sketch-geometry (1):
    g0: LineSegment StartX=0 StartY=0 StartZ=0 EndX=-16.6433 EndY=-16.6433 EndZ=0
  constraints (3):
    c: Coincident(g0,g-1)
    c: PointOnObject(g0,g-3)
    c: Angle(g0,g-1) = 2.35619
FEATURE [PartDesign::Plane] DatumPlane001
  AttachmentSupport = -> [Sketch101]
  Length = 237.918
  MapMode = 7
  Placement = pos=(-16.6433,-16.6433,6) rot=(0.281085,0.678598,0.678598;2.59356rad)
  ResizeMode = 0
  Width = 70.8366
FEATURE [Sketcher::SketchObject] Sketch102
  ArcFitTolerance = 1e-06
  AttachmentSupport = -> [DatumPlane001]
  FullyConstrained = true
  MakeInternals = false
  MapMode = 5
  Placement = pos=(-16.6433,-16.6433,6) rot=(0.281085,0.678598,0.678598;2.59356rad)
  sketch-geometry (1):
    g0: Circle CenterX=0 CenterY=-3 CenterZ=0 NormalX=0 NormalY=0 NormalZ=1 AngleXU=0 Radius=2
  constraints (3):
    c: PointOnObject(g0,g-2)
    c: Diameter(g0) = 4
    c: DistanceY(g0,g-1) = 3
FEATURE [PartDesign::Pocket] Pocket057
  BaseFeature = -> Pocket056
  Direction = (-0.707107,-0.707107,-2e-16)
  Length = 20
  Length2 = 5
  Profile = -> Sketch102
  ReferenceAxis = -> Sketch102 [N_Axis]
  Refine = true
  Reversed = true
  Suppressed = false
  Type = 0
FEATURE [Part::Feature] Part__Feature017  label="GT2_40T_8_6"
  Placement = pos=(0,0,-15) rot=(0,0,1;0rad)
  shape: bbox 30.31 x 30.31 x 15 mm, 348 faces (baked)
FEATURE [Part::Feature] Part__Feature018  label="GT2_40T_8_007"
  Placement = pos=(0,210,-15) rot=(0,0,1;0rad)
  shape: bbox 30.31 x 30.31 x 15 mm, 348 faces (baked)
FEATURE [Sketcher::SketchObject] Sketch103
  ArcFitTolerance = 1e-06
  AttachmentSupport = -> [YZ_Plane037]
  FullyConstrained = false
  MakeInternals = false
  MapMode = 5
  Placement = pos=(0,0,0) rot=(0.57735,0.57735,0.57735;2.0944rad)
  sketch-geometry (6):
    g0: LineSegment StartX=10 StartY=0 StartZ=0 EndX=199.942 EndY=0 EndZ=0
    g1: LineSegment StartX=199.942 StartY=0 StartZ=0 EndX=199.942 EndY=30 EndZ=0
    g2: LineSegment StartX=199.942 StartY=30 StartZ=0 EndX=10 EndY=30 EndZ=0
    g3: LineSegment StartX=10 StartY=30 StartZ=0 EndX=10 EndY=0 EndZ=0
    g4: GeomPoint X=0 Y=37.4701 Z=0
    g5: LineSegment [constr] StartX=209.942 StartY=39.0944 StartZ=0 EndX=209.942 EndY=7.07331 EndZ=0
  constraints (15):
    c: Coincident(g0,g1)
    c: Coincident(g1,g2)
    c: Coincident(g2,g3)
    c: Coincident(g3,g0)
    c: Horizontal(g0)
    c: Horizontal(g2)
    c: Vertical(g1)
    c: Vertical(g3)
    c: PointOnObject(g4,g-2)
    c: DistanceX(g4,g2) = 10
    c: DistanceY(g0,g1) = 30
    c: Vertical(g5)
    c: DistanceX(g1,g5) = 10
    c: Block(g5)
    c: PointOnObject(g0,g-1)
FEATURE [PartDesign::Pad] Pad032
  Direction = (1,0,0)
  Length = 12
  Length2 = 10
  Midplane = true
  Placement = pos=(0,0,0) rot=(1,1,1;2.0944rad)
  Profile = -> Sketch103
  ReferenceAxis = -> Sketch103 [N_Axis]
  Refine = true
  Suppressed = false
  Type = 0
FEATURE [Sketcher::SketchObject] Sketch104
  ArcFitTolerance = 1e-06
  AttachmentSupport = -> [Pad032]
  ExternalGeometry = -> [Pad032]
  FullyConstrained = false
  MakeInternals = false
  MapMode = 5
  Placement = pos=(2.2e-15,10,0) rot=(0.57735,0.57735,-0.57735;2.0944rad)
  sketch-geometry (9):
    g0: LineSegment [constr] StartX=-40.2302 StartY=4 StartZ=0 EndX=11.0556 EndY=4 EndZ=0
    g1: LineSegment StartX=-40.2302 StartY=4 StartZ=0 EndX=-40.2302 EndY=-9.83045 EndZ=0
    g2: LineSegment StartX=-40.2302 StartY=-9.83045 StartZ=0 EndX=-24 EndY=-9.83045 EndZ=0
    g3: LineSegment StartX=-24 StartY=-9.83045 StartZ=0 EndX=-24 EndY=4 EndZ=0
    g4: LineSegment StartX=-24 StartY=4 StartZ=0 EndX=-40.2302 EndY=4 EndZ=0
    g5: LineSegment StartX=11.0556 StartY=4 StartZ=0 EndX=-6 EndY=4 EndZ=0
    g6: LineSegment StartX=-6 StartY=4 StartZ=0 EndX=-6 EndY=-7.94705 EndZ=0
    g7: LineSegment StartX=-6 StartY=-7.94705 StartZ=0 EndX=11.0556 EndY=-7.94705 EndZ=0
    g8: LineSegment StartX=11.0556 StartY=-7.94705 StartZ=0 EndX=11.0556 EndY=4 EndZ=0
  constraints (22):
    c: Horizontal(g0)
    c: DistanceY(g0,g-4) = 2
    c: Coincident(g1,g2)
    c: Coincident(g2,g3)
    c: Coincident(g3,g4)
    c: Coincident(g4,g1)
    c: Vertical(g1)
    c: Vertical(g3)
    c: Horizontal(g2)
    c: Horizontal(g4)
    c: Coincident(g1,g0)
    c: Coincident(g5,g6)
    c: Coincident(g6,g7)
    c: Coincident(g7,g8)
    c: Coincident(g8,g5)
    c: Horizontal(g5)
    c: Horizontal(g7)
    c: Vertical(g6)
    c: Vertical(g8)
    c: Coincident(g5,g0)
    c: DistanceX(g5,g-1) = 6
    c: DistanceX(g-5,g3) = 6
FEATURE [PartDesign::Pocket] Pocket058
  BaseFeature = -> Pad032
  Direction = (0,1,0)
  Length = 5
  Length2 = 5
  Placement = pos=(0,0,0) rot=(1,1,1;2.0944rad)
  Profile = -> Sketch104
  ReferenceAxis = -> Sketch104 [N_Axis]
  Refine = true
  Suppressed = false
  Type = 1
FEATURE [Sketcher::SketchObject] Sketch105
  ArcFitTolerance = 1e-06
  AttachmentSupport = -> [Pocket058]
  ExternalGeometry = -> [Pocket058]
  FullyConstrained = false
  MakeInternals = false
  MapMode = 5
  Placement = pos=(0,5.3e-15,24) rot=(0,0,-1;1.5708rad)
  sketch-geometry (17):
    g0: LineSegment [constr] StartX=-60 StartY=0.8 StartZ=0 EndX=-60 EndY=10.563 EndZ=0
    g1: LineSegment [constr] StartX=-160 StartY=0.8 StartZ=0 EndX=-160 EndY=11.6219 EndZ=0
    g2: Circle CenterX=-160 CenterY=0.8 CenterZ=0 NormalX=0 NormalY=0 NormalZ=1 AngleXU=0 Radius=1.8
    g3: Circle CenterX=-60 CenterY=0.8 CenterZ=0 NormalX=0 NormalY=0 NormalZ=1 AngleXU=0 Radius=1.8
    g4: LineSegment StartX=-5.7972 StartY=0 StartZ=0 EndX=-55.3173 EndY=-4e-16 EndZ=0
    g5: LineSegment StartX=-155.481 StartY=0 StartZ=0 EndX=-64.3371 EndY=-4e-16 EndZ=0
    g6: LineSegment StartX=-163.912 StartY=0 StartZ=0 EndX=-224.776 EndY=0 EndZ=0
    g7: GeomPoint X=0 Y=14.3735 Z=0
    g8: LineSegment StartX=-224.776 StartY=0 StartZ=0 EndX=-146.784 EndY=-56.3724 EndZ=0
    g9: LineSegment StartX=-146.784 StartY=-56.3724 StartZ=0 EndX=-2.14325 EndY=-56.3724 EndZ=0
    g10: LineSegment StartX=-2.14325 StartY=-56.3724 StartZ=0 EndX=-5.7972 EndY=0 EndZ=0
    g11: LineSegment StartX=-64.3371 StartY=-4e-16 StartZ=0 EndX=-62.0154 EndY=-3.89222 EndZ=0
    g12: LineSegment StartX=-62.0154 StartY=-3.89222 StartZ=0 EndX=-57.8077 EndY=-3.89222 EndZ=0
    g13: LineSegment StartX=-57.8077 StartY=-3.89222 StartZ=0 EndX=-55.3173 EndY=-4e-16 EndZ=0
    g14: LineSegment StartX=-163.912 StartY=0 StartZ=0 EndX=-161.803 EndY=-3.87702 EndZ=0
    g15: LineSegment StartX=-161.803 StartY=-3.87702 StartZ=0 EndX=-157.913 EndY=-3.87702 EndZ=0
    g16: LineSegment StartX=-157.913 StartY=-3.87702 StartZ=0 EndX=-155.481 EndY=0 EndZ=0
  constraints (30):
    c: Vertical(g1)
    c: Vertical(g0)
    c: Coincident(g2,g1)
    c: Coincident(g3,g0)
    c: Diameter(g3) = 3.6
    c: PointOnObject(g7,g-2)
    c: DistanceX(g1,g7) = 160
    c: Coincident(g8,g6)
    c: Coincident(g9,g8)
    c: Horizontal(g9)
    c: Coincident(g10,g9)
    c: Coincident(g10,g4)
    c: DistanceX(g0,g7) = 60
    c: Horizontal(g6)
    c: Coincident(g5,g11)
    c: Coincident(g11,g12)
    c: Coincident(g12,g13)
    c: Coincident(g13,g4)
    c: Coincident(g6,g14)
    c: Coincident(g14,g15)
    c: Coincident(g15,g16)
    c: Coincident(g16,g5)
    c: Horizontal(g6,g5)
    c: Horizontal(g5,g4)
    c: PointOnObject(g6,g-1)
    c: DistanceY(g-1,g-3) = 4
    c: PointOnObject(g4,g-1)
    c: DistanceY(g0,g-5) = 3.2
    c: Horizontal(g1,g0)
    c: PointOnObject(g4,g-1)
FEATURE [PartDesign::Pocket] Pocket059
  BaseFeature = -> Pocket058
  Direction = (0,0,-1)
  Length = 5
  Length2 = 5
  Placement = pos=(0,0,0) rot=(1,1,1;2.0944rad)
  Profile = -> Sketch105
  ReferenceAxis = -> Sketch105 [N_Axis]
  Refine = true
  Suppressed = false
  Type = 1
FEATURE [Sketcher::SketchObject] Sketch107
  ArcFitTolerance = 1e-06
  AttachmentSupport = -> [YZ_Plane038]
  FullyConstrained = false
  MakeInternals = false
  MapMode = 5
  Placement = pos=(0,0,0) rot=(0.57735,0.57735,0.57735;2.0944rad)
  sketch-geometry (6):
    g0: LineSegment StartX=10 StartY=0 StartZ=0 EndX=199.942 EndY=0 EndZ=0
    g1: LineSegment StartX=199.942 StartY=0 StartZ=0 EndX=199.942 EndY=30 EndZ=0
    g2: LineSegment StartX=199.942 StartY=30 StartZ=0 EndX=10 EndY=30 EndZ=0
    g3: LineSegment StartX=10 StartY=30 StartZ=0 EndX=10 EndY=0 EndZ=0
    g4: GeomPoint X=0 Y=37.4701 Z=0
    g5: LineSegment [constr] StartX=209.942 StartY=39.0944 StartZ=0 EndX=209.942 EndY=7.07331 EndZ=0
  constraints (15):
    c: Coincident(g0,g1)
    c: Coincident(g1,g2)
    c: Coincident(g2,g3)
    c: Coincident(g3,g0)
    c: Horizontal(g0)
    c: Horizontal(g2)
    c: Vertical(g1)
    c: Vertical(g3)
    c: PointOnObject(g4,g-2)
    c: DistanceX(g4,g2) = 10
    c: DistanceY(g0,g1) = 30
    c: Vertical(g5)
    c: DistanceX(g1,g5) = 10
    c: Block(g5)
    c: PointOnObject(g0,g-1)
FEATURE [PartDesign::Pad] Pad033
  Direction = (1,0,0)
  Length = 12
  Length2 = 10
  Midplane = true
  Placement = pos=(0,0,0) rot=(1,1,1;2.0944rad)
  Profile = -> Sketch107
  ReferenceAxis = -> Sketch107 [N_Axis]
  Refine = true
  Suppressed = false
  Type = 0
FEATURE [Sketcher::SketchObject] Sketch108
  ArcFitTolerance = 1e-06
  AttachmentSupport = -> [Pad033]
  ExternalGeometry = -> [Pad033]
  FullyConstrained = false
  MakeInternals = false
  MapMode = 5
  Placement = pos=(2.2e-15,10,0) rot=(0.57735,0.57735,-0.57735;2.0944rad)
  sketch-geometry (9):
    g0: LineSegment [constr] StartX=-40.2302 StartY=4 StartZ=0 EndX=11.0556 EndY=4 EndZ=0
    g1: LineSegment StartX=-40.2302 StartY=4 StartZ=0 EndX=-40.2302 EndY=-9.83045 EndZ=0
    g2: LineSegment StartX=-40.2302 StartY=-9.83045 StartZ=0 EndX=-24 EndY=-9.83045 EndZ=0
    g3: LineSegment StartX=-24 StartY=-9.83045 StartZ=0 EndX=-24 EndY=4 EndZ=0
    g4: LineSegment StartX=-24 StartY=4 StartZ=0 EndX=-40.2302 EndY=4 EndZ=0
    g5: LineSegment StartX=11.0556 StartY=4 StartZ=0 EndX=-6 EndY=4 EndZ=0
    g6: LineSegment StartX=-6 StartY=4 StartZ=0 EndX=-6 EndY=-7.94705 EndZ=0
    g7: LineSegment StartX=-6 StartY=-7.94705 StartZ=0 EndX=11.0556 EndY=-7.94705 EndZ=0
    g8: LineSegment StartX=11.0556 StartY=-7.94705 StartZ=0 EndX=11.0556 EndY=4 EndZ=0
  constraints (22):
    c: Horizontal(g0)
    c: DistanceY(g0,g-4) = 2
    c: Coincident(g1,g2)
    c: Coincident(g2,g3)
    c: Coincident(g3,g4)
    c: Coincident(g4,g1)
    c: Vertical(g1)
    c: Vertical(g3)
    c: Horizontal(g2)
    c: Horizontal(g4)
    c: Coincident(g1,g0)
    c: Coincident(g5,g6)
    c: Coincident(g6,g7)
    c: Coincident(g7,g8)
    c: Coincident(g8,g5)
    c: Horizontal(g5)
    c: Horizontal(g7)
    c: Vertical(g6)
    c: Vertical(g8)
    c: Coincident(g5,g0)
    c: DistanceX(g5,g-1) = 6
    c: DistanceX(g-5,g3) = 6
FEATURE [PartDesign::Pocket] Pocket061
  BaseFeature = -> Pad033
  Direction = (0,1,0)
  Length = 5
  Length2 = 5
  Placement = pos=(0,0,0) rot=(1,1,1;2.0944rad)
  Profile = -> Sketch108
  ReferenceAxis = -> Sketch108 [N_Axis]
  Refine = true
  Suppressed = false
  Type = 1
FEATURE [Sketcher::SketchObject] Sketch109
  ArcFitTolerance = 1e-06
  AttachmentSupport = -> [Pocket061]
  ExternalGeometry = -> [Pocket061]
  FullyConstrained = false
  MakeInternals = false
  MapMode = 5
  Placement = pos=(0,5.3e-15,24) rot=(0,0,-1;1.5708rad)
  sketch-geometry (17):
    g0: LineSegment [constr] StartX=-60 StartY=0.8 StartZ=0 EndX=-60 EndY=10.563 EndZ=0
    g1: LineSegment [constr] StartX=-160 StartY=0.8 StartZ=0 EndX=-160 EndY=11.6219 EndZ=0
    g2: Circle CenterX=-160 CenterY=0.8 CenterZ=0 NormalX=0 NormalY=0 NormalZ=1 AngleXU=0 Radius=1.8
    g3: Circle CenterX=-60 CenterY=0.8 CenterZ=0 NormalX=0 NormalY=0 NormalZ=1 AngleXU=0 Radius=1.8
    g4: LineSegment StartX=-5.7972 StartY=0 StartZ=0 EndX=-55.3173 EndY=-4e-16 EndZ=0
    g5: LineSegment StartX=-155.481 StartY=0 StartZ=0 EndX=-64.3371 EndY=-4e-16 EndZ=0
    g6: LineSegment StartX=-163.912 StartY=0 StartZ=0 EndX=-224.776 EndY=0 EndZ=0
    g7: GeomPoint X=0 Y=14.3735 Z=0
    g8: LineSegment StartX=-224.776 StartY=0 StartZ=0 EndX=-146.784 EndY=-56.3724 EndZ=0
    g9: LineSegment StartX=-146.784 StartY=-56.3724 StartZ=0 EndX=-2.14325 EndY=-56.3724 EndZ=0
    g10: LineSegment StartX=-2.14325 StartY=-56.3724 StartZ=0 EndX=-5.7972 EndY=0 EndZ=0
    g11: LineSegment StartX=-64.3371 StartY=-4e-16 StartZ=0 EndX=-62.0154 EndY=-3.89222 EndZ=0
    g12: LineSegment StartX=-62.0154 StartY=-3.89222 StartZ=0 EndX=-57.8077 EndY=-3.89222 EndZ=0
    g13: LineSegment StartX=-57.8077 StartY=-3.89222 StartZ=0 EndX=-55.3173 EndY=-4e-16 EndZ=0
    g14: LineSegment StartX=-163.912 StartY=0 StartZ=0 EndX=-161.803 EndY=-3.87702 EndZ=0
    g15: LineSegment StartX=-161.803 StartY=-3.87702 StartZ=0 EndX=-157.913 EndY=-3.87702 EndZ=0
    g16: LineSegment StartX=-157.913 StartY=-3.87702 StartZ=0 EndX=-155.481 EndY=0 EndZ=0
  constraints (30):
    c: Vertical(g1)
    c: Vertical(g0)
    c: Coincident(g2,g1)
    c: Coincident(g3,g0)
    c: Diameter(g3) = 3.6
    c: PointOnObject(g7,g-2)
    c: DistanceX(g1,g7) = 160
    c: Coincident(g8,g6)
    c: Coincident(g9,g8)
    c: Horizontal(g9)
    c: Coincident(g10,g9)
    c: Coincident(g10,g4)
    c: DistanceX(g0,g7) = 60
    c: Horizontal(g6)
    c: Coincident(g5,g11)
    c: Coincident(g11,g12)
    c: Coincident(g12,g13)
    c: Coincident(g13,g4)
    c: Coincident(g6,g14)
    c: Coincident(g14,g15)
    c: Coincident(g15,g16)
    c: Coincident(g16,g5)
    c: Horizontal(g6,g5)
    c: Horizontal(g5,g4)
    c: PointOnObject(g6,g-1)
    c: DistanceY(g-1,g-3) = 4
    c: PointOnObject(g4,g-1)
    c: DistanceY(g0,g-5) = 3.2
    c: Horizontal(g1,g0)
    c: PointOnObject(g4,g-1)
FEATURE [PartDesign::Pocket] Pocket062
  BaseFeature = -> Pocket061
  Direction = (0,0,-1)
  Length = 5
  Length2 = 5
  Placement = pos=(0,0,0) rot=(1,1,1;2.0944rad)
  Profile = -> Sketch109
  ReferenceAxis = -> Sketch109 [N_Axis]
  Refine = true
  Suppressed = false
  Type = 1
FEATURE [PartDesign::ShapeBinder] CopyChamfer024
  Placement = pos=(0,0,0) rot=(0.57735,0.57735,0.57735;2.0944rad)
  TraceSupport = false
FEATURE [Sketcher::SketchObject] Sketch111
  ArcFitTolerance = 1e-06
  AttachmentSupport = -> [CopyChamfer024]
  FullyConstrained = true
  MakeInternals = false
  MapMode = 5
  Placement = pos=(2.52936,0.115897,6e-16) rot=(0.559728,0.585963,-0.585963;4.16216rad)
FEATURE [PartDesign::Body] Body027  label="Arm_shoulder_Plate_Top"
  AllowCompound = false
  Group = -> [Sketch094,Pad031,Sketch095,Pocket052,Mirrored003,Sketch096,Pocket053,Chamfer020,Chamfer021,Sketch097,Pocket054,Sketch098,Pocket055,Sketch099,DatumPlane,Sketch100,Pocket056,Sketch101,DatumPlane001,Sketch102,Pocket057,CopyChamfer024,Sketch111]
  Origin = -> Origin036
  Placement = pos=(62,0,-21.5) rot=(0,0,1;0rad)
  Tip = -> Pocket057
FEATURE [Sketcher::SketchObject] Sketch112
  ArcFitTolerance = 1e-06
  AttachmentOffset = pos=(0,0,-5) rot=(0,0,1;0rad)
  FullyConstrained = false
  MakeInternals = false
  MapMode = 5
  Placement = pos=(0,1.3e-15,11) rot=(0.707107,0.707107,0;3.14159rad)
  sketch-geometry (1):
    g0: Circle CenterX=48.2921 CenterY=-4.61711 CenterZ=0 NormalX=0 NormalY=0 NormalZ=1 AngleXU=0 Radius=7.79184
FEATURE [PartDesign::Pocket] Pocket064
  BaseFeature = -> Pocket059
  Direction = (0,0,1)
  Length = 21
  Length2 = 5
  Placement = pos=(0,0,0) rot=(1,1,1;2.0944rad)
  Profile = -> Sketch112
  ReferenceAxis = -> Sketch112 [N_Axis]
  Refine = true
  Suppressed = false
  Type = 0
FEATURE [Sketcher::SketchObject] Sketch117
  ArcFitTolerance = 1e-06
  AttachmentSupport = -> [XY_Plane039]
  FullyConstrained = false
  MakeInternals = false
  MapMode = 5
  sketch-geometry (25):
    g0: LineSegment [constr] StartX=-23 StartY=-5 StartZ=0 EndX=-21 EndY=217 EndZ=0
    g1: LineSegment [constr] StartX=23 StartY=-5 StartZ=0 EndX=21 EndY=217 EndZ=0
    g2: Circle [constr] CenterX=-6.8e-15 CenterY=210 CenterZ=0 NormalX=0 NormalY=0 NormalZ=1 AngleXU=0 Radius=8.1
    g3: LineSegment [constr] StartX=-7 StartY=231 StartZ=0 EndX=7 EndY=231 EndZ=0
    g4: ArcOfCircle [constr] CenterX=-6.8e-15 CenterY=210 CenterZ=0 NormalX=0 NormalY=0 NormalZ=1 AngleXU=0 Radius=22.1359 StartAngle=1.89255 EndAngle=2.81984
    g5: ArcOfCircle [constr] CenterX=-6.8e-15 CenterY=210 CenterZ=0 NormalX=0 NormalY=0 NormalZ=1 AngleXU=0 Radius=22.1359 StartAngle=0.321751 EndAngle=1.24905
    g6: LineSegment [constr] StartX=-10.6301 StartY=-21 StartZ=0 EndX=10.6301 EndY=-21 EndZ=0
    g7: ArcOfCircle [constr] CenterX=0 CenterY=0 CenterZ=0 NormalX=0 NormalY=0 NormalZ=1 AngleXU=0 Radius=23.5372 StartAngle=3.35565 EndAngle=4.2438
    g8: ArcOfCircle [constr] CenterX=0 CenterY=0 CenterZ=0 NormalX=0 NormalY=0 NormalZ=1 AngleXU=0 Radius=23.5372 StartAngle=5.18098 EndAngle=6.06912
    g9: GeomPoint [constr] X=32.4275 Y=0 Z=0
    g10: LineSegment [constr] StartX=-26.3649 StartY=10 StartZ=0 EndX=51.8651 EndY=10 EndZ=0
    g11: ArcOfCircle CenterX=0 CenterY=0 CenterZ=0 NormalX=0 NormalY=0 NormalZ=1 AngleXU=0 Radius=27.126 StartAngle=3.35565 EndAngle=4.26874
    g12: ArcOfCircle CenterX=0 CenterY=0 CenterZ=0 NormalX=0 NormalY=0 NormalZ=1 AngleXU=0 Radius=23.5372 StartAngle=3.35565 EndAngle=4.2438
    g13: ArcOfCircle CenterX=0 CenterY=0 CenterZ=0 NormalX=0 NormalY=0 NormalZ=1 AngleXU=0 Radius=23.5372 StartAngle=5.18098 EndAngle=6.06912
    g14: ArcOfCircle CenterX=0 CenterY=0 CenterZ=0 NormalX=0 NormalY=0 NormalZ=1 AngleXU=0 Radius=27.126 StartAngle=5.15603 EndAngle=6.06912
    g15: LineSegment StartX=-26.3649 StartY=10 StartZ=0 EndX=-26.5069 EndY=-5.76236 EndZ=0
    g16: LineSegment StartX=26.3649 StartY=10 StartZ=0 EndX=26.5069 EndY=-5.76236 EndZ=0
    g17: LineSegment StartX=-23 StartY=-5 StartZ=0 EndX=-22.8649 EndY=10 EndZ=0
    g18: LineSegment StartX=23 StartY=-5 StartZ=0 EndX=22.8649 EndY=10 EndZ=0
    g19: LineSegment StartX=-26.3649 StartY=10 StartZ=0 EndX=-22.8649 EndY=10 EndZ=0
    g20: LineSegment StartX=22.8649 StartY=10 StartZ=0 EndX=26.3649 EndY=10 EndZ=0
    g21: LineSegment StartX=-10.6301 StartY=-21 StartZ=0 EndX=10.6301 EndY=-21 EndZ=0
    g22: LineSegment StartX=-11.6434 StartY=-24.5 StartZ=0 EndX=11.6434 EndY=-24.5 EndZ=0
    g23: GeomPoint X=0 Y=11.7588 Z=0
    g24: LineSegment [constr] StartX=0 StartY=0 StartZ=0 EndX=-35.3086 EndY=-7.67578 EndZ=0
  constraints (64):
    c: Symmetric(g3,g3,g-2)
    c: DistanceY(g2,g3) = 21
    c: Coincident(g4,g2)
    c: Coincident(g4,g3)
    c: Coincident(g4,g0)
    c: Coincident(g5,g2)
    c: Coincident(g5,g3)
    c: Coincident(g5,g1)
    c: Symmetric(g6,g6,g-2)
    c: Coincident(g7,g0)
    c: Coincident(g7,g6)
    c: Coincident(g8,g1)
    c: Coincident(g8,g6)
    c: PointOnObject(g9,g-1)
    c: DistanceY(g9,g2) = 210
    c: Diameter(g2) = 16.2
    c: Horizontal(g0,g1)
    c: DistanceX(g0,g1) = 46
    c: Symmetric(g0,g1,g-2)
    c: DistanceX(g0,g1) = 42
    c: DistanceY(g2,g1) = 7
    c: Coincident(g7,g8)
    c: Coincident(g7,g-1)
    c: DistanceY(g0,g7) = 5
    c: DistanceY(g6,g7) = 21
    c: Horizontal(g10)
    c: DistanceY(g7,g10) = 10
    c: Coincident(g11,g7)
    c: Coincident(g12,g7)
    c: Coincident(g13,g7)
    c: Coincident(g14,g7)
    c: Equal(g12,g13)
    c: Coincident(g15,g10)
    c: Parallel(g15,g0)
    c: PointOnObject(g16,g10)
    c: Parallel(g1,g16)
    c: Coincident(g17,g12)
    c: PointOnObject(g17,g10)
    c: Coincident(g18,g13)
    c: Coincident(g19,g10)
    c: Coincident(g19,g17)
    c: Coincident(g20,g18)
    c: Coincident(g20,g16)
    c: Parallel(g1,g18)
    c: Parallel(g17,g0)
    c: Coincident(g11,g15)
    c: Coincident(g14,g16)
    c: Coincident(g21,g12)
    c: Coincident(g21,g13)
    c: Horizontal(g21)
    c: Coincident(g22,g11)
    c: Coincident(g22,g14)
    c: Horizontal(g22)
    c: PointOnObject(g23,g-2)
    c: Symmetric(g17,g18,g-2)
    c: Coincident(g13,g6)
    c: DistanceX(g18,g16) = 3.5
    c: Equal(g20,g19)
    c: DistanceY(g14,g6) = 3.5
    c: Equal(g11,g14)
    c: PointOnObject(g17,g0)
    c: Coincident(g24,g7)
    c: PointOnObject(g0,g24)
    c: PointOnObject(g11,g24)
FEATURE [PartDesign::Pad] Pad034
  Direction = (0,0,1)
  Length = 30
  Length2 = 10
  Profile = -> Sketch117
  ReferenceAxis = -> Sketch117 [N_Axis]
  Refine = true
  Reversed = true
  Suppressed = false
  Type = 0
FEATURE [Sketcher::SketchObject] Sketch120
  ArcFitTolerance = 1e-06
  FullyConstrained = true
  MakeInternals = false
  MapMode = 5
  Placement = pos=(0,-24.5,0) rot=(1,0,0;1.5708rad)
  sketch-geometry (2):
    g0: Circle CenterX=0 CenterY=-3 CenterZ=0 NormalX=0 NormalY=0 NormalZ=1 AngleXU=0 Radius=1
    g1: Circle CenterX=0 CenterY=-27 CenterZ=0 NormalX=0 NormalY=0 NormalZ=1 AngleXU=0 Radius=1
  constraints (6):
    c: PointOnObject(g0,g-2)
    c: PointOnObject(g1,g-2)
    c: DistanceY(g0,g-1) = 3
    c: DistanceY(g-3,g1) = 3
    c: Equal(g1,g0)
    c: Diameter(g1) = 2
FEATURE [PartDesign::Pocket] Pocket069
  BaseFeature = -> Pad034
  Direction = (0,1,-2e-16)
  Length = 5
  Length2 = 5
  Profile = -> Sketch120
  ReferenceAxis = -> Sketch120 [N_Axis]
  Refine = true
  Suppressed = false
  Type = 1
FEATURE [Sketcher::SketchObject] Sketch121
  ArcFitTolerance = 1e-06
  AttachmentSupport = -> [Pocket069]
  ExternalGeometry = -> [Pocket069]
  FullyConstrained = true
  MakeInternals = false
  MapMode = 5
  Placement = pos=(0,-24.5,0) rot=(1,0,0;1.5708rad)
  sketch-geometry (2):
    g0: Circle CenterX=0 CenterY=-3 CenterZ=0 NormalX=0 NormalY=0 NormalZ=1 AngleXU=0 Radius=2.5
    g1: Circle CenterX=0 CenterY=-27 CenterZ=0 NormalX=0 NormalY=0 NormalZ=1 AngleXU=0 Radius=2.5
  constraints (6):
    c: PointOnObject(g0,g-2)
    c: PointOnObject(g1,g-2)
    c: DistanceY(g-3,g1) = 3
    c: DistanceY(g0,g-1) = 3
    c: Equal(g0,g1)
    c: Diameter(g0) = 5
FEATURE [PartDesign::Pocket] Pocket070
  BaseFeature = -> Pocket069
  Direction = (0,1,-2e-16)
  Length = 2
  Length2 = 5
  Profile = -> Sketch121
  ReferenceAxis = -> Sketch121 [N_Axis]
  Refine = true
  Suppressed = false
  Type = 0
FEATURE [Sketcher::SketchObject] Sketch122
  ArcFitTolerance = 1e-06
  AttachmentOffset = pos=(0,0,-6) rot=(0,0,1;0rad)
  FullyConstrained = false
  MakeInternals = false
  MapMode = 5
  Placement = pos=(0,0,-6) rot=(0,0,1;0rad)
  sketch-geometry (6):
    g0: ArcOfCircle CenterX=0 CenterY=0 CenterZ=0 NormalX=0 NormalY=0 NormalZ=1 AngleXU=0 Radius=18 StartAngle=3.52649 EndAngle=5.89829
    g1: ArcOfCircle CenterX=0 CenterY=0 CenterZ=0 NormalX=0 NormalY=0 NormalZ=1 AngleXU=0 Radius=24.8786 StartAngle=3.4167 EndAngle=4.16246
    g2: ArcOfCircle CenterX=0 CenterY=0 CenterZ=0 NormalX=0 NormalY=0 NormalZ=1 AngleXU=0 Radius=25.2739 StartAngle=5.28732 EndAngle=6.01249
    g3: LineSegment StartX=24.3536 StartY=-6.75837 StartZ=0 EndX=16.6831 EndY=-6.75837 EndZ=0
    g4: LineSegment StartX=-23.9431 StartY=-6.75837 StartZ=0 EndX=-16.6831 EndY=-6.75837 EndZ=0
    g5: LineSegment StartX=-13.0022 StartY=-21.2106 StartZ=0 EndX=13.7435 EndY=-21.2106 EndZ=0
  constraints (14):
    c: Coincident(g0,g-1)
    c: Coincident(g1,g0)
    c: Coincident(g2,g0)
    c: Coincident(g3,g2)
    c: Coincident(g3,g0)
    c: Coincident(g4,g1)
    c: Coincident(g4,g0)
    c: Horizontal(g4)
    c: Coincident(g5,g1)
    c: Coincident(g5,g2)
    c: Horizontal(g5)
    c: Horizontal(g3)
    c: Horizontal(g0,g0)
    c: Radius(g0) = 18
FEATURE [PartDesign::Pad] Pad037
  BaseFeature = -> Pocket070
  Direction = (0,0,1)
  Length = 18
  Length2 = 10
  Profile = -> Sketch122
  ReferenceAxis = -> Sketch122 [N_Axis]
  Refine = true
  Reversed = true
  Suppressed = false
  Type = 0
FEATURE [Sketcher::SketchObject] Sketch123
  ArcFitTolerance = 1e-06
  AttachmentOffset = pos=(0,0,-9) rot=(0,0,1;0rad)
  AttachmentSupport = -> [Pad037]
  ExternalGeometry = -> [Pad037]
  FullyConstrained = false
  MakeInternals = false
  MapMode = 5
  Placement = pos=(0,0,-9) rot=(0,0,1;0rad)
  sketch-geometry (8):
    g0: LineSegment StartX=22.8649 StartY=-9.78793 StartZ=0 EndX=22.8649 EndY=14.8 EndZ=0
    g1: LineSegment StartX=22.8649 StartY=14.8 StartZ=0 EndX=18.8649 EndY=14.8 EndZ=0
    g2: LineSegment StartX=18.8649 StartY=14.8 StartZ=0 EndX=18.8649 EndY=-9.78793 EndZ=0
    g3: LineSegment StartX=18.8649 StartY=-9.78793 StartZ=0 EndX=22.8649 EndY=-9.78793 EndZ=0
    g4: LineSegment StartX=-22.8649 StartY=-9.03146 StartZ=0 EndX=-18.8649 EndY=-9.03146 EndZ=0
    g5: LineSegment StartX=-18.8649 StartY=-9.03146 StartZ=0 EndX=-18.8649 EndY=14.8 EndZ=0
    g6: LineSegment StartX=-18.8649 StartY=14.8 StartZ=0 EndX=-22.8649 EndY=14.8 EndZ=0
    g7: LineSegment StartX=-22.8649 StartY=14.8 StartZ=0 EndX=-22.8649 EndY=-9.03146 EndZ=0
  constraints (22):
    c: Coincident(g0,g1)
    c: Coincident(g1,g2)
    c: Coincident(g2,g3)
    c: Coincident(g3,g0)
    c: Vertical(g0)
    c: Vertical(g2)
    c: Horizontal(g1)
    c: Horizontal(g3)
    c: PointOnObject(g-3,g0)
    c: DistanceY(g-3,g0) = 4.8
    c: Coincident(g4,g5)
    c: Coincident(g5,g6)
    c: Coincident(g6,g7)
    c: Coincident(g7,g4)
    c: Horizontal(g4)
    c: Horizontal(g6)
    c: Vertical(g5)
    c: Vertical(g7)
    c: PointOnObject(g-4,g7)
    c: DistanceY(g-4,g6) = 4.8
    c: DistanceX(g6,g5) = 4
    c: DistanceX(g1,g0) = 4
FEATURE [PartDesign::Pad] Pad038
  BaseFeature = -> Pad037
  Direction = (0,0,1)
  Length = 12
  Length2 = 10
  Profile = -> Sketch123
  ReferenceAxis = -> Sketch123 [N_Axis]
  Refine = true
  Reversed = true
  Suppressed = false
  Type = 0
FEATURE [Sketcher::SketchObject] Sketch124
  ArcFitTolerance = 1e-06
  AttachmentSupport = -> [Pocket062]
  FullyConstrained = false
  MakeInternals = false
  MapMode = 5
  Placement = pos=(0,0,0) rot=(0.57735,0.57735,-0.57735;4.18879rad)
  sketch-geometry (8):
    g0: LineSegment StartX=-30.3538 StartY=-8.82921 StartZ=0 EndX=-30.3538 EndY=-21.1002 EndZ=0
    g1: LineSegment StartX=-30.3538 StartY=-21.1002 StartZ=0 EndX=15.1543 EndY=-21.1002 EndZ=0
    g2: LineSegment StartX=15.1543 StartY=-21.1002 StartZ=0 EndX=15.1543 EndY=-8.82921 EndZ=0
    g3: LineSegment StartX=15.1543 StartY=-8.82921 StartZ=0 EndX=-30.3538 EndY=-8.82921 EndZ=0
    g4: LineSegment StartX=194.555 StartY=-8.82921 StartZ=0 EndX=194.555 EndY=-21.1002 EndZ=0
    g5: LineSegment StartX=194.555 StartY=-21.1002 StartZ=0 EndX=214.341 EndY=-21.1002 EndZ=0
    g6: LineSegment StartX=214.341 StartY=-21.1002 StartZ=0 EndX=214.341 EndY=-8.82921 EndZ=0
    g7: LineSegment StartX=214.341 StartY=-8.82921 StartZ=0 EndX=194.555 EndY=-8.82921 EndZ=0
  constraints (19):
    c: Coincident(g0,g1)
    c: Coincident(g1,g2)
    c: Coincident(g2,g3)
    c: Coincident(g3,g0)
    c: Vertical(g0)
    c: Vertical(g2)
    c: Horizontal(g1)
    c: Horizontal(g3)
    c: Block(g2)
    c: Coincident(g4,g5)
    c: Coincident(g5,g6)
    c: Coincident(g6,g7)
    c: Coincident(g7,g4)
    c: Vertical(g4)
    c: Vertical(g6)
    c: Horizontal(g5)
    c: Horizontal(g7)
    c: Horizontal(g1,g4)
    c: Horizontal(g2,g4)
FEATURE [PartDesign::Pocket] Pocket071
  BaseFeature = -> Pocket062
  Direction = (1,0,0)
  Length = 4
  Length2 = 5
  Placement = pos=(0,0,0) rot=(1,1,1;2.0944rad)
  Profile = -> Sketch124
  ReferenceAxis = -> Sketch124 [N_Axis]
  Refine = true
  Suppressed = false
  Type = 0
FEATURE [PartDesign::Fillet] Fillet022
  Base = -> Pocket071 [Edge18,Edge3]
  BaseFeature = -> Pocket071
  Placement = pos=(0,0,0) rot=(1,1,1;2.0944rad)
  Radius = 1.5
  Refine = true
  SupportTransform = false
  Suppressed = false
  UseAllEdges = false
FEATURE [PartDesign::Body] Body029  label="SHOULDER RIGHT SIDE"
  AllowCompound = false
  Group = -> [Sketch107,Pad033,Sketch108,Pocket061,Sketch109,Pocket062,Sketch124,Pocket071,Fillet022]
  Origin = -> Origin038
  Placement = pos=(-19,-8e-16,8.5) rot=(0,-1,0;3.14159rad)
  Tip = -> Fillet022
FEATURE [Sketcher::SketchObject] Sketch127
  ArcFitTolerance = 1e-06
  AttachmentSupport = -> [Pocket064]
  ExternalGeometry = -> [Pocket064]
  FullyConstrained = false
  MakeInternals = false
  MapMode = 5
  Placement = pos=(2.2e-15,10,0) rot=(0.57735,0.57735,-0.57735;2.0944rad)
  sketch-geometry (4):
    g0: LineSegment StartX=-21 StartY=4 StartZ=0 EndX=-21 EndY=-7.99774 EndZ=0
    g1: LineSegment StartX=-21 StartY=-7.99774 StartZ=0 EndX=-9 EndY=-7.99774 EndZ=0
    g2: LineSegment StartX=-9 StartY=-7.99774 StartZ=0 EndX=-9 EndY=4 EndZ=0
    g3: LineSegment StartX=-9 StartY=4 StartZ=0 EndX=-21 EndY=4 EndZ=0
  constraints (11):
    c: Coincident(g0,g1)
    c: Coincident(g1,g2)
    c: Coincident(g2,g3)
    c: Coincident(g3,g0)
    c: Vertical(g0)
    c: Vertical(g2)
    c: Horizontal(g1)
    c: Horizontal(g3)
    c: Horizontal(g-4,g0)
    c: DistanceX(g-4,g0) = 3
    c: DistanceX(g2,g-3) = 3
FEATURE [PartDesign::Pocket] Pocket074
  BaseFeature = -> Pocket064
  Direction = (0,1,0)
  Length = 5
  Length2 = 5
  Placement = pos=(0,0,0) rot=(1,1,1;2.0944rad)
  Profile = -> Sketch127
  ReferenceAxis = -> Sketch127 [N_Axis]
  Refine = true
  Suppressed = false
  Type = 0
FEATURE [Sketcher::SketchObject] Sketch128
  ArcFitTolerance = 1e-06
  AttachmentSupport = -> [Pocket074]
  ExternalGeometry = -> [Pocket074]
  FullyConstrained = false
  MakeInternals = false
  MapMode = 5
  Placement = pos=(4.4e-14,199.942,0) rot=(0.57735,0.57735,0.57735;4.18879rad)
  sketch-geometry (4):
    g0: LineSegment StartX=9 StartY=4 StartZ=0 EndX=9 EndY=-7.88026 EndZ=0
    g1: LineSegment StartX=9 StartY=-7.88026 StartZ=0 EndX=21 EndY=-7.88026 EndZ=0
    g2: LineSegment StartX=21 StartY=-7.88026 StartZ=0 EndX=21 EndY=4 EndZ=0
    g3: LineSegment StartX=21 StartY=4 StartZ=0 EndX=9 EndY=4 EndZ=0
  constraints (11):
    c: Coincident(g0,g1)
    c: Coincident(g1,g2)
    c: Coincident(g2,g3)
    c: Coincident(g3,g0)
    c: Vertical(g0)
    c: Vertical(g2)
    c: Horizontal(g1)
    c: Horizontal(g3)
    c: Horizontal(g-3,g0)
    c: DistanceX(g-3,g0) = 3
    c: DistanceX(g2,g-4) = 3
FEATURE [PartDesign::Pocket] Pocket075
  BaseFeature = -> Pocket074
  Direction = (0,-1,0)
  Length = 5
  Length2 = 5
  Placement = pos=(0,0,0) rot=(1,1,1;2.0944rad)
  Profile = -> Sketch128
  ReferenceAxis = -> Sketch128 [N_Axis]
  Refine = true
  Suppressed = false
  Type = 0
FEATURE [PartDesign::Body] Body028  label="SHOULDER LEFT SIDE"
  AllowCompound = false
  Group = -> [Sketch103,Pad032,Sketch104,Pocket058,Sketch105,Pocket059,Sketch112,Pocket064,Sketch127,Pocket074,Sketch128,Pocket075]
  Origin = -> Origin037
  Placement = pos=(19,0,-21.5) rot=(0,0,1;0rad)
  Tip = -> Pocket075
FEATURE [Sketcher::SketchObject] Sketch129
  ArcFitTolerance = 1e-06
  AttachmentSupport = -> [XY_Plane040]
  FullyConstrained = false
  MakeInternals = false
  MapMode = 5
  sketch-geometry (27):
    g0: LineSegment [constr] StartX=-23 StartY=-5 StartZ=0 EndX=-21 EndY=217 EndZ=0
    g1: LineSegment [constr] StartX=23 StartY=-5 StartZ=0 EndX=21 EndY=217 EndZ=0
    g2: Circle [constr] CenterX=1.43e-14 CenterY=210 CenterZ=0 NormalX=0 NormalY=0 NormalZ=1 AngleXU=0 Radius=8.1
    g3: LineSegment [constr] StartX=-7 StartY=231 StartZ=0 EndX=7 EndY=231 EndZ=0
    g4: ArcOfCircle [constr] CenterX=1.43e-14 CenterY=210 CenterZ=0 NormalX=0 NormalY=0 NormalZ=1 AngleXU=0 Radius=22.1359 StartAngle=1.89255 EndAngle=2.81984
    g5: ArcOfCircle [constr] CenterX=1.43e-14 CenterY=210 CenterZ=0 NormalX=0 NormalY=0 NormalZ=1 AngleXU=0 Radius=22.1359 StartAngle=0.321751 EndAngle=1.24905
    g6: LineSegment [constr] StartX=-10.6301 StartY=-21 StartZ=0 EndX=10.6301 EndY=-21 EndZ=0
    g7: ArcOfCircle [constr] CenterX=0 CenterY=0 CenterZ=0 NormalX=0 NormalY=0 NormalZ=1 AngleXU=0 Radius=23.5372 StartAngle=3.35565 EndAngle=4.2438
    g8: ArcOfCircle [constr] CenterX=0 CenterY=0 CenterZ=0 NormalX=0 NormalY=0 NormalZ=1 AngleXU=0 Radius=23.5372 StartAngle=5.18098 EndAngle=6.06912
    g9: GeomPoint [constr] X=32.4275 Y=0 Z=0
    g10: LineSegment [constr] StartX=-26.3649 StartY=10 StartZ=0 EndX=51.8651 EndY=10 EndZ=0
    g11: LineSegment [constr] StartX=0 StartY=0 StartZ=0 EndX=-35.3086 EndY=-7.67578 EndZ=0
    g12: LineSegment [constr] StartX=-40.8172 StartY=200 StartZ=0 EndX=71.5323 EndY=200 EndZ=0
    g13: LineSegment StartX=-7 StartY=231 StartZ=0 EndX=7 EndY=231 EndZ=0
    g14: LineSegment StartX=-8.13167 StartY=234.5 StartZ=0 EndX=8.201 EndY=234.5 EndZ=0
    g15: ArcOfCircle CenterX=1.43e-14 CenterY=210 CenterZ=0 NormalX=0 NormalY=0 NormalZ=1 AngleXU=0 Radius=22.1359 StartAngle=0.352614 EndAngle=1.24905
    g16: ArcOfCircle CenterX=1.43e-14 CenterY=210 CenterZ=0 NormalX=0 NormalY=0 NormalZ=1 AngleXU=0 Radius=25.8361 StartAngle=0.352614 EndAngle=1.24779
    g17: ArcOfCircle CenterX=1.43e-14 CenterY=210 CenterZ=0 NormalX=0 NormalY=0 NormalZ=1 AngleXU=0 Radius=25.8142 StartAngle=1.89126 EndAngle=2.81984
    g18: ArcOfCircle CenterX=0 CenterY=210 CenterZ=0 NormalX=0 NormalY=0 NormalZ=1 AngleXU=0 Radius=22.1359 StartAngle=1.89255 EndAngle=2.81984
    g19: LineSegment StartX=-24.4895 StartY=218.163 StartZ=0 EndX=-24.6532 EndY=200 EndZ=0
    g20: LineSegment StartX=-24.6532 StartY=200 StartZ=0 EndX=-21.1532 EndY=200 EndZ=0
    g21: LineSegment StartX=-21 StartY=217 StartZ=0 EndX=-21.1532 EndY=200 EndZ=0
    g22: LineSegment StartX=20.774 StartY=217.645 StartZ=0 EndX=21.1532 EndY=200 EndZ=0
    g23: LineSegment StartX=24.2465 StartY=218.923 StartZ=0 EndX=24.6532 EndY=200 EndZ=0
    g24: LineSegment StartX=21.1532 StartY=200 StartZ=0 EndX=24.6532 EndY=200 EndZ=0
    g25: LineSegment [constr] StartX=0 StartY=210 StartZ=0 EndX=-24.4895 EndY=218.163 EndZ=0
    g26: LineSegment [constr] StartX=1.43e-14 StartY=210 StartZ=0 EndX=24.2465 EndY=218.923 EndZ=0
  constraints (68):
    c: Symmetric(g3,g3,g-2)
    c: DistanceY(g2,g3) = 21
    c: Coincident(g4,g2)
    c: Coincident(g4,g3)
    c: Coincident(g4,g0)
    c: Coincident(g5,g2)
    c: Coincident(g5,g3)
    c: Coincident(g5,g1)
    c: Symmetric(g6,g6,g-2)
    c: Coincident(g7,g0)
    c: Coincident(g7,g6)
    c: Coincident(g8,g1)
    c: Coincident(g8,g6)
    c: PointOnObject(g9,g-1)
    c: DistanceY(g9,g2) = 210
    c: Diameter(g2) = 16.2
    c: Horizontal(g0,g1)
    c: DistanceX(g0,g1) = 46
    c: Symmetric(g0,g1,g-2)
    c: DistanceX(g0,g1) = 42
    c: DistanceY(g2,g1) = 7
    c: Coincident(g7,g8)
    c: Coincident(g7,g-1)
    c: DistanceY(g0,g7) = 5
    c: DistanceY(g6,g7) = 21
    c: Horizontal(g10)
    c: DistanceY(g7,g10) = 10
    c: Coincident(g11,g7)
    c: PointOnObject(g0,g11)
    c: Horizontal(g12)
    c: DistanceY(g12,g2) = 10
    c: Coincident(g13,g3)
    c: Coincident(g13,g3)
    c: Horizontal(g14)
    c: DistanceY(g3,g14) = 3.5
    c: Coincident(g15,g2)
    c: Coincident(g15,g3)
    c: Coincident(g17,g16)
    c: Coincident(g17,g14)
    c: Coincident(g19,g17)
    c: PointOnObject(g19,g12)
    c: Coincident(g20,g19)
    c: PointOnObject(g20,g12)
    c: Coincident(g21,g18)
    c: Coincident(g21,g20)
    c: DistanceX(g19,g20) = 3.5
    c: PointOnObject(g20,g0)
    c: Parallel(g19,g21)
    c: Coincident(g18,g0)
    c: Coincident(g22,g15)
    c: PointOnObject(g22,g12)
    c: Coincident(g23,g16)
    c: PointOnObject(g23,g12)
    c: Coincident(g24,g22)
    c: Coincident(g24,g23)
    c: Equal(g20,g24)
    c: PointOnObject(g22,g1)
    c: Coincident(g18,g3)
    c: Coincident(g16,g14)
    c: Parallel(g23,g22)
    c: Coincident(g16,g2)
    c: PointOnObject(g18,g-2)
    c: Coincident(g25,g18)
    c: Coincident(g25,g17)
    c: PointOnObject(g0,g25)
    c: Coincident(g26,g2)
    c: Coincident(g26,g16)
    c: PointOnObject(g15,g26)
FEATURE [PartDesign::Pad] Pad039
  Direction = (0,0,1)
  Length = 30
  Length2 = 10
  Profile = -> Sketch129
  ReferenceAxis = -> Sketch129 [N_Axis]
  Refine = true
  Reversed = true
  Suppressed = false
  Type = 0
FEATURE [Sketcher::SketchObject] Sketch130
  ArcFitTolerance = 1e-06
  AttachmentOffset = pos=(0,0,-6) rot=(0,0,1;0rad)
  AttachmentSupport = -> [Pad039]
  ExternalGeometry = -> [Pad039]
  FullyConstrained = false
  MakeInternals = false
  MapMode = 5
  Placement = pos=(0,0,-6) rot=(0,0,1;0rad)
  sketch-geometry (5):
    g0: LineSegment [constr] StartX=-36.3908 StartY=210 StartZ=0 EndX=46.9754 EndY=210 EndZ=0
    g1: ArcOfCircle CenterX=0 CenterY=210 CenterZ=0 NormalX=0 NormalY=0 NormalZ=1 AngleXU=0 Radius=18.0799 StartAngle=0.436564 EndAngle=2.74403
    g2: ArcOfCircle CenterX=0 CenterY=210 CenterZ=0 NormalX=0 NormalY=0 NormalZ=1 AngleXU=0 Radius=23.6352 StartAngle=0.329369 EndAngle=2.84091
    g3: LineSegment StartX=-16.6698 StartY=217 StartZ=0 EndX=-22.5748 EndY=217 EndZ=0
    g4: LineSegment StartX=22.3647 StartY=217.645 StartZ=0 EndX=16.3842 EndY=217.645 EndZ=0
  constraints (13):
    c: Horizontal(g0)
    c: DistanceY(g-3,g0) = 10
    c: PointOnObject(g1,g0)
    c: Coincident(g2,g1)
    c: Coincident(g3,g1)
    c: Coincident(g4,g2)
    c: Coincident(g4,g1)
    c: Horizontal(g4)
    c: PointOnObject(g-4,g4)
    c: PointOnObject(g-5,g3)
    c: Horizontal(g3)
    c: PointOnObject(g1,g-2)
    c: Coincident(g2,g3)
FEATURE [PartDesign::Pad] Pad040
  BaseFeature = -> Pad039
  Direction = (0,0,1)
  Length = 18
  Length2 = 10
  Profile = -> Sketch130
  ReferenceAxis = -> Sketch130 [N_Axis]
  Refine = true
  Reversed = true
  Suppressed = false
  Type = 0
FEATURE [Sketcher::SketchObject] Sketch131
  ArcFitTolerance = 1e-06
  AttachmentSupport = -> [Pad040]
  ExternalGeometry = -> [Pad040]
  FullyConstrained = true
  MakeInternals = false
  MapMode = 5
  Placement = pos=(-1.624e-12,200,0) rot=(1,0,0;1.5708rad)
  sketch-geometry (8):
    g0: LineSegment StartX=-21.1532 StartY=-9 StartZ=0 EndX=-21.1532 EndY=-21 EndZ=0
    g1: LineSegment StartX=-21.1532 StartY=-21 StartZ=0 EndX=-18.1532 EndY=-21 EndZ=0
    g2: LineSegment StartX=-18.1532 StartY=-21 StartZ=0 EndX=-18.1532 EndY=-9 EndZ=0
    g3: LineSegment StartX=-18.1532 StartY=-9 StartZ=0 EndX=-21.1532 EndY=-9 EndZ=0
    g4: LineSegment StartX=21.1532 StartY=-9 StartZ=0 EndX=18.1532 EndY=-9 EndZ=0
    g5: LineSegment StartX=18.1532 StartY=-9 StartZ=0 EndX=18.1532 EndY=-21 EndZ=0
    g6: LineSegment StartX=18.1532 StartY=-21 StartZ=0 EndX=21.1532 EndY=-21 EndZ=0
    g7: LineSegment StartX=21.1532 StartY=-21 StartZ=0 EndX=21.1532 EndY=-9 EndZ=0
  constraints (24):
    c: Coincident(g0,g1)
    c: Coincident(g1,g2)
    c: Coincident(g2,g3)
    c: Coincident(g3,g0)
    c: Vertical(g0)
    c: Vertical(g2)
    c: Horizontal(g1)
    c: Horizontal(g3)
    c: PointOnObject(g0,g-4)
    c: Coincident(g4,g5)
    c: Coincident(g5,g6)
    c: Coincident(g6,g7)
    c: Coincident(g7,g4)
    c: Horizontal(g4)
    c: Horizontal(g6)
    c: Vertical(g5)
    c: Vertical(g7)
    c: PointOnObject(g4,g-3)
    c: DistanceY(g4,g-3) = 9
    c: DistanceY(g-3,g6) = 9
    c: Horizontal(g4,g2)
    c: Horizontal(g1,g5)
    c: DistanceX(g0,g2) = 3
    c: DistanceX(g4,g4) = 3
FEATURE [PartDesign::Pad] Pad041
  BaseFeature = -> Pad040
  Direction = (8.1e-15,-1,2e-16)
  Length = 5
  Length2 = 23
  Profile = -> Sketch131
  ReferenceAxis = -> Sketch131 [N_Axis]
  Refine = true
  Suppressed = false
  Type = 4
FEATURE [Sketcher::SketchObject] Sketch132
  ArcFitTolerance = 1e-06
  AttachmentSupport = -> [Pad041]
  ExternalGeometry = -> [Pad041]
  FullyConstrained = true
  MakeInternals = false
  MapMode = 5
  Placement = pos=(0,234.5,0) rot=(0,0.707107,0.707107;3.14159rad)
  sketch-geometry (2):
    g0: Circle CenterX=0 CenterY=-27 CenterZ=0 NormalX=0 NormalY=0 NormalZ=1 AngleXU=0 Radius=1
    g1: Circle CenterX=0 CenterY=-3 CenterZ=0 NormalX=0 NormalY=0 NormalZ=1 AngleXU=0 Radius=1
  constraints (6):
    c: PointOnObject(g0,g-2)
    c: PointOnObject(g1,g-2)
    c: Equal(g1,g0)
    c: Diameter(g1) = 2
    c: DistanceY(g1,g-1) = 3
    c: DistanceY(g-3,g0) = 3
FEATURE [PartDesign::Pocket] Pocket076
  BaseFeature = -> Pad041
  Direction = (0,-1,2e-16)
  Length = 5
  Length2 = 5
  Profile = -> Sketch132
  ReferenceAxis = -> Sketch132 [N_Axis]
  Refine = true
  Suppressed = false
  Type = 1
FEATURE [Sketcher::SketchObject] Sketch133
  ArcFitTolerance = 1e-06
  AttachmentSupport = -> [Pocket076]
  ExternalGeometry = -> [Pocket076]
  FullyConstrained = true
  MakeInternals = false
  MapMode = 5
  Placement = pos=(0,234.5,0) rot=(0,0.707107,0.707107;3.14159rad)
  sketch-geometry (2):
    g0: Circle CenterX=0 CenterY=-3 CenterZ=0 NormalX=0 NormalY=0 NormalZ=1 AngleXU=0 Radius=2.25
    g1: Circle CenterX=0 CenterY=-27 CenterZ=0 NormalX=0 NormalY=0 NormalZ=1 AngleXU=0 Radius=2.25
  constraints (6):
    c: PointOnObject(g0,g-2)
    c: PointOnObject(g1,g-2)
    c: DistanceY(g-3,g1) = 3
    c: DistanceY(g0,g-1) = 3
    c: Equal(g0,g1)
    c: Diameter(g0) = 4.5
FEATURE [PartDesign::Pocket] Pocket077
  BaseFeature = -> Pocket076
  Direction = (0,-1,2e-16)
  Length = 1.5
  Length2 = 5
  Profile = -> Sketch133
  ReferenceAxis = -> Sketch133 [N_Axis]
  Refine = true
  Suppressed = false
  Type = 0
FEATURE [PartDesign::Fillet] Fillet028
  Base = -> Pad038 [Edge22,Edge13]
  BaseFeature = -> Pad038
  Radius = 2
  Refine = true
  SupportTransform = false
  Suppressed = false
  UseAllEdges = false
FEATURE [Sketcher::SketchObject] Sketch134
  ArcFitTolerance = 1e-06
  AttachmentSupport = -> [Fillet028]
  ExternalGeometry = -> [Fillet028]
  FullyConstrained = false
  MakeInternals = false
  MapMode = 5
  Placement = pos=(26.4528,0.238314,0) rot=(0.573883,0.579076,0.579076;2.0996rad)
  sketch-geometry (4):
    g0: ArcOfCircle CenterX=9.76208 CenterY=-8.3856 CenterZ=0 NormalX=0 NormalY=0 NormalZ=1 AngleXU=0 Radius=4 StartAngle=2e-16 EndAngle=3.14159
    g1: ArcOfCircle CenterX=9.76208 CenterY=-22 CenterZ=0 NormalX=0 NormalY=0 NormalZ=1 AngleXU=0 Radius=4 StartAngle=3.14159 EndAngle=6.28319
    g2: LineSegment StartX=13.7621 StartY=-8.3856 StartZ=0 EndX=13.7621 EndY=-22 EndZ=0
    g3: LineSegment StartX=5.76208 StartY=-8.3856 StartZ=0 EndX=5.76208 EndY=-22 EndZ=0
  constraints (9):
    c: Tangent(g0,g2) = 1.5708
    c: Tangent(g0,g3) = -1.5708
    c: Tangent(g1,g2) = 1.5708
    c: Tangent(g1,g3) = -1.5708
    c: Equal(g0,g1)
    c: Vertical(g3)
    c: PointOnObject(g0,g-3)
    c: DistanceY(g-3,g1) = 8
    c: Diameter(g0) = 8
FEATURE [PartDesign::Pad] Pad042
  BaseFeature = -> Fillet028
  Direction = (0.999959,0.00900864,1e-16)
  Length = 2.6
  Length2 = 10
  Midplane = true
  Profile = -> Sketch134
  ReferenceAxis = -> Sketch134 [N_Axis]
  Refine = true
  Suppressed = false
  Type = 0
FEATURE [PartDesign::Fillet] Fillet029
  Base = -> Pad042 [Edge27,Edge39]
  BaseFeature = -> Pad042
  Radius = 2
  Refine = true
  SupportTransform = false
  Suppressed = false
  UseAllEdges = false
FEATURE [PartDesign::Fillet] Fillet030
  Base = -> Fillet029 [Face41]
  BaseFeature = -> Fillet029
  Radius = 1
  Refine = true
  SupportTransform = false
  Suppressed = false
  UseAllEdges = false
FEATURE [Sketcher::SketchObject] Sketch135
  ArcFitTolerance = 1e-06
  AttachmentSupport = -> [Fillet030]
  ExternalGeometry = -> [Fillet030]
  FullyConstrained = true
  MakeInternals = false
  MapMode = 5
  Placement = pos=(-26.4528,0.238314,0) rot=(-0.573883,0.579076,0.579076;4.18358rad)
  sketch-geometry (4):
    g0: ArcOfCircle CenterX=-9.76208 CenterY=-8 CenterZ=0 NormalX=0 NormalY=0 NormalZ=1 AngleXU=0 Radius=4 StartAngle=0 EndAngle=3.14159
    g1: ArcOfCircle CenterX=-9.76208 CenterY=-22 CenterZ=0 NormalX=0 NormalY=0 NormalZ=1 AngleXU=0 Radius=4 StartAngle=3.14159 EndAngle=6.28319
    g2: LineSegment StartX=-5.76208 StartY=-8 StartZ=0 EndX=-5.76208 EndY=-22 EndZ=0
    g3: LineSegment StartX=-13.7621 StartY=-8 StartZ=0 EndX=-13.7621 EndY=-22 EndZ=0
  constraints (10):
    c: Tangent(g0,g2) = 1.5708
    c: Tangent(g0,g3) = -1.5708
    c: Tangent(g1,g2) = 1.5708
    c: Tangent(g1,g3) = -1.5708
    c: Equal(g0,g1)
    c: Vertical(g3)
    c: PointOnObject(g0,g-3)
    c: DistanceY(g0,g-3) = 8
    c: DistanceY(g-3,g1) = 8
    c: Diameter(g0) = 8
FEATURE [PartDesign::Pad] Pad043
  BaseFeature = -> Fillet030
  Direction = (-0.999959,0.00900864,2e-16)
  Length = 2.6
  Length2 = 10
  Midplane = true
  Profile = -> Sketch135
  ReferenceAxis = -> Sketch135 [N_Axis]
  Refine = true
  Suppressed = false
  Type = 0
FEATURE [PartDesign::Fillet] Fillet031
  Base = -> Pad043 [Edge54,Edge66]
  BaseFeature = -> Pad043
  Radius = 2
  Refine = true
  SupportTransform = false
  Suppressed = false
  UseAllEdges = false
FEATURE [PartDesign::Fillet] Fillet032
  Base = -> Fillet031 [Face47]
  BaseFeature = -> Fillet031
  Radius = 1
  Refine = true
  SupportTransform = false
  Suppressed = false
  UseAllEdges = false
FEATURE [PartDesign::Body] Body030  label="SHOULDER END Z AXIS"
  AllowCompound = false
  Group = -> [Sketch117,Pad034,Sketch120,Pocket069,Sketch121,Pocket070,Sketch122,Pad037,Sketch123,Pad038,Fillet028,Sketch134,Pad042,Fillet029,Fillet030,Sketch135,Pad043,Fillet031,Fillet032]
  Origin = -> Origin039
  Placement = pos=(0,2.5,7.5) rot=(0,0,1;0rad)
  Tip = -> Fillet032
FEATURE [Sketcher::SketchObject] Sketch136
  ArcFitTolerance = 1e-06
  AttachmentSupport = -> [Pocket077]
  ExternalGeometry = -> [Pocket077]
  FullyConstrained = true
  MakeInternals = false
  MapMode = 5
  Placement = pos=(-26.4528,0.238314,0) rot=(-0.573883,0.579076,0.579076;4.18358rad)
  sketch-geometry (4):
    g0: ArcOfCircle CenterX=-199.77 CenterY=-22 CenterZ=0 NormalX=0 NormalY=0 NormalZ=1 AngleXU=0 Radius=4 StartAngle=3.14159 EndAngle=6.28319
    g1: ArcOfCircle CenterX=-199.77 CenterY=-8 CenterZ=0 NormalX=0 NormalY=0 NormalZ=1 AngleXU=0 Radius=4 StartAngle=1.03e-14 EndAngle=3.14159
    g2: LineSegment StartX=-203.77 StartY=-22 StartZ=0 EndX=-203.77 EndY=-8 EndZ=0
    g3: LineSegment StartX=-195.77 StartY=-22 StartZ=0 EndX=-195.77 EndY=-8 EndZ=0
  constraints (10):
    c: Tangent(g0,g2) = 1.5708
    c: Tangent(g0,g3) = -1.5708
    c: Tangent(g1,g2) = 1.5708
    c: Tangent(g1,g3) = -1.5708
    c: Equal(g0,g1)
    c: Vertical(g3)
    c: PointOnObject(g0,g-3)
    c: DistanceY(g1,g-3) = 8
    c: DistanceY(g-3,g0) = 8
    c: Diameter(g1) = 8
FEATURE [PartDesign::Pad] Pad044
  BaseFeature = -> Pocket077
  Direction = (-0.999959,0.00900864,2e-16)
  Length = 2.6
  Length2 = 10
  Midplane = true
  Profile = -> Sketch136
  ReferenceAxis = -> Sketch136 [N_Axis]
  Refine = true
  Suppressed = false
  Type = 0
FEATURE [Sketcher::SketchObject] Sketch137
  ArcFitTolerance = 1e-06
  AttachmentSupport = -> [Pad044]
  ExternalGeometry = -> [Pad044]
  FullyConstrained = true
  MakeInternals = false
  MapMode = 5
  Placement = pos=(28.9376,0.621837,0) rot=(0.569081,0.581441,0.581441;2.10684rad)
  sketch-geometry (4):
    g0: ArcOfCircle CenterX=199.424 CenterY=-8 CenterZ=0 NormalX=0 NormalY=0 NormalZ=1 AngleXU=0 Radius=4 StartAngle=1e-16 EndAngle=3.14159
    g1: ArcOfCircle CenterX=199.424 CenterY=-22 CenterZ=0 NormalX=0 NormalY=0 NormalZ=1 AngleXU=0 Radius=4 StartAngle=3.14159 EndAngle=6.28319
    g2: LineSegment StartX=203.424 StartY=-8 StartZ=0 EndX=203.424 EndY=-22 EndZ=0
    g3: LineSegment StartX=195.424 StartY=-8 StartZ=0 EndX=195.424 EndY=-22 EndZ=0
  constraints (10):
    c: Tangent(g0,g2) = 1.5708
    c: Tangent(g0,g3) = -1.5708
    c: Tangent(g1,g2) = 1.5708
    c: Tangent(g1,g3) = -1.5708
    c: Equal(g0,g1)
    c: Vertical(g3)
    c: PointOnObject(g0,g-3)
    c: DistanceY(g0,g-3) = 8
    c: DistanceY(g-3,g1) = 8
    c: Diameter(g0) = 8
FEATURE [PartDesign::Pad] Pad045
  BaseFeature = -> Pad044
  Direction = (0.999769,0.021484,1e-16)
  Length = 2.6
  Length2 = 10
  Midplane = true
  Profile = -> Sketch137
  ReferenceAxis = -> Sketch137 [N_Axis]
  Refine = true
  Suppressed = false
  Type = 0
FEATURE [PartDesign::Fillet] Fillet033
  Base = -> Pad045 [Edge11,Edge46]
  BaseFeature = -> Pad045
  Radius = 2
  Refine = true
  SupportTransform = false
  Suppressed = false
  UseAllEdges = false
FEATURE [PartDesign::Fillet] Fillet034
  Base = -> Fillet033 [Edge3,Edge27,Edge10,Edge53]
  BaseFeature = -> Fillet033
  Radius = 2
  Refine = true
  SupportTransform = false
  Suppressed = false
  UseAllEdges = false
FEATURE [PartDesign::Fillet] Fillet035
  Base = -> Fillet034 [Face58]
  BaseFeature = -> Fillet034
  Radius = 1
  Refine = true
  SupportTransform = false
  Suppressed = false
  UseAllEdges = false
FEATURE [PartDesign::Fillet] Fillet036
  Base = -> Fillet035 [Face65]
  BaseFeature = -> Fillet035
  Radius = 1
  Refine = true
  SupportTransform = false
  Suppressed = false
  UseAllEdges = false
FEATURE [PartDesign::Body] Body031  label="SHOULDER END TIP"
  AllowCompound = false
  Group = -> [Sketch129,Pad039,Sketch130,Pad040,Sketch131,Pad041,Sketch132,Pocket076,Sketch133,Pocket077,Sketch136,Pad044,Sketch137,Pad045,Fillet033,Fillet034,Fillet035,Fillet036]
  Origin = -> Origin040
  Placement = pos=(0,0.5,7.5) rot=(0,0,1;0rad)
  Tip = -> Fillet036
FEATURE [Sketcher::SketchObject] Sketch138
  ArcFitTolerance = 1e-06
  AttachmentSupport = -> [XY_Plane041]
  FullyConstrained = false
  MakeInternals = false
  MapMode = 5
  sketch-geometry (6):
    g0: LineSegment StartX=-21 StartY=10 StartZ=0 EndX=-21 EndY=-6.55744 EndZ=0
    g1: LineSegment StartX=21 StartY=10 StartZ=0 EndX=21 EndY=-5.84233 EndZ=0
    g2: LineSegment StartX=-6.55744 StartY=-21 StartZ=0 EndX=5.84233 EndY=-21 EndZ=0
    g3: ArcOfCircle CenterX=0 CenterY=0 CenterZ=0 NormalX=0 NormalY=0 NormalZ=1 AngleXU=0 Radius=22 StartAngle=3.44426 EndAngle=4.40972
    g4: ArcOfCircle CenterX=0 CenterY=0 CenterZ=0 NormalX=0 NormalY=0 NormalZ=1 AngleXU=0 Radius=21.7975 StartAngle=4.98373 EndAngle=6.01184
    g5: GeomPoint X=33.4941 Y=0 Z=0
  constraints (15):
    c: Vertical(g0)
    c: Vertical(g1)
    c: Horizontal(g2)
    c: Coincident(g3,g-1)
    c: Coincident(g3,g0)
    c: Coincident(g3,g2)
    c: Coincident(g4,g3)
    c: Coincident(g4,g2)
    c: Coincident(g4,g1)
    c: DistanceX(g0,g1) = 42
    c: Symmetric(g0,g1,g-2)
    c: PointOnObject(g5,g-1)
    c: DistanceY(g2,g5) = 21
    c: Radius(g3) = 22
    c: DistanceY(g5,g1) = 10
FEATURE [PartDesign::Body] Body032
  AllowCompound = false
  Group = -> [Sketch138]
  Origin = -> Origin041
FEATURE [Sketcher::SketchObject] Sketch139
  ArcFitTolerance = 1e-06
  AttachmentSupport = -> [XY_Plane043]
  FullyConstrained = true
  MakeInternals = false
  MapMode = 5
  sketch-geometry (2):
    g0: Circle CenterX=0 CenterY=0 CenterZ=0 NormalX=0 NormalY=0 NormalZ=1 AngleXU=0 Radius=1.8
    g1: Circle CenterX=0 CenterY=0 CenterZ=0 NormalX=0 NormalY=0 NormalZ=1 AngleXU=0 Radius=1.5
  constraints (4):
    c: Coincident(g0,g-1)
    c: Coincident(g1,g0)
    c: Diameter(g1) = 3
    c: Diameter(g0) = 3.6
FEATURE [PartDesign::Pad] Pad046
  Direction = (0,0,1)
  Length = 2
  Length2 = 10
  Profile = -> Sketch139
  ReferenceAxis = -> Sketch139 [N_Axis]
  Refine = true
  Suppressed = false
  Type = 0
FEATURE [Sketcher::SketchObject] Sketch141
  ArcFitTolerance = 1e-06
  AttachmentSupport = -> [XY_Plane044]
  FullyConstrained = true
  MakeInternals = false
  MapMode = 5
  sketch-geometry (2):
    g0: Circle CenterX=0 CenterY=0 CenterZ=0 NormalX=0 NormalY=0 NormalZ=1 AngleXU=0 Radius=3.1
    g1: Circle CenterX=0 CenterY=0 CenterZ=0 NormalX=0 NormalY=0 NormalZ=1 AngleXU=0 Radius=2.25
  constraints (4):
    c: Coincident(g0,g-1)
    c: Coincident(g1,g0)
    c: Radius(g0) = 3.1
    c: Diameter(g1) = 4.5
FEATURE [PartDesign::Pad] Pad048
  Direction = (0,0,1)
  Length = 3
  Length2 = 10
  Profile = -> Sketch141
  ReferenceAxis = -> Sketch141 [N_Axis]
  Refine = true
  Suppressed = false
  Type = 0
FEATURE [Sketcher::SketchObject] Sketch142
  ArcFitTolerance = 1e-06
  AttachmentSupport = -> [Pad048]
  FullyConstrained = false
  MakeInternals = false
  MapMode = 5
  Placement = pos=(0,0,3) rot=(0,0,1;0rad)
  sketch-geometry (2):
    g0: Circle CenterX=0 CenterY=0 CenterZ=0 NormalX=0 NormalY=0 NormalZ=1 AngleXU=0 Radius=2.65687
    g1: Circle CenterX=0 CenterY=0 CenterZ=0 NormalX=0 NormalY=0 NormalZ=1 AngleXU=0 Radius=4.19276
  constraints (2):
    c: Coincident(g0,g-1)
    c: Coincident(g1,g0)
FEATURE [PartDesign::Pad] Pad049
  BaseFeature = -> Pad048
  Direction = (0,0,1)
  Length = 1
  Length2 = 10
  Profile = -> Sketch142
  ReferenceAxis = -> Sketch142 [N_Axis]
  Refine = true
  Reversed = true
  Suppressed = false
  Type = 0
FEATURE [PartDesign::Body] Body034  label="3x3 flanged001"
  AllowCompound = false
  Group = -> [Sketch141,Pad048,Sketch142,Pad049]
  Origin = -> Origin044
  Placement = pos=(11.5,0,0) rot=(0,0,1;0rad)
  Tip = -> Pad049
FEATURE [Sketcher::SketchObject] Sketch143
  ArcFitTolerance = 1e-06
  AttachmentSupport = -> [XY_Plane045]
  FullyConstrained = true
  MakeInternals = false
  MapMode = 5
  sketch-geometry (2):
    g0: Circle CenterX=0 CenterY=0 CenterZ=0 NormalX=0 NormalY=0 NormalZ=1 AngleXU=0 Radius=5.75
    g1: Circle CenterX=0 CenterY=0 CenterZ=0 NormalX=0 NormalY=0 NormalZ=1 AngleXU=0 Radius=4.05
  constraints (4):
    c: Coincident(g0,g-1)
    c: Coincident(g1,g0)
    c: Diameter(g1) = 8.1
    c: Diameter(g0) = 11.5
FEATURE [PartDesign::Pad] Pad050
  Direction = (0,0,1)
  Length = 2
  Length2 = 10
  Profile = -> Sketch143
  ReferenceAxis = -> Sketch143 [N_Axis]
  Refine = true
  Suppressed = false
  Type = 0
FEATURE [PartDesign::Body] Body035  label="8x2"
  AllowCompound = false
  Group = -> [Sketch143,Pad050]
  Origin = -> Origin045
  Tip = -> Pad050
FEATURE [Sketcher::SketchObject] Sketch144
  ArcFitTolerance = 1e-06
  AttachmentSupport = -> [XY_Plane046]
  FullyConstrained = true
  MakeInternals = false
  MapMode = 5
  sketch-geometry (2):
    g0: Circle CenterX=0 CenterY=0 CenterZ=0 NormalX=0 NormalY=0 NormalZ=1 AngleXU=0 Radius=5.75
    g1: Circle CenterX=0 CenterY=0 CenterZ=0 NormalX=0 NormalY=0 NormalZ=1 AngleXU=0 Radius=4.05
  constraints (4):
    c: Coincident(g0,g-1)
    c: Coincident(g1,g0)
    c: Diameter(g1) = 8.1
    c: Diameter(g0) = 11.5
FEATURE [PartDesign::Pad] Pad051
  Direction = (0,0,1)
  Length = 1.5
  Length2 = 10
  Profile = -> Sketch144
  ReferenceAxis = -> Sketch144 [N_Axis]
  Refine = true
  Suppressed = false
  Type = 0
FEATURE [PartDesign::Body] Body036  label="8x1.5"
  AllowCompound = false
  Group = -> [Sketch144,Pad051]
  Origin = -> Origin046
  Placement = pos=(-30,0,0) rot=(0,0,1;0rad)
  Tip = -> Pad051
FEATURE [Sketcher::SketchObject] Sketch145
  ArcFitTolerance = 1e-06
  AttachmentSupport = -> [XY_Plane047]
  FullyConstrained = true
  MakeInternals = false
  MapMode = 5
  sketch-geometry (2):
    g0: Circle CenterX=0 CenterY=0 CenterZ=0 NormalX=0 NormalY=0 NormalZ=1 AngleXU=0 Radius=1.8
    g1: Circle CenterX=0 CenterY=0 CenterZ=0 NormalX=0 NormalY=0 NormalZ=1 AngleXU=0 Radius=1.5
  constraints (4):
    c: Coincident(g0,g-1)
    c: Coincident(g1,g0)
    c: Diameter(g1) = 3
    c: Diameter(g0) = 3.6
FEATURE [PartDesign::Pad] Pad052
  Direction = (0,0,1)
  Length = 2
  Length2 = 10
  Profile = -> Sketch145
  ReferenceAxis = -> Sketch145 [N_Axis]
  Refine = true
  Suppressed = false
  Type = 0
FEATURE [PartDesign::Body] Body037  label="3x2"
  AllowCompound = false
  Group = -> [Sketch145,Pad052]
  Origin = -> Origin047
  Placement = pos=(-10,8,0) rot=(0,0,1;0rad)
  Tip = -> Pad052
FEATURE [Sketcher::SketchObject] Sketch146
  ArcFitTolerance = 1e-06
  AttachmentSupport = -> [Pad046]
  FullyConstrained = false
  MakeInternals = false
  MapMode = 5
  Placement = pos=(0,0,0) rot=(1,0,0;3.14159rad)
  sketch-geometry (2):
    g0: Circle CenterX=0 CenterY=0 CenterZ=0 NormalX=0 NormalY=0 NormalZ=1 AngleXU=0 Radius=2.46238
    g1: Circle CenterX=0 CenterY=0 CenterZ=0 NormalX=0 NormalY=0 NormalZ=1 AngleXU=0 Radius=1.65012
  constraints (2):
    c: Coincident(g0,g-1)
    c: Coincident(g1,g0)
FEATURE [PartDesign::Pad] Pad053
  BaseFeature = -> Pad046
  Direction = (0,0,-1)
  Length = 1
  Length2 = 10
  Profile = -> Sketch146
  ReferenceAxis = -> Sketch146 [N_Axis]
  Refine = true
  Reversed = true
  Suppressed = false
  Type = 0
FEATURE [PartDesign::Body] Body033  label="3x2 flanged"
  AllowCompound = false
  Group = -> [Sketch139,Pad046,Sketch146,Pad053]
  Origin = -> Origin043
  Placement = pos=(-18,12.5,0) rot=(0,0,1;0rad)
  Tip = -> Pad053
FEATURE [App::Part] Part004  label="SUPPLEMENTS"
  Group = -> [Body033,Body034,Body035,Body036,Body037]
  Origin = -> Origin042
FEATURE [Sketcher::SketchObject] Sketch147
  ArcFitTolerance = 1e-06
  AttachmentSupport = -> [XY_Plane048]
  FullyConstrained = false
  MakeInternals = false
  MapMode = 5
  sketch-geometry (26):
    g0: LineSegment [constr] StartX=-23 StartY=-5 StartZ=0 EndX=-21 EndY=217 EndZ=0
    g1: LineSegment [constr] StartX=23 StartY=-5 StartZ=0 EndX=21 EndY=217 EndZ=0
    g2: Circle [constr] CenterX=5e-16 CenterY=210 CenterZ=0 NormalX=0 NormalY=0 NormalZ=1 AngleXU=0 Radius=8.1
    g3: LineSegment [constr] StartX=-7 StartY=231 StartZ=0 EndX=7 EndY=231 EndZ=0
    g4: ArcOfCircle [constr] CenterX=5e-16 CenterY=210 CenterZ=0 NormalX=0 NormalY=0 NormalZ=1 AngleXU=0 Radius=22.1359 StartAngle=1.89255 EndAngle=2.81984
    g5: ArcOfCircle [constr] CenterX=5e-16 CenterY=210 CenterZ=0 NormalX=0 NormalY=0 NormalZ=1 AngleXU=0 Radius=22.1359 StartAngle=0.321751 EndAngle=1.24905
    g6: LineSegment [constr] StartX=-10.6301 StartY=-21 StartZ=0 EndX=10.6301 EndY=-21 EndZ=0
    g7: ArcOfCircle [constr] CenterX=0 CenterY=0 CenterZ=0 NormalX=0 NormalY=0 NormalZ=1 AngleXU=0 Radius=23.5372 StartAngle=3.35565 EndAngle=4.2438
    g8: ArcOfCircle [constr] CenterX=0 CenterY=0 CenterZ=0 NormalX=0 NormalY=0 NormalZ=1 AngleXU=0 Radius=23.5372 StartAngle=5.18098 EndAngle=6.06912
    g9: GeomPoint [constr] X=32.4275 Y=0 Z=0
    g10: LineSegment [constr] StartX=-26.3649 StartY=10 StartZ=0 EndX=51.8651 EndY=10 EndZ=0
    g11: LineSegment [constr] StartX=0 StartY=0 StartZ=0 EndX=-35.3086 EndY=-7.67578 EndZ=0
    g12: LineSegment [constr] StartX=-40.8172 StartY=200 StartZ=0 EndX=71.5323 EndY=200 EndZ=0
    g13: LineSegment StartX=-7 StartY=231 StartZ=0 EndX=7 EndY=231 EndZ=0
    g14: ArcOfCircle CenterX=5e-16 CenterY=210 CenterZ=0 NormalX=0 NormalY=0 NormalZ=1 AngleXU=0 Radius=22.1359 StartAngle=0.321751 EndAngle=1.24905
    g15: ArcOfCircle CenterX=5e-16 CenterY=210 CenterZ=0 NormalX=0 NormalY=0 NormalZ=1 AngleXU=0 Radius=25.8142 StartAngle=0.321751 EndAngle=1.83057
    g16: ArcOfCircle CenterX=5e-16 CenterY=210 CenterZ=0 NormalX=0 NormalY=0 NormalZ=1 AngleXU=0 Radius=25.8142 StartAngle=1.83057 EndAngle=2.81984
    g17: ArcOfCircle CenterX=0 CenterY=210 CenterZ=0 NormalX=0 NormalY=0 NormalZ=1 AngleXU=0 Radius=22.1359 StartAngle=1.89255 EndAngle=2.81984
    g18: LineSegment StartX=-24.4895 StartY=218.163 StartZ=0 EndX=-24.6532 EndY=200 EndZ=0
    g19: LineSegment StartX=-24.6532 StartY=200 StartZ=0 EndX=-21.1532 EndY=200 EndZ=0
    g20: LineSegment StartX=-21 StartY=217 StartZ=0 EndX=-21.1532 EndY=200 EndZ=0
    g21: LineSegment StartX=21 StartY=217 StartZ=0 EndX=21.1532 EndY=200 EndZ=0
    g22: LineSegment StartX=24.4895 StartY=218.163 StartZ=0 EndX=24.6532 EndY=200 EndZ=0
    g23: LineSegment StartX=21.1532 StartY=200 StartZ=0 EndX=24.6532 EndY=200 EndZ=0
    g24: LineSegment [constr] StartX=0 StartY=210 StartZ=0 EndX=-24.4895 EndY=218.163 EndZ=0
    g25: LineSegment [constr] StartX=5e-16 StartY=210 StartZ=0 EndX=24.4895 EndY=218.163 EndZ=0
  constraints (65):
    c: Symmetric(g3,g3,g-2)
    c: DistanceY(g2,g3) = 21
    c: Coincident(g4,g2)
    c: Coincident(g4,g3)
    c: Coincident(g4,g0)
    c: Coincident(g5,g2)
    c: Coincident(g5,g3)
    c: Coincident(g5,g1)
    c: Symmetric(g6,g6,g-2)
    c: Coincident(g7,g0)
    c: Coincident(g7,g6)
    c: Coincident(g8,g1)
    c: Coincident(g8,g6)
    c: PointOnObject(g9,g-1)
    c: DistanceY(g9,g2) = 210
    c: Diameter(g2) = 16.2
    c: Horizontal(g0,g1)
    c: DistanceX(g0,g1) = 46
    c: Symmetric(g0,g1,g-2)
    c: DistanceX(g0,g1) = 42
    c: DistanceY(g2,g1) = 7
    c: Coincident(g7,g8)
    c: Coincident(g7,g-1)
    c: DistanceY(g0,g7) = 5
    c: DistanceY(g6,g7) = 21
    c: Horizontal(g10)
    c: DistanceY(g7,g10) = 10
    c: Coincident(g11,g7)
    c: PointOnObject(g0,g11)
    c: Horizontal(g12)
    c: DistanceY(g12,g2) = 10
    c: Coincident(g13,g3)
    c: Coincident(g13,g3)
    c: Coincident(g14,g2)
    c: Coincident(g14,g3)
    c: Coincident(g16,g15)
    c: Coincident(g18,g16)
    c: PointOnObject(g18,g12)
    c: Coincident(g19,g18)
    c: PointOnObject(g19,g12)
    c: Coincident(g20,g17)
    c: Coincident(g20,g19)
    c: DistanceX(g18,g19) = 3.5
    c: PointOnObject(g19,g0)
    c: Parallel(g18,g20)
    c: Coincident(g17,g0)
    c: Coincident(g21,g14)
    c: PointOnObject(g21,g12)
    c: Coincident(g22,g15)
    c: PointOnObject(g22,g12)
    c: Coincident(g23,g21)
    c: Coincident(g23,g22)
    c: Equal(g19,g23)
    c: PointOnObject(g21,g1)
    c: Coincident(g17,g3)
    c: Parallel(g22,g21)
    c: Coincident(g15,g2)
    c: PointOnObject(g17,g-2)
    c: Coincident(g24,g17)
    c: Coincident(g24,g16)
    c: PointOnObject(g0,g24)
    c: Coincident(g25,g2)
    c: Coincident(g25,g15)
    c: PointOnObject(g14,g25)
    c: Coincident(g16,g15)
FEATURE [PartDesign::Pad] Pad054
  Direction = (0,0,1)
  Length = 28
  Length2 = 10
  Profile = -> Sketch147
  ReferenceAxis = -> Sketch147 [N_Axis]
  Refine = true
  Reversed = true
  Suppressed = false
  Type = 0
FEATURE [Sketcher::SketchObject] Sketch148
  ArcFitTolerance = 1e-06
  AttachmentOffset = pos=(0,0,-6) rot=(0,0,1;0rad)
  AttachmentSupport = -> [Pad054]
  ExternalGeometry = -> [Pad054]
  FullyConstrained = false
  MakeInternals = false
  MapMode = 5
  Placement = pos=(0,0,-6) rot=(0,0,1;0rad)
  sketch-geometry (5):
    g0: LineSegment [constr] StartX=-36.3908 StartY=210 StartZ=0 EndX=46.9754 EndY=210 EndZ=0
    g1: ArcOfCircle CenterX=0 CenterY=210 CenterZ=0 NormalX=0 NormalY=0 NormalZ=1 AngleXU=0 Radius=16.9366 StartAngle=3e-16 EndAngle=3.14159
    g2: ArcOfCircle CenterX=0 CenterY=210 CenterZ=0 NormalX=0 NormalY=0 NormalZ=1 AngleXU=0 Radius=23.494 StartAngle=0 EndAngle=3.14159
    g3: LineSegment StartX=-16.9366 StartY=210 StartZ=0 EndX=-23.494 EndY=210 EndZ=0
    g4: LineSegment StartX=23.494 StartY=210 StartZ=0 EndX=16.9366 EndY=210 EndZ=0
  constraints (13):
    c: Horizontal(g0)
    c: DistanceY(g-3,g0) = 10
    c: PointOnObject(g1,g0)
    c: Coincident(g2,g1)
    c: Coincident(g3,g1)
    c: Coincident(g4,g2)
    c: Coincident(g4,g1)
    c: Horizontal(g4)
    c: Horizontal(g3)
    c: PointOnObject(g1,g-2)
    c: Coincident(g2,g3)
    c: PointOnObject(g1,g0)
    c: PointOnObject(g1,g0)
FEATURE [PartDesign::Pad] Pad055
  BaseFeature = -> Pad054
  Direction = (0,0,1)
  Length = 16
  Length2 = 10
  Profile = -> Sketch148
  ReferenceAxis = -> Sketch148 [N_Axis]
  Refine = true
  Reversed = true
  Suppressed = false
  Type = 0
FEATURE [Sketcher::SketchObject] Sketch149
  ArcFitTolerance = 1e-06
  AttachmentSupport = -> [Pad055]
  ExternalGeometry = -> [Pad055]
  FullyConstrained = true
  MakeInternals = false
  MapMode = 5
  Placement = pos=(0,200,0) rot=(1,0,0;1.5708rad)
  sketch-geometry (8):
    g0: LineSegment StartX=-21.1532 StartY=-9 StartZ=0 EndX=-21.1532 EndY=-19 EndZ=0
    g1: LineSegment StartX=-21.1532 StartY=-19 StartZ=0 EndX=-18.1532 EndY=-19 EndZ=0
    g2: LineSegment StartX=-18.1532 StartY=-19 StartZ=0 EndX=-18.1532 EndY=-9 EndZ=0
    g3: LineSegment StartX=-18.1532 StartY=-9 StartZ=0 EndX=-21.1532 EndY=-9 EndZ=0
    g4: LineSegment StartX=21.1532 StartY=-9 StartZ=0 EndX=18.1532 EndY=-9 EndZ=0
    g5: LineSegment StartX=18.1532 StartY=-9 StartZ=0 EndX=18.1532 EndY=-19 EndZ=0
    g6: LineSegment StartX=18.1532 StartY=-19 StartZ=0 EndX=21.1532 EndY=-19 EndZ=0
    g7: LineSegment StartX=21.1532 StartY=-19 StartZ=0 EndX=21.1532 EndY=-9 EndZ=0
  constraints (24):
    c: Coincident(g0,g1)
    c: Coincident(g1,g2)
    c: Coincident(g2,g3)
    c: Coincident(g3,g0)
    c: Vertical(g0)
    c: Vertical(g2)
    c: Horizontal(g1)
    c: Horizontal(g3)
    c: PointOnObject(g0,g-4)
    c: Coincident(g4,g5)
    c: Coincident(g5,g6)
    c: Coincident(g6,g7)
    c: Coincident(g7,g4)
    c: Horizontal(g4)
    c: Horizontal(g6)
    c: Vertical(g5)
    c: Vertical(g7)
    c: PointOnObject(g4,g-3)
    c: DistanceY(g4,g-3) = 9
    c: Horizontal(g4,g2)
    c: Horizontal(g1,g5)
    c: DistanceX(g0,g2) = 3
    c: DistanceX(g4,g4) = 3
    c: DistanceY(g-5,g6) = 9
FEATURE [PartDesign::Pad] Pad056
  BaseFeature = -> Pad055
  Direction = (0,-1,2e-16)
  Length = 5
  Length2 = 23
  Profile = -> Sketch149
  ReferenceAxis = -> Sketch149 [N_Axis]
  Refine = true
  Suppressed = false
  Type = 4
FEATURE [Sketcher::SketchObject] Sketch151
  ArcFitTolerance = 1e-06
  FullyConstrained = true
  MakeInternals = false
  MapMode = 5
  Placement = pos=(0,234.5,0) rot=(0,0.707107,0.707107;3.14159rad)
  sketch-geometry (2):
    g0: Circle CenterX=0 CenterY=-3 CenterZ=0 NormalX=0 NormalY=0 NormalZ=1 AngleXU=0 Radius=2.25
    g1: Circle CenterX=0 CenterY=-25 CenterZ=0 NormalX=0 NormalY=0 NormalZ=1 AngleXU=0 Radius=2.25
  constraints (6):
    c: PointOnObject(g0,g-2)
    c: PointOnObject(g1,g-2)
    c: DistanceY(g-3,g1) = 3
    c: DistanceY(g0,g-1) = 3
    c: Equal(g0,g1)
    c: Diameter(g0) = 4.5
FEATURE [PartDesign::Pocket] Pocket079
  BaseFeature = -> Pad056
  Direction = (0,-1,2e-16)
  Length = 1.5
  Length2 = 5
  Profile = -> Sketch151
  ReferenceAxis = -> Sketch151 [N_Axis]
  Refine = true
  Suppressed = false
  Type = 0
FEATURE [Sketcher::SketchObject] Sketch152
  ArcFitTolerance = 1e-06
  AttachmentSupport = -> [Pocket079]
  ExternalGeometry = -> [Pocket079]
  FullyConstrained = true
  MakeInternals = false
  MapMode = 5
  Placement = pos=(-26.4528,0.238314,0) rot=(-0.573883,0.579076,0.579076;4.18358rad)
  sketch-geometry (4):
    g0: LineSegment StartX=-203.77 StartY=-2 StartZ=0 EndX=-203.77 EndY=-26 EndZ=0
    g1: LineSegment StartX=-203.77 StartY=-26 StartZ=0 EndX=-195.77 EndY=-26 EndZ=0
    g2: LineSegment StartX=-195.77 StartY=-26 StartZ=0 EndX=-195.77 EndY=-2 EndZ=0
    g3: LineSegment StartX=-195.77 StartY=-2 StartZ=0 EndX=-203.77 EndY=-2 EndZ=0
  constraints (11):
    c: Coincident(g0,g1)
    c: Coincident(g1,g2)
    c: Coincident(g2,g3)
    c: Coincident(g3,g0)
    c: Vertical(g0)
    c: Vertical(g2)
    c: Horizontal(g1)
    c: DistanceY(g0,g-3) = 2
    c: DistanceY(g-4,g0) = 2
    c: DistanceX(g0,g2) = 8
    c: Symmetric(g0,g2,g-3)
FEATURE [PartDesign::Pad] Pad057
  BaseFeature = -> Pocket079
  Direction = (-0.999959,0.00900864,2e-16)
  Length = 2.6
  Length2 = 10
  Midplane = true
  Profile = -> Sketch152
  ReferenceAxis = -> Sketch152 [N_Axis]
  Refine = true
  Suppressed = false
  Type = 0
FEATURE [Sketcher::SketchObject] Sketch154
  ArcFitTolerance = 1e-06
  AttachmentSupport = -> [XY_Plane049]
  FullyConstrained = false
  MakeInternals = false
  MapMode = 5
  sketch-geometry (15):
    g0: LineSegment [constr] StartX=-57.1554 StartY=-10 StartZ=0 EndX=57.5501 EndY=-10 EndZ=0
    g1: GeomPoint [constr] X=58.1891 Y=0 Z=0
    g2: LineSegment [constr] StartX=-29.894 StartY=17 StartZ=0 EndX=47.0152 EndY=17 EndZ=0
    g3: LineSegment StartX=-21 StartY=-10 StartZ=0 EndX=-21 EndY=0 EndZ=0
    g4: LineSegment StartX=-21 StartY=0 StartZ=0 EndX=-14.065 EndY=17 EndZ=0
    g5: LineSegment StartX=21 StartY=-10 StartZ=0 EndX=21 EndY=0 EndZ=0
    g6: LineSegment StartX=21 StartY=0 StartZ=0 EndX=14.065 EndY=17 EndZ=0
    g7: ArcOfCircle CenterX=0 CenterY=10.8531 CenterZ=0 NormalX=0 NormalY=0 NormalZ=1 AngleXU=0 Radius=15.3496 StartAngle=0.412022 EndAngle=2.72957
    g8: LineSegment StartX=24.5 StartY=-10 StartZ=0 EndX=24.5 EndY=0 EndZ=0
    g9: LineSegment StartX=-24.5 StartY=-10 StartZ=0 EndX=-24.5 EndY=0 EndZ=0
    g10: LineSegment StartX=-24.5 StartY=0 StartZ=0 EndX=-17.565 EndY=17 EndZ=0
    g11: LineSegment StartX=24.5 StartY=0 StartZ=0 EndX=17.565 EndY=17 EndZ=0
    g12: ArcOfCircle CenterX=0 CenterY=10.9476 CenterZ=0 NormalX=0 NormalY=0 NormalZ=1 AngleXU=0 Radius=18.5785 StartAngle=0.331831 EndAngle=2.80976
    g13: LineSegment StartX=21 StartY=-10 StartZ=0 EndX=24.5 EndY=-10 EndZ=0
    g14: LineSegment StartX=-21 StartY=-10 StartZ=0 EndX=-24.5 EndY=-10 EndZ=0
  constraints (40):
    c: Horizontal(g0)
    c: PointOnObject(g1,g-1)
    c: DistanceY(g0,g1) = 10
    c: Horizontal(g2)
    c: DistanceY(g1,g2) = 17
    c: PointOnObject(g3,g0)
    c: PointOnObject(g3,g-1)
    c: Vertical(g3)
    c: Coincident(g4,g3)
    c: PointOnObject(g4,g2)
    c: PointOnObject(g5,g-1)
    c: Vertical(g5)
    c: Coincident(g6,g5)
    c: PointOnObject(g6,g2)
    c: Symmetric(g5,g3,g-2)
    c: DistanceX(g3,g5) = 42
    c: PointOnObject(g8,g0)
    c: PointOnObject(g8,g-1)
    c: Vertical(g8)
    c: PointOnObject(g9,g0)
    c: PointOnObject(g9,g-1)
    c: Vertical(g9)
    c: Coincident(g10,g9)
    c: PointOnObject(g10,g2)
    c: Coincident(g11,g8)
    c: PointOnObject(g11,g2)
    c: DistanceX(g5,g8) = 3.5
    c: DistanceX(g9,g3) = 3.5
    c: Coincident(g7,g4)
    c: Coincident(g6,g7)
    c: PointOnObject(g7,g-2)
    c: PointOnObject(g12,g-2)
    c: Coincident(g12,g10)
    c: Coincident(g12,g11)
    c: Parallel(g6,g11)
    c: Coincident(g13,g5)
    c: Coincident(g13,g8)
    c: Coincident(g14,g3)
    c: Coincident(g14,g9)
    c: DistanceX(g4,g6) = 28.13
FEATURE [PartDesign::Pad] Pad059
  Direction = (0,0,1)
  Length = 38
  Length2 = 10
  Profile = -> Sketch154
  ReferenceAxis = -> Sketch154 [N_Axis]
  Refine = true
  Suppressed = false
  Type = 0
FEATURE [Sketcher::SketchObject] Sketch155
  ArcFitTolerance = 1e-06
  AttachmentSupport = -> [Pad059]
  FullyConstrained = false
  MakeInternals = false
  MapMode = 5
  Placement = pos=(-21.0045,8.56861,0) rot=(-0.429221,0.638659,0.638659;3.95247rad)
  sketch-geometry (3):
    g0: LineSegment [constr] StartX=22.8711 StartY=34 StartZ=0 EndX=-49.7164 EndY=34 EndZ=0
    g1: Circle CenterX=-0.804323 CenterY=3 CenterZ=0 NormalX=0 NormalY=0 NormalZ=1 AngleXU=0 Radius=1.25
    g2: Circle CenterX=-0.804323 CenterY=31 CenterZ=0 NormalX=0 NormalY=0 NormalZ=1 AngleXU=0 Radius=1.25
  constraints (7):
    c: Horizontal(g0)
    c: DistanceY(g-1,g0) = 34
    c: Equal(g2,g1)
    c: Diameter(g2) = 2.5
    c: DistanceY(g-1,g1) = 3
    c: DistanceY(g2,g0) = 3
    c: Vertical(g2,g1)
FEATURE [PartDesign::Pocket] Pocket080
  BaseFeature = -> Pad059
  Direction = (0.92592,-0.377721,0)
  Length = 5
  Length2 = 5
  Profile = -> Sketch155
  ReferenceAxis = -> Sketch155 [N_Axis]
  Refine = true
  Suppressed = false
  Type = 0
FEATURE [Sketcher::SketchObject] Sketch156
  ArcFitTolerance = 1e-06
  AttachmentSupport = -> [Pocket080]
  ExternalGeometry = -> [Pocket080]
  FullyConstrained = false
  MakeInternals = false
  MapMode = 5
  Placement = pos=(-24.5,0,0) rot=(0.57735,-0.57735,-0.57735;2.0944rad)
  sketch-geometry (5):
    g0: ArcOfCircle CenterX=10 CenterY=25.9375 CenterZ=0 NormalX=0 NormalY=0 NormalZ=1 AngleXU=0 Radius=3.76862 StartAngle=4e-16 EndAngle=3.14159
    g1: ArcOfCircle CenterX=10 CenterY=8 CenterZ=0 NormalX=0 NormalY=0 NormalZ=1 AngleXU=0 Radius=3.76862 StartAngle=3.14159 EndAngle=6.28319
    g2: LineSegment StartX=13.7686 StartY=25.9375 StartZ=0 EndX=13.7686 EndY=8 EndZ=0
    g3: LineSegment StartX=6.23138 StartY=25.9375 StartZ=0 EndX=6.23138 EndY=8 EndZ=0
    g4: LineSegment [constr] StartX=18.2375 StartY=33.9375 StartZ=0 EndX=-3.15402 EndY=33.9375 EndZ=0
  constraints (10):
    c: Tangent(g0,g2) = 1.5708
    c: Tangent(g0,g3) = -1.5708
    c: Tangent(g1,g2) = 1.5708
    c: Tangent(g1,g3) = -1.5708
    c: Equal(g0,g1)
    c: Vertical(g3)
    c: PointOnObject(g0,g-3)
    c: DistanceY(g-3,g1) = 8
    c: Horizontal(g4)
    c: DistanceY(g0,g4) = 8
FEATURE [PartDesign::Pad] Pad060
  BaseFeature = -> Pocket080
  Direction = (-1,0,0)
  Length = 3
  Length2 = 10
  Midplane = true
  Profile = -> Sketch156
  ReferenceAxis = -> Sketch156 [N_Axis]
  Refine = true
  Suppressed = false
  Type = 0
FEATURE [Sketcher::SketchObject] Sketch157
  ArcFitTolerance = 1e-06
  AttachmentOffset = pos=(0,0,-9.84) rot=(0,0,1;0rad)
  AttachmentSupport = -> [Pad060]
  FullyConstrained = false
  MakeInternals = false
  MapMode = 5
  Placement = pos=(0,0,28.16) rot=(0,0,1;0rad)
  sketch-geometry (2):
    g0: ArcOfCircle CenterX=0 CenterY=9.60559 CenterZ=0 NormalX=0 NormalY=0 NormalZ=1 AngleXU=0 Radius=17.6844 StartAngle=0.623499 EndAngle=2.51809
    g1: LineSegment StartX=-14.3569 StartY=19.9311 StartZ=0 EndX=14.3569 EndY=19.9311 EndZ=0
  constraints (4):
    c: PointOnObject(g0,g-2)
    c: Coincident(g1,g0)
    c: Coincident(g1,g0)
    c: Horizontal(g1)
FEATURE [PartDesign::Pad] Pad061
  BaseFeature = -> Pad060
  Direction = (0,0,1)
  Length = 22.5
  Length2 = 10
  Profile = -> Sketch157
  ReferenceAxis = -> Sketch157 [N_Axis]
  Refine = true
  Reversed = true
  Suppressed = false
  Type = 0
FEATURE [Sketcher::SketchObject] Sketch158
  ArcFitTolerance = 1e-06
  AttachmentSupport = -> [Pad061]
  ExternalGeometry = -> [Pad061]
  FullyConstrained = true
  MakeInternals = false
  MapMode = 5
  Placement = pos=(-24.5,0,0) rot=(0.57735,-0.57735,-0.57735;2.0944rad)
FEATURE [Sketcher::SketchObject] Sketch159
  ArcFitTolerance = 1e-06
  AttachmentSupport = -> [Pad061]
  FullyConstrained = false
  MakeInternals = false
  MapMode = 5
  Placement = pos=(21.0045,8.56861,0) rot=(0.429221,0.638659,0.638659;2.33071rad)
  sketch-geometry (4):
    g0: LineSegment [constr] StartX=0.807052 StartY=-2.96774 StartZ=0 EndX=0.807052 EndY=39.9353 EndZ=0
    g1: Circle CenterX=0.807052 CenterY=3 CenterZ=0 NormalX=0 NormalY=0 NormalZ=1 AngleXU=0 Radius=1.25
    g2: Circle CenterX=0.807052 CenterY=30.9922 CenterZ=0 NormalX=0 NormalY=0 NormalZ=1 AngleXU=0 Radius=1.25
    g3: LineSegment [constr] StartX=-20.2662 StartY=33.9922 StartZ=0 EndX=10.1774 EndY=33.9922 EndZ=0
  constraints (9):
    c: Vertical(g0)
    c: PointOnObject(g1,g0)
    c: PointOnObject(g2,g0)
    c: Horizontal(g3)
    c: Block(g3)
    c: DistanceY(g2,g3) = 3
    c: DistanceY(g-1,g1) = 3
    c: Equal(g1,g2)
    c: Diameter(g1) = 2.5
FEATURE [PartDesign::Pocket] Pocket081
  BaseFeature = -> Pad061
  Direction = (-0.92592,-0.377721,0)
  Length = 5
  Length2 = 5
  Profile = -> Sketch159
  ReferenceAxis = -> Sketch159 [N_Axis]
  Refine = true
  Suppressed = false
  Type = 0
FEATURE [Sketcher::SketchObject] Sketch160
  ArcFitTolerance = 1e-06
  AttachmentSupport = -> [Pocket081]
  ExternalGeometry = -> [Pocket081]
  FullyConstrained = true
  MakeInternals = false
  MapMode = 5
  Placement = pos=(24.5,0,0) rot=(0.57735,0.57735,0.57735;2.0944rad)
  sketch-geometry (4):
    g0: ArcOfCircle CenterX=-10 CenterY=8 CenterZ=0 NormalX=0 NormalY=0 NormalZ=1 AngleXU=0 Radius=4 StartAngle=3.14159 EndAngle=6.28319
    g1: ArcOfCircle CenterX=-10 CenterY=26 CenterZ=0 NormalX=0 NormalY=0 NormalZ=1 AngleXU=0 Radius=4 StartAngle=9e-16 EndAngle=3.14159
    g2: LineSegment StartX=-14 StartY=8 StartZ=0 EndX=-14 EndY=26 EndZ=0
    g3: LineSegment StartX=-6 StartY=8 StartZ=0 EndX=-6 EndY=26 EndZ=0
  constraints (10):
    c: Tangent(g0,g2) = 1.5708
    c: Tangent(g0,g3) = -1.5708
    c: Tangent(g1,g2) = 1.5708
    c: Tangent(g1,g3) = -1.5708
    c: Equal(g0,g1)
    c: Vertical(g3)
    c: PointOnObject(g0,g-3)
    c: Diameter(g1) = 8
    c: DistanceY(g-3,g0) = 8
    c: DistanceY(g1,g-3) = 12
FEATURE [PartDesign::Pad] Pad062
  BaseFeature = -> Pocket081
  Direction = (1,0,0)
  Length = 3
  Length2 = 10
  Midplane = true
  Profile = -> Sketch160
  ReferenceAxis = -> Sketch160 [N_Axis]
  Refine = true
  Suppressed = false
  Type = 0
FEATURE [Sketcher::SketchObject] Sketch161
  ArcFitTolerance = 1e-06
  AttachmentSupport = -> [Pad062]
  FullyConstrained = true
  MakeInternals = false
  MapMode = 5
  Placement = pos=(21,0,0) rot=(0.57735,-0.57735,-0.57735;2.0944rad)
FEATURE [Sketcher::SketchObject] Sketch162
  ArcFitTolerance = 1e-06
  AttachmentSupport = -> [Pad062]
  ExternalGeometry = -> [Pad062]
  FullyConstrained = false
  MakeInternals = false
  MapMode = 5
  Placement = pos=(0,-10,0) rot=(1,0,0;1.5708rad)
  sketch-geometry (9):
    g0: LineSegment [constr] StartX=35.2818 StartY=33.66 StartZ=0 EndX=-36.4376 EndY=33.66 EndZ=0
    g1: LineSegment StartX=-21 StartY=24.66 StartZ=0 EndX=-21 EndY=9 EndZ=0
    g2: LineSegment StartX=-21 StartY=9 StartZ=0 EndX=-17.5 EndY=9 EndZ=0
    g3: LineSegment StartX=-17.5 StartY=9 StartZ=0 EndX=-17.5 EndY=24.66 EndZ=0
    g4: LineSegment StartX=-17.5 StartY=24.66 StartZ=0 EndX=-21 EndY=24.66 EndZ=0
    g5: LineSegment StartX=21 StartY=24.66 StartZ=0 EndX=17.5 EndY=24.66 EndZ=0
    g6: LineSegment StartX=17.5 StartY=24.66 StartZ=0 EndX=17.5 EndY=9 EndZ=0
    g7: LineSegment StartX=17.5 StartY=9 StartZ=0 EndX=21 EndY=9 EndZ=0
    g8: LineSegment StartX=21 StartY=9 StartZ=0 EndX=21 EndY=24.66 EndZ=0
  constraints (26):
    c: Horizontal(g0)
    c: DistanceY(g-4,g0) = 33.66
    c: Coincident(g1,g2)
    c: Coincident(g2,g3)
    c: Coincident(g3,g4)
    c: Coincident(g4,g1)
    c: Vertical(g1)
    c: Vertical(g3)
    c: Horizontal(g2)
    c: Horizontal(g4)
    c: PointOnObject(g1,g-4)
    c: Coincident(g5,g6)
    c: Coincident(g6,g7)
    c: Coincident(g7,g8)
    c: Coincident(g8,g5)
    c: Horizontal(g5)
    c: Horizontal(g7)
    c: Vertical(g6)
    c: Vertical(g8)
    c: PointOnObject(g5,g-3)
    c: Horizontal(g2,g6)
    c: Horizontal(g3,g5)
    c: DistanceX(g1,g3) = 3.5
    c: Equal(g4,g5)
    c: DistanceY(g-4,g1) = 9
    c: DistanceY(g1,g0) = 9
FEATURE [PartDesign::Pad] Pad063
  BaseFeature = -> Pad062
  Direction = (0,-1,2e-16)
  Length = 4
  Length2 = 10
  Midplane = true
  Profile = -> Sketch162
  ReferenceAxis = -> Sketch162 [N_Axis]
  Refine = true
  Suppressed = false
  Type = 4
FEATURE [PartDesign::Chamfer] Chamfer025
  Angle = 45
  Base = -> Pad063 [Edge71,Edge14,Edge10,Edge57]
  BaseFeature = -> Pad063
  ChamferType = 0
  FlipDirection = false
  Refine = true
  Size = 2
  Size2 = 1
  SupportTransform = false
  Suppressed = false
  UseAllEdges = false
FEATURE [PartDesign::Body] Body039  label="ELBOW SERVO ENT TIP"
  AllowCompound = false
  Group = -> [Sketch154,Pad059,Sketch155,Pocket080,Sketch156,Pad060,Sketch157,Pad061,Sketch158,Sketch159,Pocket081,Sketch160,Pad062,Sketch161,Sketch162,Pad063,Chamfer025]
  Origin = -> Origin049
  Placement = pos=(-0.1,170.1,-1) rot=(0,0,1;0rad)
  Tip = -> Chamfer025
FEATURE [Part::Feature] Part__Feature019  label="Board^Optical Endstop Switch"
  shape: bbox 33 x 1.612 x 10 mm, 109 faces (baked)
FEATURE [Part::Feature] Part__Feature020  label="TCST2103^Optical Endstop Switch"
  Placement = pos=(-0.05,1.6,-8.15) rot=(0,0,1;0rad)
  shape: bbox 24.75 x 13.8 x 6.711 mm, 252 faces (baked)
FEATURE [Part::Feature] Part__Feature021  label="RES_0805^Optical Endstop Switch"
  Placement = pos=(25.5,1.6,-1.86) rot=(0,0,1;0rad)
  shape: bbox 0.5 x 0.45 x 1.2 mm, 18 faces (baked)
FEATURE [Part::Feature] Part__Feature022  label="RES_0805^Optical Endstop Switch001"
  Placement = pos=(25.5,1.6,-1.86) rot=(0,0,1;0rad)
  shape: bbox 0.5 x 0.45 x 1.2 mm, 18 faces (baked)
FEATURE [Part::Feature] Part__Feature023  label="RES_0805^Optical Endstop Switch002"
  Placement = pos=(25.5,1.6,-1.86) rot=(0,0,1;0rad)
  shape: bbox 1.001 x 0.4813 x 1.201 mm, 64 faces (baked)
FEATURE [App::Part] RES_0805_Optical_Endstop_Switch  label="RES_0805^Optical Endstop Switch003"
  Group = -> [Part__Feature021,Part__Feature022,Part__Feature023]
  Origin = -> Origin050
FEATURE [Part::Feature] Part__Feature024  label="RES_0805^Optical Endstop Switch004"
  Placement = pos=(13.25,0,-2.2) rot=(0,0,1;3.14159rad)
  shape: bbox 0.5 x 0.45 x 1.2 mm, 18 faces (baked)
FEATURE [Part::Feature] Part__Feature025  label="RES_0805^Optical Endstop Switch005"
  Placement = pos=(13.25,0,-2.2) rot=(0,0,1;3.14159rad)
  shape: bbox 0.5 x 0.45 x 1.2 mm, 18 faces (baked)
FEATURE [Part::Feature] Part__Feature026  label="RES_0805^Optical Endstop Switch006"
  Placement = pos=(13.25,0,-2.2) rot=(0,0,1;3.14159rad)
  shape: bbox 1.001 x 0.4813 x 1.201 mm, 64 faces (baked)
FEATURE [App::Part] RES_0805_Optical_Endstop_Switch001  label="RES_0805^Optical Endstop Switch007"
  Group = -> [Part__Feature024,Part__Feature025,Part__Feature026]
  Origin = -> Origin051
FEATURE [Part::Feature] Part__Feature027  label="LED_0805_Green^Optical Endstop Switch"
  Placement = pos=(27.5,1.6,-5.625) rot=(0,1,0;3.14159rad)
  shape: bbox 1 x 0.28 x 1.25 mm, 6 faces (baked)
FEATURE [Part::Feature] Part__Feature028  label="LED_0805_Green^Optical Endstop Switch001"
  Placement = pos=(27.5,1.6,-5.625) rot=(0,1,0;3.14159rad)
  shape: bbox 0.4 x 0.28 x 1.25 mm, 8 faces (baked)
FEATURE [Part::Feature] Part__Feature029  label="LED_0805_Green^Optical Endstop Switch002"
  Placement = pos=(27.5,1.6,-5.625) rot=(0,1,0;3.14159rad)
  shape: bbox 0.4 x 0.28 x 1.25 mm, 8 faces (baked)
FEATURE [Part::Feature] Part__Feature030  label="LED_0805_Green^Optical Endstop Switch003"
  Placement = pos=(27.5,1.6,-5.625) rot=(0,1,0;3.14159rad)
  shape: bbox 1 x 0.4049 x 1.25 mm, 18 faces (baked)
FEATURE [App::Part] LED_0805_Green_Optical_Endstop_Switch  label="LED_0805_Green^Optical Endstop Switch004"
  Group = -> [Part__Feature027,Part__Feature028,Part__Feature029,Part__Feature030]
  Origin = -> Origin052
FEATURE [Part::Feature] Part__Feature031  label="RES_0805^Optical Endstop Switch008"
  Placement = pos=(13.25,0,-6.6) rot=(0,0,1;3.14159rad)
  shape: bbox 0.5 x 0.45 x 1.2 mm, 18 faces (baked)
FEATURE [Part::Feature] Part__Feature032  label="RES_0805^Optical Endstop Switch009"
  Placement = pos=(13.25,0,-6.6) rot=(0,0,1;3.14159rad)
  shape: bbox 0.5 x 0.45 x 1.2 mm, 18 faces (baked)
FEATURE [Part::Feature] Part__Feature033  label="RES_0805^Optical Endstop Switch010"
  Placement = pos=(13.25,0,-6.6) rot=(0,0,1;3.14159rad)
  shape: bbox 1.001 x 0.4813 x 1.201 mm, 64 faces (baked)
FEATURE [App::Part] RES_0805_Optical_Endstop_Switch002  label="RES_0805^Optical Endstop Switch011"
  Group = -> [Part__Feature031,Part__Feature032,Part__Feature033]
  Origin = -> Origin053
FEATURE [Part::Feature] Part__Feature034  label="JST-XH-3A^Optical Endstop Switch"
  Placement = pos=(32.67,0,-9.95) rot=(0.707107,0,0.707107;3.14159rad)
  shape: bbox 5.75 x 10.5 x 9.9 mm, 107 faces (baked)
FEATURE [App::Part] Optical_Endstop_Switch  label="Optical Endstop Switch"
  Group = -> [Part__Feature019,Part__Feature020,RES_0805_Optical_Endstop_Switch,RES_0805_Optical_Endstop_Switch001,LED_0805_Green_Optical_Endstop_Switch,RES_0805_Optical_Endstop_Switch002,Part__Feature034]
  Origin = -> Origin054
  Placement = pos=(-5,176.8,12.9) rot=(-0.57735,0.57735,0.57735;4.18879rad)
FEATURE [Sketcher::SketchObject] Sketch163
  ArcFitTolerance = 1e-06
  AttachmentOffset = pos=(0,0,-16) rot=(0,0,1;0rad)
  FullyConstrained = false
  MakeInternals = false
  MapMode = 5
  Placement = pos=(0,0,-12) rot=(1,0,0;3.14159rad)
  sketch-geometry (7):
    g0: LineSegment [constr] StartX=-56.2265 StartY=-208.837 StartZ=0 EndX=56.2265 EndY=-208.837 EndZ=0
    g1: ArcOfCircle CenterX=0 CenterY=-208.837 CenterZ=0 NormalX=0 NormalY=0 NormalZ=1 AngleXU=0 Radius=47 StartAngle=2.66046 EndAngle=6.76431
    g2: ArcOfCircle CenterX=0 CenterY=-208.837 CenterZ=0 NormalX=0 NormalY=0 NormalZ=1 AngleXU=0 Radius=23.076 StartAngle=3.14159 EndAngle=6.28319
    g3: LineSegment StartX=-23.076 StartY=-208.837 StartZ=0 EndX=-23.076 EndY=-200.38 EndZ=0
    g4: LineSegment StartX=-23.076 StartY=-200.38 StartZ=0 EndX=-41.6642 EndY=-187.086 EndZ=0
    g5: LineSegment StartX=23.076 StartY=-208.837 StartZ=0 EndX=23.076 EndY=-200.38 EndZ=0
    g6: LineSegment StartX=23.076 StartY=-200.38 StartZ=0 EndX=41.6642 EndY=-187.086 EndZ=0
  constraints (18):
    c: Horizontal(g0)
    c: Block(g0)
    c: Symmetric(g0,g0,g1)
    c: Radius(g1) = 47
    c: PointOnObject(g1,g-2)
    c: Coincident(g2,g1)
    c: Horizontal(g1,g1)
    c: Coincident(g3,g2)
    c: Coincident(g4,g3)
    c: Coincident(g4,g1)
    c: Coincident(g5,g2)
    c: Vertical(g5)
    c: Coincident(g6,g5)
    c: Coincident(g6,g1)
    c: PointOnObject(g2,g0)
    c: PointOnObject(g2,g0)
    c: Vertical(g3)
    c: Horizontal(g5,g3)
FEATURE [PartDesign::Pad] Pad064
  BaseFeature = -> Pad057
  Direction = (0,0,-1)
  Length = 2
  Length2 = 10
  Profile = -> Sketch163
  ReferenceAxis = -> Sketch163 [N_Axis]
  Refine = true
  Reversed = true
  Suppressed = false
  Type = 0
FEATURE [Sketcher::SketchObject] Sketch164
  ArcFitTolerance = 1e-06
  AttachmentSupport = -> [Pad064]
  ExternalGeometry = -> [Pad064]
  FullyConstrained = false
  MakeInternals = false
  MapMode = 5
  Placement = pos=(0,0,-10) rot=(0,0,1;0rad)
  sketch-geometry (4):
    g0: ArcOfCircle CenterX=0 CenterY=208.837 CenterZ=0 NormalX=0 NormalY=0 NormalZ=1 AngleXU=0 Radius=47 StartAngle=5.80206 EndAngle=9.90591
    g1: ArcOfCircle CenterX=0 CenterY=208.837 CenterZ=0 NormalX=0 NormalY=0 NormalZ=1 AngleXU=0 Radius=45.713 StartAngle=5.80602 EndAngle=9.90195
    g2: LineSegment StartX=-41.6642 StartY=187.086 StartZ=0 EndX=-40.6068 EndY=187.843 EndZ=0
    g3: LineSegment StartX=41.6642 StartY=187.086 StartZ=0 EndX=40.6068 EndY=187.843 EndZ=0
  constraints (10):
    c: Coincident(g0,g-3)
    c: Coincident(g0,g-3)
    c: Coincident(g1,g0)
    c: PointOnObject(g1,g-5)
    c: PointOnObject(g1,g-4)
    c: Distance(g0,g1) = 1.3
    c: Coincident(g2,g0)
    c: Coincident(g2,g1)
    c: Coincident(g3,g0)
    c: Coincident(g3,g1)
FEATURE [PartDesign::Pad] Pad065
  BaseFeature = -> Pad064
  Direction = (0,0,1)
  Length = 8
  Length2 = 10
  Profile = -> Sketch164
  ReferenceAxis = -> Sketch164 [N_Axis]
  Refine = true
  Suppressed = false
  Type = 0
FEATURE [Sketcher::SketchObject] Sketch165
  ArcFitTolerance = 1e-06
  AttachmentSupport = -> [Pad065]
  ExternalGeometry = -> [Pad065]
  FullyConstrained = false
  MakeInternals = false
  MapMode = 5
  Placement = pos=(0,0,-2) rot=(0,0,1;0rad)
  sketch-geometry (5):
    g0: LineSegment StartX=0.5 StartY=249.361 StartZ=0 EndX=0.5 EndY=259.74 EndZ=0
    g1: LineSegment StartX=0.5 StartY=259.74 StartZ=0 EndX=-0.5 EndY=259.74 EndZ=0
    g2: LineSegment StartX=-0.5 StartY=259.74 StartZ=0 EndX=-0.5 EndY=249.361 EndZ=0
    g3: LineSegment StartX=-0.5 StartY=249.361 StartZ=0 EndX=0.5 EndY=249.361 EndZ=0
    g4: GeomPoint [constr] X=0 Y=254.55 Z=0
  constraints (12):
    c: Coincident(g0,g1)
    c: Coincident(g1,g2)
    c: Coincident(g2,g3)
    c: Coincident(g3,g0)
    c: Vertical(g0)
    c: Vertical(g2)
    c: Horizontal(g1)
    c: Horizontal(g3)
    c: Symmetric(g2,g0,g4)
    c: PointOnObject(g4,g-4)
    c: DistanceX(g2,g0) = 1
    c: PointOnObject(g4,g-2)
FEATURE [PartDesign::Pocket] Pocket082
  BaseFeature = -> Pad065
  Direction = (0,0,-1)
  Length = 5
  Length2 = 5
  Profile = -> Sketch165
  ReferenceAxis = -> Sketch165 [N_Axis]
  Refine = true
  Suppressed = false
  Type = 0
FEATURE [Sketcher::SketchObject] Sketch166
  ArcFitTolerance = 1e-06
  AttachmentSupport = -> [Pocket082]
  ExternalGeometry = -> [Pocket082]
  FullyConstrained = false
  MakeInternals = false
  MapMode = 5
  Placement = pos=(0,0,-12) rot=(1,0,0;3.14159rad)
  sketch-geometry (7):
    g0: ArcOfCircle [constr] CenterX=5e-16 CenterY=-210 CenterZ=0 NormalX=0 NormalY=0 NormalZ=1 AngleXU=0 Radius=35.7164 StartAngle=3.18717 EndAngle=6.23761
    g1: Circle CenterX=-35.6793 CenterY=-211.627 CenterZ=0 NormalX=0 NormalY=0 NormalZ=1 AngleXU=0 Radius=6
    g2: Circle CenterX=-25.3169 CenterY=-235.194 CenterZ=0 NormalX=0 NormalY=0 NormalZ=1 AngleXU=0 Radius=6
    g3: Circle CenterX=0 CenterY=-245.716 CenterZ=0 NormalX=0 NormalY=0 NormalZ=1 AngleXU=0 Radius=6
    g4: Circle CenterX=25.3169 CenterY=-235.194 CenterZ=0 NormalX=0 NormalY=0 NormalZ=1 AngleXU=0 Radius=6
    g5: Circle CenterX=35.7563 CenterY=-211.592 CenterZ=0 NormalX=0 NormalY=0 NormalZ=1 AngleXU=0 Radius=1.9552e-12
    g6: Circle CenterX=35.7563 CenterY=-211.592 CenterZ=0 NormalX=0 NormalY=0 NormalZ=1 AngleXU=0 Radius=6
  constraints (14):
    c: Coincident(g0,g-5)
    c: Coincident(g1,g0)
    c: PointOnObject(g2,g0)
    c: PointOnObject(g3,g0)
    c: PointOnObject(g4,g0)
    c: Coincident(g6,g5)
    c: Equal(g1,g2)
    c: Equal(g1,g3)
    c: Equal(g1,g4)
    c: Equal(g1,g6)
    c: Diameter(g1) = 12
    c: Horizontal(g0,g0)
    c: Horizontal(g2,g4)
    c: PointOnObject(g3,g-2)
FEATURE [PartDesign::Pocket] Pocket083
  BaseFeature = -> Pocket082
  Direction = (0,0,1)
  Length = 5
  Length2 = 5
  Profile = -> Sketch166
  ReferenceAxis = -> Sketch166 [N_Axis]
  Refine = true
  Suppressed = false
  Type = 0
FEATURE [Sketcher::SketchObject] Sketch167
  ArcFitTolerance = 1e-06
  AttachmentOffset = pos=(0,0,-1.2) rot=(0,0,1;0rad)
  AttachmentSupport = -> [Pocket083]
  ExternalGeometry = -> [Pocket083]
  FullyConstrained = true
  MakeInternals = false
  MapMode = 5
  Placement = pos=(25.2529,0.227503,-2e-16) rot=(0.573883,0.579076,0.579076;2.0996rad)
  sketch-geometry (5):
    g0: LineSegment StartX=203.77 StartY=-26 StartZ=0 EndX=203.77 EndY=-2 EndZ=0
    g1: LineSegment StartX=203.77 StartY=-2 StartZ=0 EndX=195.77 EndY=-2 EndZ=0
    g2: LineSegment StartX=195.77 StartY=-2 StartZ=0 EndX=195.77 EndY=-26 EndZ=0
    g3: LineSegment StartX=195.77 StartY=-26 StartZ=0 EndX=203.77 EndY=-26 EndZ=0
    g4: GeomPoint [constr] X=199.77 Y=-14 Z=0
  constraints (13):
    c: Coincident(g0,g1)
    c: Coincident(g1,g2)
    c: Coincident(g2,g3)
    c: Coincident(g3,g0)
    c: Vertical(g0)
    c: Vertical(g2)
    c: Horizontal(g1)
    c: Horizontal(g3)
    c: Symmetric(g2,g0,g4)
    c: PointOnObject(g4,g-3)
    c: DistanceY(g0,g-4) = 2
    c: DistanceY(g-5,g0) = 2
    c: DistanceX(g2,g0) = 8
FEATURE [PartDesign::Pad] Pad066
  BaseFeature = -> Pocket083
  Direction = (0.999959,0.00900864,2e-16)
  Length = 2.5
  Length2 = 10
  Profile = -> Sketch167
  ReferenceAxis = -> Sketch167 [N_Axis]
  Refine = true
  Suppressed = false
  Type = 0
FEATURE [Sketcher::SketchObject] Sketch168
  ArcFitTolerance = 1e-06
  AttachmentSupport = -> [XY_Plane056]
  FullyConstrained = false
  MakeInternals = false
  MapMode = 5
  sketch-geometry (6):
    g0: ArcOfCircle CenterX=0 CenterY=0 CenterZ=0 NormalX=0 NormalY=0 NormalZ=1 AngleXU=0 Radius=12.5 StartAngle=1.63083 EndAngle=7.79395
    g1: LineSegment [constr] StartX=-0.75 StartY=14.5429 StartZ=0 EndX=-0.75 EndY=0 EndZ=0
    g2: LineSegment [constr] StartX=0.75 StartY=14.5429 StartZ=0 EndX=0.75 EndY=0 EndZ=0
    g3: ArcOfCircle CenterX=0 CenterY=0 CenterZ=0 NormalX=0 NormalY=0 NormalZ=1 AngleXU=0 Radius=4.2 StartAngle=1.75033 EndAngle=7.67445
    g4: LineSegment StartX=-0.75 StartY=12.4775 StartZ=0 EndX=-0.75 EndY=4.13249 EndZ=0
    g5: LineSegment StartX=0.75 StartY=4.13249 StartZ=0 EndX=0.75 EndY=12.4775 EndZ=0
  constraints (18):
    c: Coincident(g0,g-1)
    c: Diameter(g0) = 25
    c: PointOnObject(g1,g-1)
    c: Vertical(g1)
    c: PointOnObject(g2,g-1)
    c: Vertical(g2)
    c: PointOnObject(g0,g2)
    c: PointOnObject(g0,g1)
    c: Symmetric(g1,g2,g-2)
    c: DistanceX(g1,g2) = 1.5
    c: Coincident(g3,g0)
    c: PointOnObject(g3,g1)
    c: PointOnObject(g3,g2)
    c: Radius(g3) = 4.2
    c: Coincident(g4,g0)
    c: Coincident(g4,g3)
    c: Coincident(g5,g3)
    c: Coincident(g5,g0)
FEATURE [PartDesign::Pad] Pad067
  Direction = (0,0,1)
  Length = 36
  Length2 = 10
  Profile = -> Sketch168
  ReferenceAxis = -> Sketch168 [N_Axis]
  Refine = true
  Suppressed = false
  Type = 0
FEATURE [Sketcher::SketchObject] Sketch169
  ArcFitTolerance = 1e-06
  AttachmentSupport = -> [Pad067]
  ExternalGeometry = -> [Pad067]
  FullyConstrained = false
  MakeInternals = false
  MapMode = 5
  Placement = pos=(0,0,36) rot=(0,0,1;0rad)
  sketch-geometry (4):
    g0: ArcOfCircle CenterX=0 CenterY=0 CenterZ=0 NormalX=0 NormalY=0 NormalZ=1 AngleXU=0 Radius=4.2 StartAngle=1.75033 EndAngle=7.67445
    g1: ArcOfCircle CenterX=0 CenterY=0 CenterZ=0 NormalX=0 NormalY=0 NormalZ=1 AngleXU=0 Radius=7.78347 StartAngle=1.6673 EndAngle=7.75747
    g2: LineSegment StartX=-0.75 StartY=7.74725 StartZ=0 EndX=-0.75 EndY=4.13249 EndZ=0
    g3: LineSegment StartX=0.75 StartY=4.13249 StartZ=0 EndX=0.75 EndY=7.74725 EndZ=0
  constraints (10):
    c: Coincident(g0,g-1)
    c: Coincident(g0,g-5)
    c: Coincident(g1,g0)
    c: PointOnObject(g1,g-3)
    c: PointOnObject(g1,g-4)
    c: Coincident(g2,g1)
    c: Coincident(g2,g0)
    c: Coincident(g3,g0)
    c: Coincident(g3,g1)
    c: Vertical(g3)
FEATURE [PartDesign::Pad] Pad068
  BaseFeature = -> Pad067
  Direction = (0,0,1)
  Length = 3
  Length2 = 10
  Profile = -> Sketch169
  ReferenceAxis = -> Sketch169 [N_Axis]
  Refine = true
  Suppressed = false
  Type = 0
FEATURE [PartDesign::Plane] DatumPlane002
  AttachmentOffset = pos=(0,0,0) rot=(0,1,0;1.5708rad)
  AttachmentSupport = -> [Pad068]
  Length = 75.3137
  MapMode = 5
  Placement = pos=(0,0,0) rot=(0.707107,0,0.707107;3.14159rad)
  ResizeMode = 0
  Width = 61.3137
FEATURE [Sketcher::SketchObject] Sketch170
  ArcFitTolerance = 1e-06
  AttachmentSupport = -> [DatumPlane002]
  ExternalGeometry = -> [Pad068]
  FullyConstrained = false
  MakeInternals = false
  MapMode = 5
  Placement = pos=(0,0,0) rot=(0.707107,0,0.707107;3.14159rad)
  sketch-geometry (6):
    g0: LineSegment [constr] StartX=28 StartY=37.7953 StartZ=0 EndX=28 EndY=-40.7329 EndZ=0
    g1: GeomPoint [constr] X=0 Y=39.3749 Z=0
    g2: Circle CenterX=3 CenterY=0 CenterZ=0 NormalX=0 NormalY=0 NormalZ=1 AngleXU=0 Radius=1.25
    g3: Circle CenterX=25 CenterY=0 CenterZ=0 NormalX=0 NormalY=0 NormalZ=1 AngleXU=0 Radius=1.25
    g4: GeomPoint X=28 Y=-1.46879 Z=0
    g5: Circle CenterX=14 CenterY=0 CenterZ=0 NormalX=0 NormalY=0 NormalZ=1 AngleXU=0 Radius=1.7
  constraints (13):
    c: Vertical(g0)
    c: PointOnObject(g1,g-2)
    c: DistanceX(g1,g0) = 28
    c: PointOnObject(g2,g-1)
    c: PointOnObject(g3,g-1)
    c: Equal(g2,g3)
    c: Diameter(g2) = 2.5
    c: DistanceX(g-1,g2) = 3
    c: Symmetric(g0,g0,g4)
    c: DistanceX(g3,g4) = 3
    c: PointOnObject(g5,g-1)
    c: DistanceX(g1,g5) = 14
    c: Diameter(g5) = 3.4
FEATURE [PartDesign::Pocket] Pocket084
  BaseFeature = -> Pad068
  Direction = (-1,0,2e-16)
  Length = 25
  Length2 = 25
  Profile = -> Sketch170
  ReferenceAxis = -> Sketch170 [N_Axis]
  Refine = true
  Suppressed = false
  Type = 4
FEATURE [PartDesign::Plane] DatumPlane003
  AttachmentOffset = pos=(-7,0,0) rot=(0,1,0;1.5708rad)
  AttachmentSupport = -> [Pocket084]
  Length = 75.3137
  MapMode = 5
  Placement = pos=(-7,0,0) rot=(0.707107,0,0.707107;3.14159rad)
  ResizeMode = 0
  Width = 61.3137
FEATURE [Sketcher::SketchObject] Sketch171
  ArcFitTolerance = 1e-06
  AttachmentSupport = -> [DatumPlane003]
  FullyConstrained = false
  MakeInternals = false
  MapMode = 5
  Placement = pos=(-7,0,0) rot=(0.707107,0,0.707107;3.14159rad)
  sketch-geometry (5):
    g0: LineSegment StartX=11.1 StartY=19.5049 StartZ=0 EndX=11.1 EndY=-5.30198 EndZ=0
    g1: LineSegment StartX=11.1 StartY=-5.30198 StartZ=0 EndX=16.9 EndY=-5.30198 EndZ=0
    g2: LineSegment StartX=16.9 StartY=-5.30198 StartZ=0 EndX=16.9 EndY=19.5049 EndZ=0
    g3: LineSegment StartX=16.9 StartY=19.5049 StartZ=0 EndX=11.1 EndY=19.5049 EndZ=0
    g4: GeomPoint [constr] X=14 Y=7.10147 Z=0
  constraints (11):
    c: Coincident(g0,g1)
    c: Coincident(g1,g2)
    c: Coincident(g2,g3)
    c: Coincident(g3,g0)
    c: Vertical(g0)
    c: Vertical(g2)
    c: Horizontal(g1)
    c: Horizontal(g3)
    c: Symmetric(g2,g0,g4)
    c: DistanceX(g0,g2) = 5.8
    c: DistanceX(g-1,g4) = 14
FEATURE [PartDesign::Pocket] Pocket085
  BaseFeature = -> Pocket084
  Direction = (-1,0,2e-16)
  Length = 2.5
  Length2 = 5
  Profile = -> Sketch171
  ReferenceAxis = -> Sketch171 [N_Axis]
  Refine = true
  Suppressed = false
  Type = 0
FEATURE [PartDesign::Plane] DatumPlane004
  AttachmentOffset = pos=(7,0,0) rot=(0,-1,0;1.5708rad)
  AttachmentSupport = -> [Pocket085]
  Length = 75.3137
  MapMode = 5
  Placement = pos=(7,0,0) rot=(0.707107,0,-0.707107;3.14159rad)
  ResizeMode = 0
  Width = 61.3137
FEATURE [Sketcher::SketchObject] Sketch172
  ArcFitTolerance = 1e-06
  AttachmentSupport = -> [DatumPlane004]
  FullyConstrained = true
  MakeInternals = false
  MapMode = 5
  Placement = pos=(7,0,0) rot=(0.707107,0,-0.707107;3.14159rad)
FEATURE [Sketcher::SketchObject] Sketch173
  ArcFitTolerance = 1e-06
  AttachmentSupport = -> [DatumPlane004]
  FullyConstrained = false
  MakeInternals = false
  MapMode = 5
  Placement = pos=(7,0,0) rot=(0.707107,0,-0.707107;3.14159rad)
  sketch-geometry (5):
    g0: LineSegment StartX=-16.9 StartY=33.5082 StartZ=0 EndX=-16.9 EndY=-4.41611 EndZ=0
    g1: LineSegment StartX=-16.9 StartY=-4.41611 StartZ=0 EndX=-11.1 EndY=-4.41611 EndZ=0
    g2: LineSegment StartX=-11.1 StartY=-4.41611 StartZ=0 EndX=-11.1 EndY=33.5082 EndZ=0
    g3: LineSegment StartX=-11.1 StartY=33.5082 StartZ=0 EndX=-16.9 EndY=33.5082 EndZ=0
    g4: GeomPoint [constr] X=-14 Y=14.546 Z=0
  constraints (11):
    c: Coincident(g0,g1)
    c: Coincident(g1,g2)
    c: Coincident(g2,g3)
    c: Coincident(g3,g0)
    c: Vertical(g0)
    c: Vertical(g2)
    c: Horizontal(g1)
    c: Horizontal(g3)
    c: Symmetric(g2,g0,g4)
    c: DistanceX(g4,g-1) = 14
    c: DistanceX(g0,g1) = 5.8
FEATURE [PartDesign::Pocket] Pocket086
  BaseFeature = -> Pocket085
  Direction = (1,0,2e-16)
  Length = 2.5
  Length2 = 5
  Profile = -> Sketch173
  ReferenceAxis = -> Sketch173 [N_Axis]
  Refine = true
  Suppressed = false
  Type = 0
FEATURE [PartDesign::Fillet] Fillet041
  Base = -> Pocket086 [Edge17]
  BaseFeature = -> Pocket086
  Radius = 1
  Refine = true
  SupportTransform = false
  Suppressed = false
  UseAllEdges = false
FEATURE [PartDesign::Fillet] Fillet042
  Base = -> Fillet041 [Edge7]
  BaseFeature = -> Fillet041
  Radius = 1
  Refine = true
  SupportTransform = false
  Suppressed = false
  UseAllEdges = false
FEATURE [PartDesign::Body] Body041  label="RODHUB2"
  AllowCompound = false
  Group = -> [Sketch168,Pad067,Sketch169,Pad068,DatumPlane002,Sketch170,Pocket084,DatumPlane003,Sketch171,Pocket085,DatumPlane004,Sketch172,Sketch173,Pocket086,Fillet041,Fillet042]
  Origin = -> Origin056
  Placement = pos=(0,0,-1) rot=(0,0,1;0rad)
  Tip = -> Fillet042
FEATURE [PartDesign::Plane] DatumPlane005
  AttachmentOffset = pos=(0,-236,0) rot=(1,0,0;1.5708rad)
  Length = 108.112
  MapMode = 5
  Placement = pos=(0,236,-28) rot=(1,0,0;4.71239rad)
  ResizeMode = 0
  Width = 67.1163
FEATURE [Sketcher::SketchObject] Sketch174
  ArcFitTolerance = 1e-06
  AttachmentSupport = -> [DatumPlane005]
  FullyConstrained = true
  MakeInternals = false
  MapMode = 5
  Placement = pos=(0,236,-28) rot=(-1,0,0;1.5708rad)
  sketch-geometry (2):
    g0: Circle CenterX=0 CenterY=-3 CenterZ=0 NormalX=0 NormalY=0 NormalZ=1 AngleXU=0 Radius=1.25
    g1: Circle CenterX=0 CenterY=-25 CenterZ=0 NormalX=0 NormalY=0 NormalZ=1 AngleXU=0 Radius=1.25
  constraints (6):
    c: PointOnObject(g0,g-2)
    c: PointOnObject(g1,g-2)
    c: DistanceY(g0,g-1) = 3
    c: Equal(g1,g0)
    c: Diameter(g0) = 2.5
    c: DistanceY(g1,g-1) = 25
FEATURE [PartDesign::Pocket] Pocket087
  BaseFeature = -> Pad066
  Direction = (0,-1,-2e-16)
  Length = 12
  Length2 = 5
  Profile = -> Sketch174
  ReferenceAxis = -> Sketch174 [N_Axis]
  Refine = true
  Suppressed = false
  Type = 0
FEATURE [Sketcher::SketchObject] Sketch175
  ArcFitTolerance = 1e-06
  AttachmentSupport = -> [DatumPlane005]
  FullyConstrained = false
  MakeInternals = false
  MapMode = 5
  Placement = pos=(0,236,-28) rot=(-1,0,0;1.5708rad)
  sketch-geometry (8):
    g0: ArcOfCircle CenterX=0 CenterY=10.9868 CenterZ=0 NormalX=0 NormalY=0 NormalZ=1 AngleXU=0 Radius=2.5 StartAngle=0 EndAngle=3.14159
    g1: ArcOfCircle CenterX=2e-16 CenterY=-3 CenterZ=0 NormalX=0 NormalY=0 NormalZ=1 AngleXU=0 Radius=2.5 StartAngle=3.14159 EndAngle=6.28319
    g2: LineSegment StartX=2.5 StartY=10.9868 StartZ=0 EndX=2.5 EndY=-3 EndZ=0
    g3: LineSegment StartX=-2.5 StartY=10.9868 StartZ=0 EndX=-2.5 EndY=-3 EndZ=0
    g4: ArcOfCircle CenterX=0 CenterY=-40.5534 CenterZ=0 NormalX=0 NormalY=0 NormalZ=1 AngleXU=0 Radius=2.5 StartAngle=3.14159 EndAngle=6.28319
    g5: ArcOfCircle CenterX=1e-16 CenterY=-25 CenterZ=0 NormalX=0 NormalY=0 NormalZ=1 AngleXU=0 Radius=2.5 StartAngle=2e-16 EndAngle=3.14159
    g6: LineSegment StartX=-2.5 StartY=-40.5534 StartZ=0 EndX=-2.5 EndY=-25 EndZ=0
    g7: LineSegment StartX=2.5 StartY=-40.5534 StartZ=0 EndX=2.5 EndY=-25 EndZ=0
  constraints (18):
    c: Tangent(g0,g2) = 1.5708
    c: Tangent(g0,g3) = -1.5708
    c: Tangent(g1,g2) = 1.5708
    c: Tangent(g1,g3) = -1.5708
    c: Equal(g0,g1)
    c: Vertical(g3)
    c: PointOnObject(g0,g-2)
    c: Tangent(g4,g6) = 1.5708
    c: Tangent(g4,g7) = -1.5708
    c: Tangent(g5,g6) = 1.5708
    c: Tangent(g5,g7) = -1.5708
    c: Equal(g4,g5)
    c: Vertical(g7)
    c: PointOnObject(g4,g-2)
    c: Equal(g1,g5)
    c: Diameter(g1) = 5
    c: DistanceY(g1,g-1) = 3
    c: DistanceY(g5,g-1) = 25
FEATURE [PartDesign::Pocket] Pocket088
  BaseFeature = -> Pocket087
  Direction = (0,-1,-2e-16)
  Length = 2
  Length2 = 5
  Profile = -> Sketch175
  ReferenceAxis = -> Sketch175 [N_Axis]
  Refine = true
  Suppressed = false
  Type = 0
FEATURE [Sketcher::SketchObject] Sketch176
  ArcFitTolerance = 1e-06
  AttachmentSupport = -> [Pocket046]
  ExternalGeometry = -> [Pocket046]
  FullyConstrained = false
  MakeInternals = false
  MapMode = 5
  Placement = pos=(3.51e-14,159.624,0) rot=(0.57735,0.57735,0.57735;4.18879rad)
  sketch-geometry (4):
    g0: LineSegment StartX=9 StartY=4 StartZ=0 EndX=9 EndY=-6.76861 EndZ=0
    g1: LineSegment StartX=9 StartY=-6.76861 StartZ=0 EndX=19 EndY=-6.76861 EndZ=0
    g2: LineSegment StartX=19 StartY=-6.76861 StartZ=0 EndX=19 EndY=4 EndZ=0
    g3: LineSegment StartX=19 StartY=4 StartZ=0 EndX=9 EndY=4 EndZ=0
  constraints (11):
    c: Coincident(g0,g1)
    c: Coincident(g1,g2)
    c: Coincident(g2,g3)
    c: Coincident(g3,g0)
    c: Vertical(g0)
    c: Vertical(g2)
    c: Horizontal(g1)
    c: Horizontal(g3)
    c: Horizontal(g2,g-4)
    c: DistanceX(g2,g-4) = 3
    c: DistanceX(g-3,g0) = 3
FEATURE [PartDesign::Pocket] Pocket089
  BaseFeature = -> Pocket046
  Direction = (0,-1,0)
  Length = 5
  Length2 = 5
  Placement = pos=(0,0,0) rot=(1,1,1;2.0944rad)
  Profile = -> Sketch176
  ReferenceAxis = -> Sketch176 [N_Axis]
  Refine = true
  Suppressed = false
  Type = 0
FEATURE [Sketcher::SketchObject] Sketch177
  ArcFitTolerance = 1e-06
  AttachmentSupport = -> [Pocket089]
  ExternalGeometry = -> [Pocket089]
  FullyConstrained = false
  MakeInternals = false
  MapMode = 5
  Placement = pos=(2.2e-15,10,0) rot=(0.57735,0.57735,-0.57735;2.0944rad)
  sketch-geometry (4):
    g0: LineSegment StartX=-19 StartY=4 StartZ=0 EndX=-19 EndY=-7.26048 EndZ=0
    g1: LineSegment StartX=-19 StartY=-7.26048 StartZ=0 EndX=-9 EndY=-7.26048 EndZ=0
    g2: LineSegment StartX=-9 StartY=-7.26048 StartZ=0 EndX=-9 EndY=4 EndZ=0
    g3: LineSegment StartX=-9 StartY=4 StartZ=0 EndX=-19 EndY=4 EndZ=0
  constraints (11):
    c: Coincident(g0,g1)
    c: Coincident(g1,g2)
    c: Coincident(g2,g3)
    c: Coincident(g3,g0)
    c: Vertical(g0)
    c: Vertical(g2)
    c: Horizontal(g1)
    c: Horizontal(g3)
    c: Horizontal(g-4,g2)
    c: DistanceX(g2,g-4) = 3
    c: DistanceX(g-3,g0) = 3
FEATURE [PartDesign::Pocket] Pocket090
  BaseFeature = -> Pocket089
  Direction = (1e-16,1,-1e-15)
  Length = 5
  Length2 = 5
  Placement = pos=(0,0,0) rot=(1,1,1;2.0944rad)
  Profile = -> Sketch177
  ReferenceAxis = -> Sketch177 [N_Axis]
  Refine = true
  Suppressed = false
  Type = 0
FEATURE [PartDesign::Body] Body025  label="ELBOW LEFT SIDE"
  AllowCompound = false
  Group = -> [Sketch070,Pad029,Sketch087,Pocket045,Sketch088,Pocket046,Sketch176,Pocket089,Sketch177,Pocket090]
  Origin = -> Origin034
  Placement = pos=(17,0,-1) rot=(0,0,1;0rad)
  Tip = -> Pocket090
FEATURE [Part::Mirroring] Part__Mirroring001  label="ELBOW RIGTH SIDE"
  Base = (0,0,0)
  Normal = (1,0,0)
  Source = -> Body025
FEATURE [PartDesign::Fillet] Fillet043
  Base = -> Pocket088 [Edge47]
  BaseFeature = -> Pocket088
  Radius = 3
  Refine = true
  SupportTransform = false
  Suppressed = false
  UseAllEdges = false
FEATURE [PartDesign::Body] Body038  label="ELBOW SHOULDER END TIP001"
  AllowCompound = false
  Group = -> [Sketch147,Pad054,Sketch148,Pad055,Sketch149,Pad056,Sketch151,Pocket079,Sketch152,Pad057,Sketch163,Pad064,Sketch164,Pad065,Sketch165,Pocket082,Sketch166,Pocket083,Sketch167,Pad066,DatumPlane005,Sketch174,Pocket087,Sketch175,Pocket088,Fillet043]
  Origin = -> Origin048
  Placement = pos=(1.49e-13,209.7,27.9) rot=(0,0,-1;3.14159rad)
  Tip = -> Fillet043
FEATURE [Part::Feature] Part__Feature035  label="Board^Optical Endstop Switch001"
  shape: bbox 33 x 1.612 x 10 mm, 109 faces (baked)
FEATURE [Part::Feature] Part__Feature036  label="TCST2103^Optical Endstop Switch001"
  Placement = pos=(-0.05,1.6,-8.15) rot=(0,0,1;0rad)
  shape: bbox 24.75 x 13.8 x 6.711 mm, 252 faces (baked)
FEATURE [Part::Feature] Part__Feature037  label="RES_0805^Optical Endstop Switch012"
  Placement = pos=(25.5,1.6,-1.86) rot=(0,0,1;0rad)
  shape: bbox 0.5 x 0.45 x 1.2 mm, 18 faces (baked)
FEATURE [Part::Feature] Part__Feature038  label="RES_0805^Optical Endstop Switch013"
  Placement = pos=(25.5,1.6,-1.86) rot=(0,0,1;0rad)
  shape: bbox 0.5 x 0.45 x 1.2 mm, 18 faces (baked)
FEATURE [Part::Feature] Part__Feature039  label="RES_0805^Optical Endstop Switch014"
  Placement = pos=(25.5,1.6,-1.86) rot=(0,0,1;0rad)
  shape: bbox 1.001 x 0.4813 x 1.201 mm, 64 faces (baked)
FEATURE [Part::Feature] Part__Feature040  label="RES_0805^Optical Endstop Switch015"
  Placement = pos=(13.25,0,-2.2) rot=(0,0,1;3.14159rad)
  shape: bbox 0.5 x 0.45 x 1.2 mm, 18 faces (baked)
FEATURE [Part::Feature] Part__Feature041  label="RES_0805^Optical Endstop Switch016"
  Placement = pos=(13.25,0,-2.2) rot=(0,0,1;3.14159rad)
  shape: bbox 0.5 x 0.45 x 1.2 mm, 18 faces (baked)
FEATURE [Part::Feature] Part__Feature042  label="RES_0805^Optical Endstop Switch017"
  Placement = pos=(13.25,0,-2.2) rot=(0,0,1;3.14159rad)
  shape: bbox 1.001 x 0.4813 x 1.201 mm, 64 faces (baked)
FEATURE [Part::Feature] Part__Feature043  label="LED_0805_Green^Optical Endstop Switch006"
  Placement = pos=(27.5,1.6,-5.625) rot=(0,1,0;3.14159rad)
  shape: bbox 1 x 0.28 x 1.25 mm, 6 faces (baked)
FEATURE [Part::Feature] Part__Feature044  label="LED_0805_Green^Optical Endstop Switch007"
  Placement = pos=(27.5,1.6,-5.625) rot=(0,1,0;3.14159rad)
  shape: bbox 0.4 x 0.28 x 1.25 mm, 8 faces (baked)
FEATURE [Part::Feature] Part__Feature045  label="LED_0805_Green^Optical Endstop Switch008"
  Placement = pos=(27.5,1.6,-5.625) rot=(0,1,0;3.14159rad)
  shape: bbox 0.4 x 0.28 x 1.25 mm, 8 faces (baked)
FEATURE [Part::Feature] Part__Feature046  label="LED_0805_Green^Optical Endstop Switch009"
  Placement = pos=(27.5,1.6,-5.625) rot=(0,1,0;3.14159rad)
  shape: bbox 1 x 0.4049 x 1.25 mm, 18 faces (baked)
FEATURE [App::Part] LED_0805_Green_Optical_Endstop_Switch001  label="LED_0805_Green^Optical Endstop Switch005"
  Group = -> [Part__Feature043,Part__Feature044,Part__Feature045,Part__Feature046]
  Origin = -> Origin059
FEATURE [Part::Feature] Part__Feature047  label="RES_0805^Optical Endstop Switch018"
  Placement = pos=(13.25,0,-6.6) rot=(0,0,1;3.14159rad)
  shape: bbox 0.5 x 0.45 x 1.2 mm, 18 faces (baked)
FEATURE [Part::Feature] Part__Feature048  label="RES_0805^Optical Endstop Switch019"
  Placement = pos=(13.25,0,-6.6) rot=(0,0,1;3.14159rad)
  shape: bbox 0.5 x 0.45 x 1.2 mm, 18 faces (baked)
FEATURE [Part::Feature] Part__Feature049  label="RES_0805^Optical Endstop Switch020"
  Placement = pos=(13.25,0,-6.6) rot=(0,0,1;3.14159rad)
  shape: bbox 1.001 x 0.4813 x 1.201 mm, 64 faces (baked)
FEATURE [Part::Feature] Part__Feature050  label="JST-XH-3A^Optical Endstop Switch001"
  Placement = pos=(32.67,0,-9.95) rot=(0.707107,0,0.707107;3.14159rad)
  shape: bbox 5.75 x 10.5 x 9.9 mm, 107 faces (baked)
FEATURE [App::Part] RES_0805_Optical_Endstop_Switch003  label="RES_0805^Optical Endstop Switch021"
  Group = -> [Part__Feature037,Part__Feature038,Part__Feature039]
  Origin = -> Origin057
FEATURE [App::Part] RES_0805_Optical_Endstop_Switch004  label="RES_0805^Optical Endstop Switch022"
  Group = -> [Part__Feature040,Part__Feature041,Part__Feature042]
  Origin = -> Origin058
FEATURE [App::Part] RES_0805_Optical_Endstop_Switch005  label="RES_0805^Optical Endstop Switch023"
  Group = -> [Part__Feature047,Part__Feature048,Part__Feature049]
  Origin = -> Origin060
FEATURE [App::Part] Optical_Endstop_Switch001  label="Optical Endstop Switch001"
  Group = -> [Part__Feature035,Part__Feature036,RES_0805_Optical_Endstop_Switch003,RES_0805_Optical_Endstop_Switch004,LED_0805_Green_Optical_Endstop_Switch001,RES_0805_Optical_Endstop_Switch005,Part__Feature050]
  Origin = -> Origin061
  Placement = pos=(5,22.8,12.9) rot=(-0.57735,-0.57735,-0.57735;4.18879rad)
FEATURE [Sketcher::SketchObject] Sketch178
  ArcFitTolerance = 1e-06
  AttachmentSupport = -> [Pocket051]
  FullyConstrained = false
  MakeInternals = false
  MapMode = 5
  Placement = pos=(0,0,6) rot=(0,0,1;0rad)
  sketch-geometry (10):
    g0: LineSegment StartX=-9.35346 StartY=192.119 StartZ=0 EndX=-9.35346 EndY=139.582 EndZ=0
    g1: LineSegment StartX=-3.73646 StartY=133.965 StartZ=0 EndX=3.73646 EndY=133.965 EndZ=0
    g2: LineSegment StartX=9.35346 StartY=139.582 StartZ=0 EndX=9.35346 EndY=192.119 EndZ=0
    g3: LineSegment StartX=3.73646 StartY=197.736 StartZ=0 EndX=-3.73646 EndY=197.736 EndZ=0
    g4: ArcOfCircle CenterX=-3.73646 CenterY=192.119 CenterZ=0 NormalX=0 NormalY=0 NormalZ=1 AngleXU=0 Radius=5.617 StartAngle=1.5708 EndAngle=3.14159
    g5: ArcOfCircle CenterX=-3.73646 CenterY=139.582 CenterZ=0 NormalX=0 NormalY=0 NormalZ=1 AngleXU=0 Radius=5.617 StartAngle=3.14159 EndAngle=4.71239
    g6: ArcOfCircle CenterX=3.73646 CenterY=139.582 CenterZ=0 NormalX=0 NormalY=0 NormalZ=1 AngleXU=0 Radius=5.617 StartAngle=4.71239 EndAngle=6.28319
    g7: ArcOfCircle CenterX=3.73646 CenterY=192.119 CenterZ=0 NormalX=0 NormalY=0 NormalZ=1 AngleXU=0 Radius=5.617 StartAngle=1.2e-15 EndAngle=1.5708
    g8: GeomPoint [constr] X=-9.35346 Y=197.736 Z=0
    g9: GeomPoint [constr] X=9.35346 Y=133.965 Z=0
  constraints (19):
    c: Tangent(g0,g4) = -1.5708
    c: Tangent(g0,g5) = -1.5708
    c: Tangent(g1,g5) = -1.5708
    c: Tangent(g1,g6) = -1.5708
    c: Tangent(g2,g6) = -1.5708
    c: Tangent(g2,g7) = -1.5708
    c: Tangent(g3,g7) = -1.5708
    c: Tangent(g3,g4) = -1.5708
    c: Vertical(g0)
    c: Vertical(g2)
    c: Horizontal(g1)
    c: Horizontal(g3)
    c: Equal(g4,g5)
    c: Equal(g5,g6)
    c: PointOnObject(g8,g0)
    c: PointOnObject(g8,g3)
    c: PointOnObject(g9,g1)
    c: PointOnObject(g9,g2)
    c: Symmetric(g4,g7,g-2)
FEATURE [PartDesign::Pad] Pad069
  BaseFeature = -> Pocket051
  Direction = (0,0,1)
  Length = 6
  Length2 = 10
  Profile = -> Sketch178
  ReferenceAxis = -> Sketch178 [N_Axis]
  Refine = true
  Reversed = true
  Suppressed = false
  Type = 0
FEATURE [Sketcher::SketchObject] Sketch180
  ArcFitTolerance = 1e-06
  FullyConstrained = false
  MakeInternals = false
  MapMode = 5
  Placement = pos=(0,0,6) rot=(0,0,1;0rad)
  sketch-geometry (7):
    g0: Circle CenterX=0 CenterY=25.4753 CenterZ=0 NormalX=0 NormalY=0 NormalZ=1 AngleXU=0 Radius=1.25
    g1: Circle CenterX=0 CenterY=44.4626 CenterZ=0 NormalX=0 NormalY=0 NormalZ=1 AngleXU=0 Radius=1.25
    g2: LineSegment StartX=-5.55274 StartY=49.3317 StartZ=0 EndX=5.55274 EndY=49.3317 EndZ=0
    g3: LineSegment StartX=5.55274 StartY=49.3317 StartZ=0 EndX=5.55274 EndY=56.1793 EndZ=0
    g4: LineSegment StartX=5.55274 StartY=56.1793 StartZ=0 EndX=-5.55274 EndY=56.1793 EndZ=0
    g5: LineSegment StartX=-5.55274 StartY=56.1793 StartZ=0 EndX=-5.55274 EndY=49.3317 EndZ=0
    g6: GeomPoint [constr] X=0 Y=52.7555 Z=0
  constraints (14):
    c: PointOnObject(g0,g-2)
    c: PointOnObject(g1,g-2)
    c: Equal(g0,g1)
    c: Diameter(g1) = 2.5
    c: Coincident(g2,g3)
    c: Coincident(g3,g4)
    c: Coincident(g4,g5)
    c: Coincident(g5,g2)
    c: Horizontal(g2)
    c: Horizontal(g4)
    c: Vertical(g3)
    c: Vertical(g5)
    c: Symmetric(g4,g2,g6)
    c: PointOnObject(g6,g-2)
FEATURE [PartDesign::Pocket] Pocket092
  BaseFeature = -> Pad069
  Direction = (0,0,-1)
  Length = 10
  Length2 = 5
  Profile = -> Sketch180
  ReferenceAxis = -> Sketch180 [N_Axis]
  Refine = true
  Suppressed = false
  Type = 0
FEATURE [Sketcher::SketchObject] Sketch187
  ArcFitTolerance = 1e-06
  AttachmentSupport = -> [XY_Plane063]
  FullyConstrained = false
  MakeInternals = false
  MapMode = 5
  sketch-geometry (12):
    g0: LineSegment StartX=-7.39846 StartY=29.0983 StartZ=0 EndX=-7.39846 EndY=-0.939493 EndZ=0
    g1: LineSegment StartX=7.39846 StartY=-0.939493 StartZ=0 EndX=7.39846 EndY=28.7739 EndZ=0
    g2: LineSegment StartX=5.46004 StartY=30.7123 StartZ=0 EndX=-5.78438 EndY=30.7123 EndZ=0
    g3: ArcOfCircle CenterX=5.46004 CenterY=28.7739 CenterZ=0 NormalX=0 NormalY=0 NormalZ=1 AngleXU=0 Radius=1.93841 StartAngle=3e-16 EndAngle=1.5708
    g4: GeomPoint [constr] X=7.39846 Y=30.7123 Z=0
    g5: ArcOfCircle CenterX=-5.78438 CenterY=29.0983 CenterZ=0 NormalX=0 NormalY=0 NormalZ=1 AngleXU=0 Radius=1.61408 StartAngle=1.5708 EndAngle=3.14159
    g6: GeomPoint [constr] X=-7.39846 Y=30.7123 Z=0
    g7: ArcOfCircle CenterX=-5.3481 CenterY=-0.939493 CenterZ=0 NormalX=0 NormalY=0 NormalZ=1 AngleXU=0 Radius=2.05036 StartAngle=3.14159 EndAngle=4.84672
    g8: GeomPoint [constr] X=-7.39846 Y=-1.83994 Z=0
    g9: ArcOfCircle CenterX=5.25743 CenterY=-0.939493 CenterZ=0 NormalX=0 NormalY=0 NormalZ=1 AngleXU=0 Radius=2.14103 StartAngle=4.69794 EndAngle=6.28319
    g10: GeomPoint [constr] X=7.39846 Y=-1.83994 Z=0
    g11: ArcOfCircle CenterX=0 CenterY=-10.26 CenterZ=0 NormalX=0 NormalY=0 NormalZ=1 AngleXU=0 Radius=8.88053 StartAngle=0.941553 EndAngle=2.17889
  constraints (19):
    c: Vertical(g0)
    c: Vertical(g1)
    c: Symmetric(g6,g4,g-2)
    c: PointOnObject(g4,g1)
    c: PointOnObject(g4,g2)
    c: Tangent(g1,g3) = -1.5708
    c: Tangent(g2,g3) = -1.5708
    c: PointOnObject(g6,g0)
    c: PointOnObject(g6,g2)
    c: Tangent(g0,g5) = -1.5708
    c: Tangent(g2,g5) = -1.5708
    c: PointOnObject(g8,g0)
    c: Tangent(g0,g7) = -1.5708
    c: PointOnObject(g10,g1)
    c: Tangent(g1,g9) = -1.5708
    c: PointOnObject(g11,g-2)
    c: Coincident(g11,g7)
    c: Coincident(g11,g9)
    c: Horizontal(g7,g9)
FEATURE [PartDesign::Pad] Pad072
  Direction = (0,0,1)
  Length = 4.5
  Length2 = 10
  Profile = -> Sketch187
  ReferenceAxis = -> Sketch187 [N_Axis]
  Refine = true
  Suppressed = false
  Type = 0
FEATURE [Sketcher::SketchObject] Sketch188
  ArcFitTolerance = 1e-06
  AttachmentSupport = -> [Pad072]
  FullyConstrained = false
  MakeInternals = false
  MapMode = 5
  Placement = pos=(0,0,4.5) rot=(0,0,1;0rad)
  sketch-geometry (6):
    g0: Circle CenterX=0 CenterY=18.9664 CenterZ=0 NormalX=0 NormalY=0 NormalZ=1 AngleXU=0 Radius=1.6
    g1: Circle CenterX=0 CenterY=0 CenterZ=0 NormalX=0 NormalY=0 NormalZ=1 AngleXU=0 Radius=1.6
    g2: LineSegment StartX=-5.52874 StartY=32.2689 StartZ=0 EndX=-5.52874 EndY=23.5034 EndZ=0
    g3: LineSegment StartX=-5.52874 StartY=23.5034 StartZ=0 EndX=5.50438 EndY=23.5034 EndZ=0
    g4: LineSegment StartX=5.50438 StartY=23.5034 StartZ=0 EndX=5.50438 EndY=32.2689 EndZ=0
    g5: LineSegment StartX=5.50438 StartY=32.2689 StartZ=0 EndX=-5.52874 EndY=32.2689 EndZ=0
  constraints (12):
    c: PointOnObject(g0,g-2)
    c: Coincident(g1,g-1)
    c: Equal(g1,g0)
    c: Diameter(g1) = 3.2
    c: Coincident(g2,g3)
    c: Coincident(g3,g4)
    c: Coincident(g4,g5)
    c: Coincident(g5,g2)
    c: Vertical(g2)
    c: Vertical(g4)
    c: Horizontal(g3)
    c: Horizontal(g5)
FEATURE [PartDesign::Pocket] Pocket096
  BaseFeature = -> Pad072
  Direction = (0,0,-1)
  Length = 5
  Length2 = 5
  Profile = -> Sketch188
  ReferenceAxis = -> Sketch188 [N_Axis]
  Refine = true
  Suppressed = false
  Type = 0
FEATURE [Sketcher::SketchObject] Sketch189
  ArcFitTolerance = 1e-06
  AttachmentSupport = -> [Pocket096]
  FullyConstrained = false
  MakeInternals = false
  MapMode = 5
  Placement = pos=(0,0,4.5) rot=(0,0,1;0rad)
  sketch-geometry (8):
    g0: LineSegment StartX=-10.4519 StartY=15.8038 StartZ=0 EndX=-10.4519 EndY=2.43585 EndZ=0
    g1: LineSegment StartX=-10.4519 StartY=2.43585 StartZ=0 EndX=10.2797 EndY=2.43585 EndZ=0
    g2: LineSegment StartX=10.2797 StartY=2.43585 StartZ=0 EndX=10.2797 EndY=15.8038 EndZ=0
    g3: LineSegment StartX=10.2797 StartY=15.8038 StartZ=0 EndX=-10.4519 EndY=15.8038 EndZ=0
    g4: LineSegment StartX=-13.0587 StartY=33.1578 StartZ=0 EndX=-13.0587 EndY=22.162 EndZ=0
    g5: LineSegment StartX=-13.0587 StartY=22.162 StartZ=0 EndX=13.6771 EndY=22.162 EndZ=0
    g6: LineSegment StartX=13.6771 StartY=22.162 StartZ=0 EndX=13.6771 EndY=33.1578 EndZ=0
    g7: LineSegment StartX=13.6771 StartY=33.1578 StartZ=0 EndX=-13.0587 EndY=33.1578 EndZ=0
  constraints (16):
    c: Coincident(g0,g1)
    c: Coincident(g1,g2)
    c: Coincident(g2,g3)
    c: Coincident(g3,g0)
    c: Vertical(g0)
    c: Vertical(g2)
    c: Horizontal(g1)
    c: Horizontal(g3)
    c: Coincident(g4,g5)
    c: Coincident(g5,g6)
    c: Coincident(g6,g7)
    c: Coincident(g7,g4)
    c: Vertical(g4)
    c: Vertical(g6)
    c: Horizontal(g5)
    c: Horizontal(g7)
FEATURE [PartDesign::Pocket] Pocket097
  BaseFeature = -> Pocket096
  Direction = (0,0,-1)
  Length = 0.6
  Length2 = 5
  Profile = -> Sketch189
  ReferenceAxis = -> Sketch189 [N_Axis]
  Refine = true
  Suppressed = false
  Type = 0
FEATURE [PartDesign::Body] Body043  label="ENDSTOP SUPPORT"
  AllowCompound = false
  Group = -> [Sketch187,Pad072,Sketch188,Pocket096,Sketch189,Pocket097]
  Origin = -> Origin063
  Placement = pos=(0.5,174,8.5) rot=(0,0,1;3.14159rad)
  Tip = -> Pocket097
FEATURE [Part::Feature] Body044  label="ENDSTOP SUPPORT001"
  Placement = pos=(2.9e-15,25.5,8.5) rot=(0,0,1;0rad)
  shape: bbox 16.22 x 34.55 x 4.5 mm, 22 faces (baked)
FEATURE [Mesh::Feature] Mesh003  label="ENDSTOP SUPPORT (Meshed)"
FEATURE [Sketcher::SketchObject] Sketch190
  ArcFitTolerance = 1e-06
  AttachmentSupport = -> [Pocket092]
  FullyConstrained = false
  MakeInternals = false
  MapMode = 5
  Placement = pos=(0,0,6) rot=(0,0,1;0rad)
  sketch-geometry (7):
    g0: LineSegment [constr] StartX=0 StartY=136.319 StartZ=0 EndX=0 EndY=173.941 EndZ=0
    g1: Circle CenterX=0 CenterY=173.941 CenterZ=0 NormalX=0 NormalY=0 NormalZ=1 AngleXU=0 Radius=1.4
    g2: Circle CenterX=0 CenterY=155.13 CenterZ=0 NormalX=0 NormalY=0 NormalZ=1 AngleXU=0 Radius=1.4
    g3: LineSegment StartX=-5.52333 StartY=142.3 StartZ=0 EndX=5.5432 EndY=142.3 EndZ=0
    g4: LineSegment StartX=5.54321 StartY=142.3 StartZ=0 EndX=5.54321 EndY=150.574 EndZ=0
    g5: LineSegment StartX=5.54321 StartY=150.574 StartZ=0 EndX=-5.52333 EndY=150.574 EndZ=0
    g6: LineSegment StartX=-5.52333 StartY=150.574 StartZ=0 EndX=-5.52333 EndY=142.3 EndZ=0
  constraints (14):
    c: PointOnObject(g0,g-2)
    c: Vertical(g0)
    c: Coincident(g1,g0)
    c: Symmetric(g0,g0,g2)
    c: Coincident(g3,g4)
    c: Coincident(g4,g5)
    c: Coincident(g5,g6)
    c: Coincident(g6,g3)
    c: Horizontal(g3)
    c: Horizontal(g5)
    c: Vertical(g4)
    c: Vertical(g6)
    c: Equal(g2,g1)
    c: Diameter(g2) = 2.8
FEATURE [PartDesign::Pocket] Pocket098
  BaseFeature = -> Pocket092
  Direction = (0,0,-1)
  Length = 10
  Length2 = 5
  Profile = -> Sketch190
  ReferenceAxis = -> Sketch190 [N_Axis]
  Refine = true
  Suppressed = false
  Type = 0
FEATURE [PartDesign::Body] Body013  label="Arm_shoulder_Plate_Bottom"
  AllowCompound = false
  Group = -> [Sketch021,Pad009,Sketch090,Pocket048,Mirrored002,Sketch091,Pocket049,Sketch092,Pocket050,Sketch093,Pocket051,Sketch178,Pad069,Sketch180,Pocket092,Sketch190,Pocket098]
  Origin = -> Origin017
  Placement = pos=(0.5,0,2.5) rot=(0,0,1;0rad)
  Tip = -> Pocket098
FEATURE [Sketcher::SketchObject] Sketch191
  ArcFitTolerance = 1e-06
  AttachmentSupport = -> [XY_Plane064]
  FullyConstrained = true
  MakeInternals = false
  MapMode = 5
  sketch-geometry (1):
    g0: Circle CenterX=0 CenterY=0 CenterZ=0 NormalX=0 NormalY=0 NormalZ=1 AngleXU=0 Radius=12.5
  constraints (2):
    c: Coincident(g0,g-1)
    c: Diameter(g0) = 25
FEATURE [PartDesign::Pad] Pad073
  Direction = (0,0,1)
  Length = 3
  Length2 = 10
  Profile = -> Sketch191
  ReferenceAxis = -> Sketch191 [N_Axis]
  Refine = true
  Suppressed = false
  Type = 0
FEATURE [Sketcher::SketchObject] Sketch192
  ArcFitTolerance = 1e-06
  AttachmentSupport = -> [Pad073]
  FullyConstrained = true
  MakeInternals = false
  MapMode = 5
  Placement = pos=(0,0,3) rot=(0,0,1;0rad)
  sketch-geometry (1):
    g0: Circle CenterX=0 CenterY=0 CenterZ=0 NormalX=0 NormalY=0 NormalZ=1 AngleXU=0 Radius=4
  constraints (2):
    c: Coincident(g0,g-1)
    c: Diameter(g0) = 8
FEATURE [PartDesign::Pocket] Pocket099
  BaseFeature = -> Pad073
  Direction = (0,0,-1)
  Length = 2
  Length2 = 5
  Profile = -> Sketch192
  ReferenceAxis = -> Sketch192 [N_Axis]
  Refine = true
  Suppressed = false
  Type = 0
FEATURE [PartDesign::Body] Body045  label="bottom pulley top guide"
  AllowCompound = false
  Group = -> [Sketch191,Pad073,Sketch192,Pocket099]
  Origin = -> Origin064
  Placement = pos=(0,0,74.5) rot=(0,0,1;0rad)
  Tip = -> Pocket099
FEATURE [App::Part] Part003  label="SHOULDER"
  Group = -> [Part__Feature003,Part__Feature004,Body013,Body014,Body015,GT2_Pulley_3mm_bore_v8,Screw002,Screw,Screw003,Screw004,Screw005,Body017,Screw006,ThreadedRod,Screw007,Body027,Part__Feature017,Part__Feature018,Body028,Body029,Body030,Body031,Optical_Endstop_Switch,Optical_Endstop_Switch001,Body043,Body044,Body045]
  Origin = -> Origin013
  Placement = pos=(1.7e-15,-237.1,-14) rot=(0,1,0;3.14159rad)
FEATURE [Mesh::Feature] Mesh  label="bottom pulley top guide (Meshed)"
FEATURE [Sketcher::SketchObject] Sketch193
  ArcFitTolerance = 1e-06
  AttachmentSupport = -> [Pocket044]
  ExternalGeometry = -> [Pocket044]
  FullyConstrained = false
  MakeInternals = false
  MapMode = 5
  Placement = pos=(0,0,0) rot=(1,0,0;3.14159rad)
  sketch-geometry (6):
    g0: ArcOfCircle CenterX=2e-16 CenterY=45.0584 CenterZ=0 NormalX=0 NormalY=0 NormalZ=1 AngleXU=0 Radius=6.55744 StartAngle=0 EndAngle=3.14159
    g1: LineSegment StartX=-6.55744 StartY=18.6466 StartZ=0 EndX=-6.55744 EndY=45.0584 EndZ=0
    g2: LineSegment StartX=6.55744 StartY=18.6466 StartZ=0 EndX=6.55744 EndY=45.0584 EndZ=0
    g3: Circle CenterX=2e-16 CenterY=45.0584 CenterZ=0 NormalX=0 NormalY=0 NormalZ=1 AngleXU=0 Radius=0.75
    g4: LineSegment [constr] StartX=2e-16 StartY=45.0584 StartZ=0 EndX=13.3796 EndY=45.0584 EndZ=0
    g5: LineSegment StartX=-6.55744 StartY=18.6466 StartZ=0 EndX=6.55744 EndY=18.6466 EndZ=0
  constraints (12):
    c: Tangent(g0,g1) = 1.5708
    c: Tangent(g0,g2) = -1.5708
    c: Vertical(g2)
    c: Coincident(g3,g0)
    c: Diameter(g3) = 1.5
    c: Coincident(g4,g0)
    c: Horizontal(g4)
    c: Block(g4)
    c: PointOnObject(g-3,g2)
    c: Coincident(g5,g1)
    c: Coincident(g5,g2)
    c: Horizontal(g5)
FEATURE [PartDesign::Pad] Pad074
  BaseFeature = -> Pocket044
  Direction = (0,0,-1)
  Length = 6
  Length2 = 10
  Profile = -> Sketch193
  ReferenceAxis = -> Sketch193 [N_Axis]
  Refine = true
  Reversed = true
  Suppressed = false
  Type = 0
FEATURE [PartDesign::Body] Body026  label="Arm_elbow_plate_bot_long"
  AllowCompound = false
  Group = -> [Sketch081,Pad030,Sketch082,Pocket040,Sketch080,Pocket039,Mirrored001,Sketch083,Pocket041,Sketch084,Pocket042,Sketch085,Pocket043,Sketch086,Pocket044,Sketch193,Pad074]
  Origin = -> Origin035
  Placement = pos=(0,-0.2,-0.8) rot=(0,0,1;0rad)
  Tip = -> Pad074
FEATURE [Sketcher::SketchObject] Sketch194
  ArcFitTolerance = 1e-06
  AttachmentSupport = -> [XY_Plane065]
  FullyConstrained = true
  MakeInternals = false
  MapMode = 5
  sketch-geometry (1):
    g0: Circle CenterX=0 CenterY=0 CenterZ=0 NormalX=0 NormalY=0 NormalZ=1 AngleXU=0 Radius=1
  constraints (2):
    c: Diameter(g0) = 2
    c: Coincident(g-1,g0)
FEATURE [PartDesign::Pad] Pad075
  Direction = (0,0,1)
  Length = 25
  Length2 = 10
  Profile = -> Sketch194
  ReferenceAxis = -> Sketch194 [N_Axis]
  Refine = true
  Suppressed = false
  Type = 0
FEATURE [PartDesign::Body] Body046  label="NEEDLE"
  AllowCompound = false
  Group = -> [Sketch194,Pad075]
  Origin = -> Origin065
  Placement = pos=(0,-45.5,-1) rot=(0,0,1;0rad)
  Tip = -> Pad075
FEATURE [App::Part] Part  label="ELBOW"
  Group = -> [Body011,Part__Feature,Body016,Part__Feature008,Body,Body020,Body025,Body026,Part__Mirroring001,Body032,Body038,Body039,Body041,Body046]
  Origin = -> Origin
  Placement = pos=(0,-27.2,-58.6) rot=(0,0,1;0rad)
FEATURE [Mesh::Feature] Mesh004  label="Arm_elbow_plate_bot_long (Meshed)"
